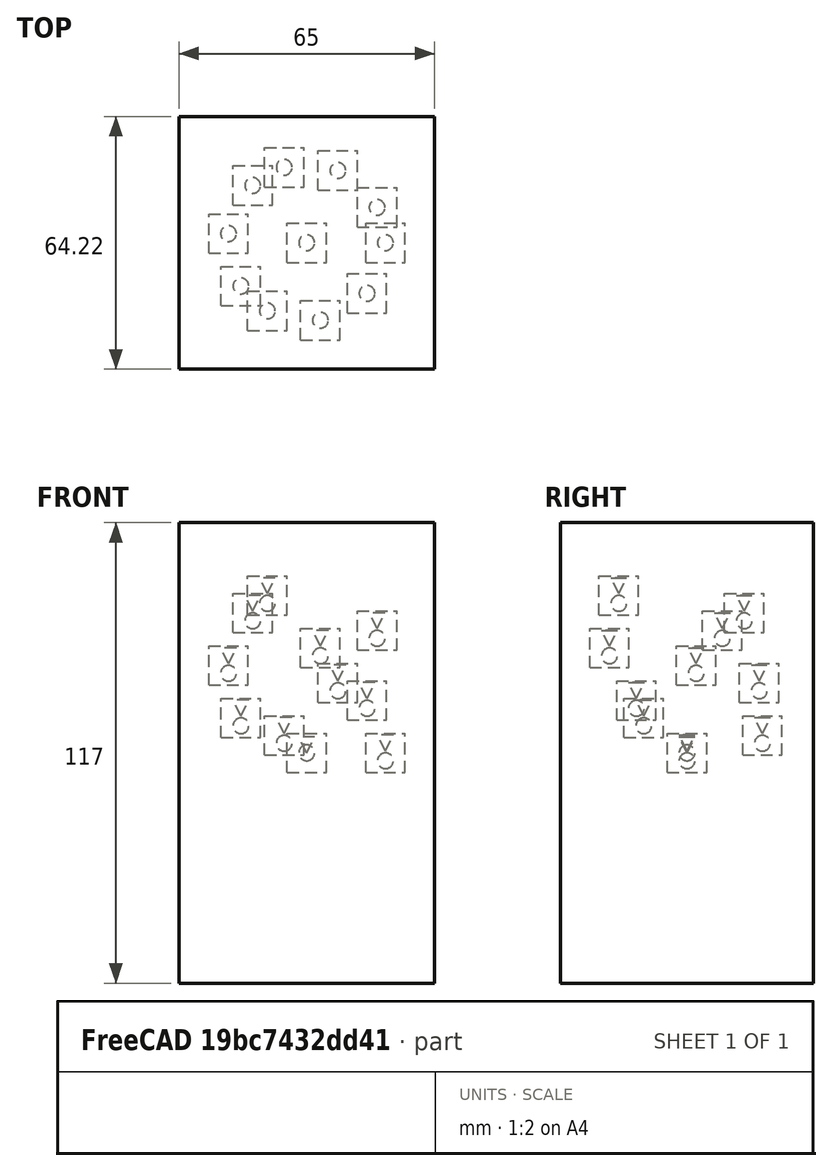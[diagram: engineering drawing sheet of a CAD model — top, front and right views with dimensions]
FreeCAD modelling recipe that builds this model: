
FCSTD DOCUMENT  (FreeCAD 0.21R33694 (Git))
Label: pathArray-of-part
License: All rights reserved
objects: App::DocumentObjectGroupPython×1251, App::Part×5, Part::FeaturePython×4, Part::Helix×1, Part::Cone×1
note: 6 computed .brp shape members not serialized (recipe doc carries the construction recipe); baked Part::Feature solids carry a one-line shape summary decoded from their .brp

FEATURE [App::DocumentObjectGroupPython] HALFPI  # scripted group (container) (typed FeaturePython)
  name = HALFPI
  value = pi/2.
FEATURE [App::DocumentObjectGroupPython] PI  # scripted group (container) (typed FeaturePython)
  name = PI
  value = 1.*pi
FEATURE [App::DocumentObjectGroupPython] TWOPI  # scripted group (container) (typed FeaturePython)
  name = TWOPI
  value = 2.*pi
FEATURE [App::DocumentObjectGroupPython] Constants  # scripted group (container) (typed FeaturePython)
  Group = -> [HALFPI,PI,TWOPI]
FEATURE [App::DocumentObjectGroupPython] Variables  # scripted group (container) (typed FeaturePython)
FEATURE [App::DocumentObjectGroupPython] Quantities  # scripted group (container) (typed FeaturePython)
FEATURE [App::DocumentObjectGroupPython] Isotopes  # scripted group (container) (typed FeaturePython)
FEATURE [App::DocumentObjectGroupPython] Elements  # scripted group (container) (typed FeaturePython)
FEATURE [App::DocumentObjectGroupPython] Matrix  # scripted group (container) (typed FeaturePython)
FEATURE [App::DocumentObjectGroupPython] Surfaces  # scripted group (container) (typed FeaturePython)
FEATURE [App::DocumentObjectGroupPython] Opticals  # scripted group (container) (typed FeaturePython)
  Group = -> [Matrix,Surfaces]
FEATURE [App::DocumentObjectGroupPython] G4Isotopes  # scripted group (container) (typed FeaturePython)
FEATURE [App::DocumentObjectGroupPython] H_element  # scripted group (container) (typed FeaturePython)
  Z = 1
  atom_value = 1.008
  formula = H
  name = H_element
FEATURE [App::DocumentObjectGroupPython] He_element  # scripted group (container) (typed FeaturePython)
  Z = 2
  atom_value = 4.0026
  formula = He
  name = He_element
FEATURE [App::DocumentObjectGroupPython] Li_element  # scripted group (container) (typed FeaturePython)
  Z = 3
  atom_value = 6.94
  formula = Li
  name = Li_element
FEATURE [App::DocumentObjectGroupPython] Be_element  # scripted group (container) (typed FeaturePython)
  Z = 4
  atom_value = 9.01218
  formula = Be
  name = Be_element
FEATURE [App::DocumentObjectGroupPython] B_element  # scripted group (container) (typed FeaturePython)
  Z = 5
  atom_value = 10.81
  formula = B
  name = B_element
FEATURE [App::DocumentObjectGroupPython] C_element  # scripted group (container) (typed FeaturePython)
  Z = 6
  atom_value = 12.011
  formula = C
  name = C_element
FEATURE [App::DocumentObjectGroupPython] N_element  # scripted group (container) (typed FeaturePython)
  Z = 7
  atom_value = 14.007
  formula = N
  name = N_element
FEATURE [App::DocumentObjectGroupPython] O_element  # scripted group (container) (typed FeaturePython)
  Z = 8
  atom_value = 15.999
  formula = O
  name = O_element
FEATURE [App::DocumentObjectGroupPython] F_element  # scripted group (container) (typed FeaturePython)
  Z = 9
  atom_value = 18.9984
  formula = F
  name = F_element
FEATURE [App::DocumentObjectGroupPython] Ne_element  # scripted group (container) (typed FeaturePython)
  Z = 10
  atom_value = 20.1797
  formula = Ne
  name = Ne_element
FEATURE [App::DocumentObjectGroupPython] Na_element  # scripted group (container) (typed FeaturePython)
  Z = 11
  atom_value = 22.9898
  formula = Na
  name = Na_element
FEATURE [App::DocumentObjectGroupPython] Mg_element  # scripted group (container) (typed FeaturePython)
  Z = 12
  atom_value = 24.305
  formula = Mg
  name = Mg_element
FEATURE [App::DocumentObjectGroupPython] Al_element  # scripted group (container) (typed FeaturePython)
  Z = 13
  atom_value = 26.9815
  formula = Al
  name = Al_element
FEATURE [App::DocumentObjectGroupPython] Si_element  # scripted group (container) (typed FeaturePython)
  Z = 14
  atom_value = 28.085
  formula = Si
  name = Si_element
FEATURE [App::DocumentObjectGroupPython] P_element  # scripted group (container) (typed FeaturePython)
  Z = 15
  atom_value = 30.9738
  formula = P
  name = P_element
FEATURE [App::DocumentObjectGroupPython] S_element  # scripted group (container) (typed FeaturePython)
  Z = 16
  atom_value = 32.06
  formula = S
  name = S_element
FEATURE [App::DocumentObjectGroupPython] Cl_element  # scripted group (container) (typed FeaturePython)
  Z = 17
  atom_value = 35.45
  formula = Cl
  name = Cl_element
FEATURE [App::DocumentObjectGroupPython] Ar_element  # scripted group (container) (typed FeaturePython)
  Z = 18
  atom_value = 39.95
  formula = Ar
  name = Ar_element
FEATURE [App::DocumentObjectGroupPython] K_element  # scripted group (container) (typed FeaturePython)
  Z = 19
  atom_value = 39.0983
  formula = K
  name = K_element
FEATURE [App::DocumentObjectGroupPython] Ca_element  # scripted group (container) (typed FeaturePython)
  Z = 20
  atom_value = 40.078
  formula = Ca
  name = Ca_element
FEATURE [App::DocumentObjectGroupPython] Sc_element  # scripted group (container) (typed FeaturePython)
  Z = 21
  atom_value = 44.9559
  formula = Sc
  name = Sc_element
FEATURE [App::DocumentObjectGroupPython] Ti_element  # scripted group (container) (typed FeaturePython)
  Z = 22
  atom_value = 47.867
  formula = Ti
  name = Ti_element
FEATURE [App::DocumentObjectGroupPython] V_element  # scripted group (container) (typed FeaturePython)
  Z = 23
  atom_value = 50.9415
  formula = V
  name = V_element
FEATURE [App::DocumentObjectGroupPython] Cr_element  # scripted group (container) (typed FeaturePython)
  Z = 24
  atom_value = 51.9961
  formula = Cr
  name = Cr_element
FEATURE [App::DocumentObjectGroupPython] Mn_element  # scripted group (container) (typed FeaturePython)
  Z = 25
  atom_value = 54.938
  formula = Mn
  name = Mn_element
FEATURE [App::DocumentObjectGroupPython] Fe_element  # scripted group (container) (typed FeaturePython)
  Z = 26
  atom_value = 55.845
  formula = Fe
  name = Fe_element
FEATURE [App::DocumentObjectGroupPython] Co_element  # scripted group (container) (typed FeaturePython)
  Z = 27
  atom_value = 58.9332
  formula = Co
  name = Co_element
FEATURE [App::DocumentObjectGroupPython] Ni_element  # scripted group (container) (typed FeaturePython)
  Z = 28
  atom_value = 58.6934
  formula = Ni
  name = Ni_element
FEATURE [App::DocumentObjectGroupPython] Cu_element  # scripted group (container) (typed FeaturePython)
  Z = 29
  atom_value = 63.546
  formula = Cu
  name = Cu_element
FEATURE [App::DocumentObjectGroupPython] Zn_element  # scripted group (container) (typed FeaturePython)
  Z = 30
  atom_value = 65.38
  formula = Zn
  name = Zn_element
FEATURE [App::DocumentObjectGroupPython] Ga_element  # scripted group (container) (typed FeaturePython)
  Z = 31
  atom_value = 69.723
  formula = Ga
  name = Ga_element
FEATURE [App::DocumentObjectGroupPython] Ge_element  # scripted group (container) (typed FeaturePython)
  Z = 32
  atom_value = 72.63
  formula = Ge
  name = Ge_element
FEATURE [App::DocumentObjectGroupPython] As_element  # scripted group (container) (typed FeaturePython)
  Z = 33
  atom_value = 74.9216
  formula = As
  name = As_element
FEATURE [App::DocumentObjectGroupPython] Se_element  # scripted group (container) (typed FeaturePython)
  Z = 34
  atom_value = 78.971
  formula = Se
  name = Se_element
FEATURE [App::DocumentObjectGroupPython] Br_element  # scripted group (container) (typed FeaturePython)
  Z = 35
  atom_value = 79.904
  formula = Br
  name = Br_element
FEATURE [App::DocumentObjectGroupPython] Kr_element  # scripted group (container) (typed FeaturePython)
  Z = 36
  atom_value = 83.798
  formula = Kr
  name = Kr_element
FEATURE [App::DocumentObjectGroupPython] Rb_element  # scripted group (container) (typed FeaturePython)
  Z = 37
  atom_value = 85.4678
  formula = Rb
  name = Rb_element
FEATURE [App::DocumentObjectGroupPython] Sr_element  # scripted group (container) (typed FeaturePython)
  Z = 38
  atom_value = 87.62
  formula = Sr
  name = Sr_element
FEATURE [App::DocumentObjectGroupPython] Y_element  # scripted group (container) (typed FeaturePython)
  Z = 39
  atom_value = 88.9058
  formula = Y
  name = Y_element
FEATURE [App::DocumentObjectGroupPython] Zr_element  # scripted group (container) (typed FeaturePython)
  Z = 40
  atom_value = 91.224
  formula = Zr
  name = Zr_element
FEATURE [App::DocumentObjectGroupPython] Nb_element  # scripted group (container) (typed FeaturePython)
  Z = 41
  atom_value = 92.9064
  formula = Nb
  name = Nb_element
FEATURE [App::DocumentObjectGroupPython] Mo_element  # scripted group (container) (typed FeaturePython)
  Z = 42
  atom_value = 95.95
  formula = Mo
  name = Mo_element
FEATURE [App::DocumentObjectGroupPython] Tc_element  # scripted group (container) (typed FeaturePython)
  Z = 43
  atom_value = 97
  formula = Tc
  name = Tc_element
FEATURE [App::DocumentObjectGroupPython] Ru_element  # scripted group (container) (typed FeaturePython)
  Z = 44
  atom_value = 101.07
  formula = Ru
  name = Ru_element
FEATURE [App::DocumentObjectGroupPython] Rh_element  # scripted group (container) (typed FeaturePython)
  Z = 45
  atom_value = 102.905
  formula = Rh
  name = Rh_element
FEATURE [App::DocumentObjectGroupPython] Pd_element  # scripted group (container) (typed FeaturePython)
  Z = 46
  atom_value = 106.42
  formula = Pd
  name = Pd_element
FEATURE [App::DocumentObjectGroupPython] Ag_element  # scripted group (container) (typed FeaturePython)
  Z = 47
  atom_value = 107.868
  formula = Ag
  name = Ag_element
FEATURE [App::DocumentObjectGroupPython] Cd_element  # scripted group (container) (typed FeaturePython)
  Z = 48
  atom_value = 112.414
  formula = Cd
  name = Cd_element
FEATURE [App::DocumentObjectGroupPython] In_element  # scripted group (container) (typed FeaturePython)
  Z = 49
  atom_value = 114.818
  formula = In
  name = In_element
FEATURE [App::DocumentObjectGroupPython] Sn_element  # scripted group (container) (typed FeaturePython)
  Z = 50
  atom_value = 118.71
  formula = Sn
  name = Sn_element
FEATURE [App::DocumentObjectGroupPython] Sb_element  # scripted group (container) (typed FeaturePython)
  Z = 51
  atom_value = 121.76
  formula = Sb
  name = Sb_element
FEATURE [App::DocumentObjectGroupPython] Te_element  # scripted group (container) (typed FeaturePython)
  Z = 52
  atom_value = 127.6
  formula = Te
  name = Te_element
FEATURE [App::DocumentObjectGroupPython] I_element  # scripted group (container) (typed FeaturePython)
  Z = 53
  atom_value = 126.904
  formula = I
  name = I_element
FEATURE [App::DocumentObjectGroupPython] Xe_element  # scripted group (container) (typed FeaturePython)
  Z = 54
  atom_value = 131.293
  formula = Xe
  name = Xe_element
FEATURE [App::DocumentObjectGroupPython] Cs_element  # scripted group (container) (typed FeaturePython)
  Z = 55
  atom_value = 132.905
  formula = Cs
  name = Cs_element
FEATURE [App::DocumentObjectGroupPython] Ba_element  # scripted group (container) (typed FeaturePython)
  Z = 56
  atom_value = 137.327
  formula = Ba
  name = Ba_element
FEATURE [App::DocumentObjectGroupPython] La_element  # scripted group (container) (typed FeaturePython)
  Z = 57
  atom_value = 138.905
  formula = La
  name = La_element
FEATURE [App::DocumentObjectGroupPython] Ce_element  # scripted group (container) (typed FeaturePython)
  Z = 58
  atom_value = 140.116
  formula = Ce
  name = Ce_element
FEATURE [App::DocumentObjectGroupPython] Pr_element  # scripted group (container) (typed FeaturePython)
  Z = 59
  atom_value = 140.908
  formula = Pr
  name = Pr_element
FEATURE [App::DocumentObjectGroupPython] Nd_element  # scripted group (container) (typed FeaturePython)
  Z = 60
  atom_value = 144.242
  formula = Nd
  name = Nd_element
FEATURE [App::DocumentObjectGroupPython] Pm_element  # scripted group (container) (typed FeaturePython)
  Z = 61
  atom_value = 145
  formula = Pm
  name = Pm_element
FEATURE [App::DocumentObjectGroupPython] Sm_element  # scripted group (container) (typed FeaturePython)
  Z = 62
  atom_value = 150.36
  formula = Sm
  name = Sm_element
FEATURE [App::DocumentObjectGroupPython] Eu_element  # scripted group (container) (typed FeaturePython)
  Z = 63
  atom_value = 151.964
  formula = Eu
  name = Eu_element
FEATURE [App::DocumentObjectGroupPython] Gd_element  # scripted group (container) (typed FeaturePython)
  Z = 64
  atom_value = 157.25
  formula = Gd
  name = Gd_element
FEATURE [App::DocumentObjectGroupPython] Tb_element  # scripted group (container) (typed FeaturePython)
  Z = 65
  atom_value = 158.925
  formula = Tb
  name = Tb_element
FEATURE [App::DocumentObjectGroupPython] Dy_element  # scripted group (container) (typed FeaturePython)
  Z = 66
  atom_value = 162.5
  formula = Dy
  name = Dy_element
FEATURE [App::DocumentObjectGroupPython] Ho_element  # scripted group (container) (typed FeaturePython)
  Z = 67
  atom_value = 164.93
  formula = Ho
  name = Ho_element
FEATURE [App::DocumentObjectGroupPython] Er_element  # scripted group (container) (typed FeaturePython)
  Z = 68
  atom_value = 167.259
  formula = Er
  name = Er_element
FEATURE [App::DocumentObjectGroupPython] Tm_element  # scripted group (container) (typed FeaturePython)
  Z = 69
  atom_value = 168.934
  formula = Tm
  name = Tm_element
FEATURE [App::DocumentObjectGroupPython] Yb_element  # scripted group (container) (typed FeaturePython)
  Z = 70
  atom_value = 173.045
  formula = Yb
  name = Yb_element
FEATURE [App::DocumentObjectGroupPython] Lu_element  # scripted group (container) (typed FeaturePython)
  Z = 71
  atom_value = 174.967
  formula = Lu
  name = Lu_element
FEATURE [App::DocumentObjectGroupPython] Hf_element  # scripted group (container) (typed FeaturePython)
  Z = 72
  atom_value = 178.49
  formula = Hf
  name = Hf_element
FEATURE [App::DocumentObjectGroupPython] Ta_element  # scripted group (container) (typed FeaturePython)
  Z = 73
  atom_value = 180.948
  formula = Ta
  name = Ta_element
FEATURE [App::DocumentObjectGroupPython] W_element  # scripted group (container) (typed FeaturePython)
  Z = 74
  atom_value = 183.84
  formula = W
  name = W_element
FEATURE [App::DocumentObjectGroupPython] Re_element  # scripted group (container) (typed FeaturePython)
  Z = 75
  atom_value = 186.207
  formula = Re
  name = Re_element
FEATURE [App::DocumentObjectGroupPython] Os_element  # scripted group (container) (typed FeaturePython)
  Z = 76
  atom_value = 190.23
  formula = Os
  name = Os_element
FEATURE [App::DocumentObjectGroupPython] Ir_element  # scripted group (container) (typed FeaturePython)
  Z = 77
  atom_value = 192.217
  formula = Ir
  name = Ir_element
FEATURE [App::DocumentObjectGroupPython] Pt_element  # scripted group (container) (typed FeaturePython)
  Z = 78
  atom_value = 195.084
  formula = Pt
  name = Pt_element
FEATURE [App::DocumentObjectGroupPython] Au_element  # scripted group (container) (typed FeaturePython)
  Z = 79
  atom_value = 196.967
  formula = Au
  name = Au_element
FEATURE [App::DocumentObjectGroupPython] Hg_element  # scripted group (container) (typed FeaturePython)
  Z = 80
  atom_value = 200.592
  formula = Hg
  name = Hg_element
FEATURE [App::DocumentObjectGroupPython] Tl_element  # scripted group (container) (typed FeaturePython)
  Z = 81
  atom_value = 204.38
  formula = Tl
  name = Tl_element
FEATURE [App::DocumentObjectGroupPython] Pb_element  # scripted group (container) (typed FeaturePython)
  Z = 82
  atom_value = 207.2
  formula = Pb
  name = Pb_element
FEATURE [App::DocumentObjectGroupPython] Bi_element  # scripted group (container) (typed FeaturePython)
  Z = 83
  atom_value = 208.98
  formula = Bi
  name = Bi_element
FEATURE [App::DocumentObjectGroupPython] Po_element  # scripted group (container) (typed FeaturePython)
  Z = 84
  atom_value = 209
  formula = Po
  name = Po_element
FEATURE [App::DocumentObjectGroupPython] At_element  # scripted group (container) (typed FeaturePython)
  Z = 85
  atom_value = 210
  formula = At
  name = At_element
FEATURE [App::DocumentObjectGroupPython] Rn_element  # scripted group (container) (typed FeaturePython)
  Z = 86
  atom_value = 222
  formula = Rn
  name = Rn_element
FEATURE [App::DocumentObjectGroupPython] Fr_element  # scripted group (container) (typed FeaturePython)
  Z = 87
  atom_value = 223
  formula = Fr
  name = Fr_element
FEATURE [App::DocumentObjectGroupPython] Ra_element  # scripted group (container) (typed FeaturePython)
  Z = 88
  atom_value = 226
  formula = Ra
  name = Ra_element
FEATURE [App::DocumentObjectGroupPython] Ac_element  # scripted group (container) (typed FeaturePython)
  Z = 89
  atom_value = 227
  formula = Ac
  name = Ac_element
FEATURE [App::DocumentObjectGroupPython] Th_element  # scripted group (container) (typed FeaturePython)
  Z = 90
  atom_value = 232.038
  formula = Th
  name = Th_element
FEATURE [App::DocumentObjectGroupPython] Pa_element  # scripted group (container) (typed FeaturePython)
  Z = 91
  atom_value = 231.036
  formula = Pa
  name = Pa_element
FEATURE [App::DocumentObjectGroupPython] U_element  # scripted group (container) (typed FeaturePython)
  Z = 92
  atom_value = 238.029
  formula = U
  name = U_element
FEATURE [App::DocumentObjectGroupPython] Np_element  # scripted group (container) (typed FeaturePython)
  Z = 93
  atom_value = 237
  formula = Np
  name = Np_element
FEATURE [App::DocumentObjectGroupPython] Pu_element  # scripted group (container) (typed FeaturePython)
  Z = 94
  atom_value = 244
  formula = Pu
  name = Pu_element
FEATURE [App::DocumentObjectGroupPython] Am_element  # scripted group (container) (typed FeaturePython)
  Z = 95
  atom_value = 243
  formula = Am
  name = Am_element
FEATURE [App::DocumentObjectGroupPython] Cm_element  # scripted group (container) (typed FeaturePython)
  Z = 96
  atom_value = 247
  formula = Cm
  name = Cm_element
FEATURE [App::DocumentObjectGroupPython] Bk_element  # scripted group (container) (typed FeaturePython)
  Z = 97
  atom_value = 247
  formula = Bk
  name = Bk_element
FEATURE [App::DocumentObjectGroupPython] Cf_element  # scripted group (container) (typed FeaturePython)
  Z = 98
  atom_value = 251
  formula = Cf
  name = Cf_element
FEATURE [App::DocumentObjectGroupPython] G4Elements  # scripted group (container) (typed FeaturePython)
  Group = -> [H_element,He_element,Li_element,Be_element,B_element,C_element,N_element,O_element,F_element,Ne_element,Na_element,Mg_element,Al_element,Si_element,P_element,S_element,Cl_element,Ar_element,K_element,Ca_element,Sc_element,Ti_element,V_element,Cr_element,Mn_element,Fe_element,Co_element,Ni_element,Cu_element,Zn_element,Ga_element,Ge_element,As_element,Se_element,Br_element,Kr_element,Rb_element,+61 more]
FEATURE [App::DocumentObjectGroupPython] H_element001  label="H_element : 0.101"  # scripted group (container) (typed FeaturePython)
  n = 0.101327
FEATURE [App::DocumentObjectGroupPython] C_element001  label="C_element : 0.775"  # scripted group (container) (typed FeaturePython)
  n = 0.7755
FEATURE [App::DocumentObjectGroupPython] N_element001  label="N_element : 0.035"  # scripted group (container) (typed FeaturePython)
  n = 0.035057
FEATURE [App::DocumentObjectGroupPython] O_element001  label="O_element : 0.052"  # scripted group (container) (typed FeaturePython)
  n = 0.0523159
FEATURE [App::DocumentObjectGroupPython] F_element001  label="F_element : 0.017"  # scripted group (container) (typed FeaturePython)
  n = 0.017422
FEATURE [App::DocumentObjectGroupPython] Ca_element001  label="Ca_element : 0.018"  # scripted group (container) (typed FeaturePython)
  n = 0.018378
FEATURE [App::DocumentObjectGroupPython] G4_A_150_TISSUE  label="G4_A-150_TISSUE"  # scripted group (container) (typed FeaturePython)
  Dunit = g/cm3
  Dvalue = 1.127
  Group = -> [H_element001,C_element001,N_element001,O_element001,F_element001,Ca_element001]
  conduct = 2
  density = 1
  expand = 3
  formula = G4_A-150_TISSUE
  name = G4_A-150_TISSUE
  specific = 4
FEATURE [App::DocumentObjectGroupPython] C_element002  label="C_element : 3"  # scripted group (container) (typed FeaturePython)
  n = 3
  ref = C_element
FEATURE [App::DocumentObjectGroupPython] H_element002  label="H_element : 6"  # scripted group (container) (typed FeaturePython)
  n = 6
  ref = H_element
FEATURE [App::DocumentObjectGroupPython] O_element002  label="O_element : 1"  # scripted group (container) (typed FeaturePython)
  n = 1
  ref = O_element
FEATURE [App::DocumentObjectGroupPython] G4_ACETONE  # scripted group (container) (typed FeaturePython)
  Dunit = g/cm3
  Dvalue = 0.7899
  Group = -> [C_element002,H_element002,O_element002]
  conduct = 2
  density = 1
  expand = 3
  formula = G4_ACETONE
  name = G4_ACETONE
  specific = 4
FEATURE [App::DocumentObjectGroupPython] C_element003  label="C_element : 2"  # scripted group (container) (typed FeaturePython)
  n = 2
  ref = C_element
FEATURE [App::DocumentObjectGroupPython] H_element003  label="H_element : 2"  # scripted group (container) (typed FeaturePython)
  n = 2
  ref = H_element
FEATURE [App::DocumentObjectGroupPython] G4_ACETYLENE  # scripted group (container) (typed FeaturePython)
  Dunit = g/cm3
  Dvalue = 0.0010967
  Group = -> [C_element003,H_element003]
  conduct = 2
  density = 1
  expand = 3
  formula = G4_ACETYLENE
  name = G4_ACETYLENE
  specific = 4
FEATURE [App::DocumentObjectGroupPython] C_element004  label="C_element : 5"  # scripted group (container) (typed FeaturePython)
  n = 5
  ref = C_element
FEATURE [App::DocumentObjectGroupPython] H_element004  label="H_element : 5"  # scripted group (container) (typed FeaturePython)
  n = 5
  ref = H_element
FEATURE [App::DocumentObjectGroupPython] N_element002  label="N_element : 5"  # scripted group (container) (typed FeaturePython)
  n = 5
  ref = N_element
FEATURE [App::DocumentObjectGroupPython] G4_ADENINE  # scripted group (container) (typed FeaturePython)
  Dunit = g/cm3
  Dvalue = 1.6
  Group = -> [C_element004,H_element004,N_element002]
  conduct = 2
  density = 1
  expand = 3
  formula = G4_ADENINE
  name = G4_ADENINE
  specific = 4
FEATURE [App::DocumentObjectGroupPython] H_element005  label="H_element : 0.114"  # scripted group (container) (typed FeaturePython)
  n = 0.114
FEATURE [App::DocumentObjectGroupPython] C_element005  label="C_element : 0.598"  # scripted group (container) (typed FeaturePython)
  n = 0.598
FEATURE [App::DocumentObjectGroupPython] N_element003  label="N_element : 0.007"  # scripted group (container) (typed FeaturePython)
  n = 0.007
FEATURE [App::DocumentObjectGroupPython] O_element003  label="O_element : 0.278"  # scripted group (container) (typed FeaturePython)
  n = 0.278
FEATURE [App::DocumentObjectGroupPython] Na_element001  label="Na_element : 0.001"  # scripted group (container) (typed FeaturePython)
  n = 0.001
FEATURE [App::DocumentObjectGroupPython] S_element001  label="S_element : 0.001"  # scripted group (container) (typed FeaturePython)
  n = 0.001
FEATURE [App::DocumentObjectGroupPython] Cl_element001  label="Cl_element : 0.001"  # scripted group (container) (typed FeaturePython)
  n = 0.001
FEATURE [App::DocumentObjectGroupPython] G4_ADIPOSE_TISSUE_ICRP  # scripted group (container) (typed FeaturePython)
  Dunit = g/cm3
  Dvalue = 0.95
  Group = -> [H_element005,C_element005,N_element003,O_element003,Na_element001,S_element001,Cl_element001]
  conduct = 2
  density = 1
  expand = 3
  formula = G4_ADIPOSE_TISSUE_ICRP
  name = G4_ADIPOSE_TISSUE_ICRP
  specific = 4
FEATURE [App::DocumentObjectGroupPython] C_element006  label="C_element : 0.000"  # scripted group (container) (typed FeaturePython)
  n = 0.000124
FEATURE [App::DocumentObjectGroupPython] N_element004  label="N_element : 0.755"  # scripted group (container) (typed FeaturePython)
  n = 0.755268
FEATURE [App::DocumentObjectGroupPython] O_element004  label="O_element : 0.232"  # scripted group (container) (typed FeaturePython)
  n = 0.231781
FEATURE [App::DocumentObjectGroupPython] Ar_element001  label="Ar_element : 0.013"  # scripted group (container) (typed FeaturePython)
  n = 0.012827
FEATURE [App::DocumentObjectGroupPython] G4_AIR  # scripted group (container) (typed FeaturePython)
  Dunit = g/cm3
  Dvalue = 0.00120479
  Group = -> [C_element006,N_element004,O_element004,Ar_element001]
  conduct = 2
  density = 1
  expand = 3
  formula = G4_AIR
  name = G4_AIR
  specific = 4
FEATURE [App::DocumentObjectGroupPython] C_element007  label="C_element : 006"  # scripted group (container) (typed FeaturePython)
  n = 3
  ref = C_element
FEATURE [App::DocumentObjectGroupPython] H_element006  label="H_element : 7"  # scripted group (container) (typed FeaturePython)
  n = 7
  ref = H_element
FEATURE [App::DocumentObjectGroupPython] N_element005  label="N_element : 1"  # scripted group (container) (typed FeaturePython)
  n = 1
  ref = N_element
FEATURE [App::DocumentObjectGroupPython] O_element005  label="O_element : 2"  # scripted group (container) (typed FeaturePython)
  n = 2
  ref = O_element
FEATURE [App::DocumentObjectGroupPython] G4_ALANINE  # scripted group (container) (typed FeaturePython)
  Dunit = g/cm3
  Dvalue = 1.42
  Group = -> [C_element007,H_element006,N_element005,O_element005]
  conduct = 2
  density = 1
  expand = 3
  formula = G4_ALANINE
  name = G4_ALANINE
  specific = 4
FEATURE [App::DocumentObjectGroupPython] Al_element001  label="Al_element : 2"  # scripted group (container) (typed FeaturePython)
  n = 2
  ref = Al_element
FEATURE [App::DocumentObjectGroupPython] O_element006  label="O_element : 3"  # scripted group (container) (typed FeaturePython)
  n = 3
  ref = O_element
FEATURE [App::DocumentObjectGroupPython] G4_ALUMINUM_OXIDE  # scripted group (container) (typed FeaturePython)
  Dunit = g/cm3
  Dvalue = 3.97
  Group = -> [Al_element001,O_element006]
  conduct = 2
  density = 1
  expand = 3
  formula = G4_ALUMINUM_OXIDE
  name = G4_ALUMINUM_OXIDE
  specific = 4
FEATURE [App::DocumentObjectGroupPython] H_element007  label="H_element : 0.106"  # scripted group (container) (typed FeaturePython)
  n = 0.10593
FEATURE [App::DocumentObjectGroupPython] C_element008  label="C_element : 0.789"  # scripted group (container) (typed FeaturePython)
  n = 0.788974
FEATURE [App::DocumentObjectGroupPython] O_element007  label="O_element : 0.105"  # scripted group (container) (typed FeaturePython)
  n = 0.105096
FEATURE [App::DocumentObjectGroupPython] G4_AMBER  # scripted group (container) (typed FeaturePython)
  Dunit = g/cm3
  Dvalue = 1.1
  Group = -> [H_element007,C_element008,O_element007]
  conduct = 2
  density = 1
  expand = 3
  formula = G4_AMBER
  name = G4_AMBER
  specific = 4
FEATURE [App::DocumentObjectGroupPython] N_element006  label="N_element : 006"  # scripted group (container) (typed FeaturePython)
  n = 1
  ref = N_element
FEATURE [App::DocumentObjectGroupPython] H_element008  label="H_element : 3"  # scripted group (container) (typed FeaturePython)
  n = 3
  ref = H_element
FEATURE [App::DocumentObjectGroupPython] G4_AMMONIA  # scripted group (container) (typed FeaturePython)
  Dunit = g/cm3
  Dvalue = 0.000826019
  Group = -> [N_element006,H_element008]
  conduct = 2
  density = 1
  expand = 3
  formula = G4_AMMONIA
  name = G4_AMMONIA
  specific = 4
FEATURE [App::DocumentObjectGroupPython] C_element009  label="C_element : 6"  # scripted group (container) (typed FeaturePython)
  n = 6
  ref = C_element
FEATURE [App::DocumentObjectGroupPython] H_element009  label="H_element : 008"  # scripted group (container) (typed FeaturePython)
  n = 7
  ref = H_element
FEATURE [App::DocumentObjectGroupPython] N_element007  label="N_element : 007"  # scripted group (container) (typed FeaturePython)
  n = 1
  ref = N_element
FEATURE [App::DocumentObjectGroupPython] G4_ANILINE  # scripted group (container) (typed FeaturePython)
  Dunit = g/cm3
  Dvalue = 1.0235
  Group = -> [C_element009,H_element009,N_element007]
  conduct = 2
  density = 1
  expand = 3
  formula = G4_ANILINE
  name = G4_ANILINE
  specific = 4
FEATURE [App::DocumentObjectGroupPython] C_element010  label="C_element : 14"  # scripted group (container) (typed FeaturePython)
  n = 14
  ref = C_element
FEATURE [App::DocumentObjectGroupPython] H_element010  label="H_element : 10"  # scripted group (container) (typed FeaturePython)
  n = 10
  ref = H_element
FEATURE [App::DocumentObjectGroupPython] G4_ANTHRACENE  # scripted group (container) (typed FeaturePython)
  Dunit = g/cm3
  Dvalue = 1.283
  Group = -> [C_element010,H_element010]
  conduct = 2
  density = 1
  expand = 3
  formula = G4_ANTHRACENE
  name = G4_ANTHRACENE
  specific = 4
FEATURE [App::DocumentObjectGroupPython] H_element011  label="H_element : 0.065"  # scripted group (container) (typed FeaturePython)
  n = 0.0654709
FEATURE [App::DocumentObjectGroupPython] C_element011  label="C_element : 0.537"  # scripted group (container) (typed FeaturePython)
  n = 0.536944
FEATURE [App::DocumentObjectGroupPython] N_element008  label="N_element : 0.021"  # scripted group (container) (typed FeaturePython)
  n = 0.0215
FEATURE [App::DocumentObjectGroupPython] O_element008  label="O_element : 0.032"  # scripted group (container) (typed FeaturePython)
  n = 0.032085
FEATURE [App::DocumentObjectGroupPython] F_element002  label="F_element : 0.167"  # scripted group (container) (typed FeaturePython)
  n = 0.167411
FEATURE [App::DocumentObjectGroupPython] Ca_element002  label="Ca_element : 0.177"  # scripted group (container) (typed FeaturePython)
  n = 0.176589
FEATURE [App::DocumentObjectGroupPython] G4_B_100_BONE  label="G4_B-100_BONE"  # scripted group (container) (typed FeaturePython)
  Dunit = g/cm3
  Dvalue = 1.45
  Group = -> [H_element011,C_element011,N_element008,O_element008,F_element002,Ca_element002]
  conduct = 2
  density = 1
  expand = 3
  formula = G4_B-100_BONE
  name = G4_B-100_BONE
  specific = 4
FEATURE [App::DocumentObjectGroupPython] H_element012  label="H_element : 0.057"  # scripted group (container) (typed FeaturePython)
  n = 0.057441
FEATURE [App::DocumentObjectGroupPython] C_element012  label="C_element : 0.790"  # scripted group (container) (typed FeaturePython)
  n = 0.774591
FEATURE [App::DocumentObjectGroupPython] O_element009  label="O_element : 0.168"  # scripted group (container) (typed FeaturePython)
  n = 0.167968
FEATURE [App::DocumentObjectGroupPython] G4_BAKELITE  # scripted group (container) (typed FeaturePython)
  Dunit = g/cm3
  Dvalue = 1.25
  Group = -> [H_element012,C_element012,O_element009]
  conduct = 2
  density = 1
  expand = 3
  formula = G4_BAKELITE
  name = G4_BAKELITE
  specific = 4
FEATURE [App::DocumentObjectGroupPython] Ba_element001  label="Ba_element : 1"  # scripted group (container) (typed FeaturePython)
  n = 1
  ref = Ba_element
FEATURE [App::DocumentObjectGroupPython] F_element003  label="F_element : 2"  # scripted group (container) (typed FeaturePython)
  n = 2
  ref = F_element
FEATURE [App::DocumentObjectGroupPython] G4_BARIUM_FLUORIDE  # scripted group (container) (typed FeaturePython)
  Dunit = g/cm3
  Dvalue = 4.89
  Group = -> [Ba_element001,F_element003]
  conduct = 2
  density = 1
  expand = 3
  formula = G4_BARIUM_FLUORIDE
  name = G4_BARIUM_FLUORIDE
  specific = 4
FEATURE [App::DocumentObjectGroupPython] Ba_element002  label="Ba_element : 002"  # scripted group (container) (typed FeaturePython)
  n = 1
  ref = Ba_element
FEATURE [App::DocumentObjectGroupPython] S_element002  label="S_element : 1"  # scripted group (container) (typed FeaturePython)
  n = 1
  ref = S_element
FEATURE [App::DocumentObjectGroupPython] O_element010  label="O_element : 4"  # scripted group (container) (typed FeaturePython)
  n = 4
  ref = O_element
FEATURE [App::DocumentObjectGroupPython] G4_BARIUM_SULFATE  # scripted group (container) (typed FeaturePython)
  Dunit = g/cm3
  Dvalue = 4.5
  Group = -> [Ba_element002,S_element002,O_element010]
  conduct = 2
  density = 1
  expand = 3
  formula = G4_BARIUM_SULFATE
  name = G4_BARIUM_SULFATE
  specific = 4
FEATURE [App::DocumentObjectGroupPython] C_element013  label="C_element : 007"  # scripted group (container) (typed FeaturePython)
  n = 6
  ref = C_element
FEATURE [App::DocumentObjectGroupPython] H_element013  label="H_element : 009"  # scripted group (container) (typed FeaturePython)
  n = 6
  ref = H_element
FEATURE [App::DocumentObjectGroupPython] G4_BENZENE  # scripted group (container) (typed FeaturePython)
  Dunit = g/cm3
  Dvalue = 0.87865
  Group = -> [C_element013,H_element013]
  conduct = 2
  density = 1
  expand = 3
  formula = G4_BENZENE
  name = G4_BENZENE
  specific = 4
FEATURE [App::DocumentObjectGroupPython] Be_element001  label="Be_element : 1"  # scripted group (container) (typed FeaturePython)
  n = 1
  ref = Be_element
FEATURE [App::DocumentObjectGroupPython] O_element011  label="O_element : 005"  # scripted group (container) (typed FeaturePython)
  n = 1
  ref = O_element
FEATURE [App::DocumentObjectGroupPython] G4_BERYLLIUM_OXIDE  # scripted group (container) (typed FeaturePython)
  Dunit = g/cm3
  Dvalue = 3.01
  Group = -> [Be_element001,O_element011]
  conduct = 2
  density = 1
  expand = 3
  formula = G4_BERYLLIUM_OXIDE
  name = G4_BERYLLIUM_OXIDE
  specific = 4
FEATURE [App::DocumentObjectGroupPython] Bi_element001  label="Bi_element : 4"  # scripted group (container) (typed FeaturePython)
  n = 4
  ref = Bi_element
FEATURE [App::DocumentObjectGroupPython] Ge_element001  label="Ge_element : 3"  # scripted group (container) (typed FeaturePython)
  n = 3
  ref = Ge_element
FEATURE [App::DocumentObjectGroupPython] O_element012  label="O_element : 12"  # scripted group (container) (typed FeaturePython)
  n = 12
  ref = O_element
FEATURE [App::DocumentObjectGroupPython] G4_BGO  # scripted group (container) (typed FeaturePython)
  Dunit = g/cm3
  Dvalue = 7.13
  Group = -> [Bi_element001,Ge_element001,O_element012]
  conduct = 2
  density = 1
  expand = 3
  formula = G4_BGO
  name = G4_BGO
  specific = 4
FEATURE [App::DocumentObjectGroupPython] H_element014  label="H_element : 0.102"  # scripted group (container) (typed FeaturePython)
  n = 0.102
FEATURE [App::DocumentObjectGroupPython] C_element014  label="C_element : 0.110"  # scripted group (container) (typed FeaturePython)
  n = 0.11
FEATURE [App::DocumentObjectGroupPython] N_element009  label="N_element : 0.033"  # scripted group (container) (typed FeaturePython)
  n = 0.033
FEATURE [App::DocumentObjectGroupPython] O_element013  label="O_element : 0.745"  # scripted group (container) (typed FeaturePython)
  n = 0.745
FEATURE [App::DocumentObjectGroupPython] Na_element002  label="Na_element : 0.002"  # scripted group (container) (typed FeaturePython)
  n = 0.001
FEATURE [App::DocumentObjectGroupPython] P_element001  label="P_element : 0.001"  # scripted group (container) (typed FeaturePython)
  n = 0.001
FEATURE [App::DocumentObjectGroupPython] S_element003  label="S_element : 0.002"  # scripted group (container) (typed FeaturePython)
  n = 0.002
FEATURE [App::DocumentObjectGroupPython] Cl_element002  label="Cl_element : 0.003"  # scripted group (container) (typed FeaturePython)
  n = 0.003
FEATURE [App::DocumentObjectGroupPython] K_element001  label="K_element : 0.002"  # scripted group (container) (typed FeaturePython)
  n = 0.002
FEATURE [App::DocumentObjectGroupPython] Fe_element001  label="Fe_element : 0.001"  # scripted group (container) (typed FeaturePython)
  n = 0.001
FEATURE [App::DocumentObjectGroupPython] G4_BLOOD_ICRP  # scripted group (container) (typed FeaturePython)
  Dunit = g/cm3
  Dvalue = 1.06
  Group = -> [H_element014,C_element014,N_element009,O_element013,Na_element002,P_element001,S_element003,Cl_element002,K_element001,Fe_element001]
  conduct = 2
  density = 1
  expand = 3
  formula = G4_BLOOD_ICRP
  name = G4_BLOOD_ICRP
  specific = 4
FEATURE [App::DocumentObjectGroupPython] H_element015  label="H_element : 0.064"  # scripted group (container) (typed FeaturePython)
  n = 0.064
FEATURE [App::DocumentObjectGroupPython] C_element015  label="C_element : 0.278"  # scripted group (container) (typed FeaturePython)
  n = 0.278
FEATURE [App::DocumentObjectGroupPython] N_element010  label="N_element : 0.027"  # scripted group (container) (typed FeaturePython)
  n = 0.027
FEATURE [App::DocumentObjectGroupPython] O_element014  label="O_element : 0.410"  # scripted group (container) (typed FeaturePython)
  n = 0.41
FEATURE [App::DocumentObjectGroupPython] Mg_element001  label="Mg_element : 0.002"  # scripted group (container) (typed FeaturePython)
  n = 0.002
FEATURE [App::DocumentObjectGroupPython] P_element002  label="P_element : 0.070"  # scripted group (container) (typed FeaturePython)
  n = 0.07
FEATURE [App::DocumentObjectGroupPython] S_element004  label="S_element : 0.003"  # scripted group (container) (typed FeaturePython)
  n = 0.002
FEATURE [App::DocumentObjectGroupPython] Ca_element003  label="Ca_element : 0.147"  # scripted group (container) (typed FeaturePython)
  n = 0.147
FEATURE [App::DocumentObjectGroupPython] G4_BONE_COMPACT_ICRU  # scripted group (container) (typed FeaturePython)
  Dunit = g/cm3
  Dvalue = 1.85
  Group = -> [H_element015,C_element015,N_element010,O_element014,Mg_element001,P_element002,S_element004,Ca_element003]
  conduct = 2
  density = 1
  expand = 3
  formula = G4_BONE_COMPACT_ICRU
  name = G4_BONE_COMPACT_ICRU
  specific = 4
FEATURE [App::DocumentObjectGroupPython] H_element016  label="H_element : 0.034"  # scripted group (container) (typed FeaturePython)
  n = 0.034
FEATURE [App::DocumentObjectGroupPython] C_element016  label="C_element : 0.155"  # scripted group (container) (typed FeaturePython)
  n = 0.155
FEATURE [App::DocumentObjectGroupPython] N_element011  label="N_element : 0.042"  # scripted group (container) (typed FeaturePython)
  n = 0.042
FEATURE [App::DocumentObjectGroupPython] O_element015  label="O_element : 0.435"  # scripted group (container) (typed FeaturePython)
  n = 0.435
FEATURE [App::DocumentObjectGroupPython] Na_element003  label="Na_element : 0.003"  # scripted group (container) (typed FeaturePython)
  n = 0.001
FEATURE [App::DocumentObjectGroupPython] Mg_element002  label="Mg_element : 0.003"  # scripted group (container) (typed FeaturePython)
  n = 0.002
FEATURE [App::DocumentObjectGroupPython] P_element003  label="P_element : 0.103"  # scripted group (container) (typed FeaturePython)
  n = 0.103
FEATURE [App::DocumentObjectGroupPython] S_element005  label="S_element : 0.004"  # scripted group (container) (typed FeaturePython)
  n = 0.003
FEATURE [App::DocumentObjectGroupPython] Ca_element004  label="Ca_element : 0.225"  # scripted group (container) (typed FeaturePython)
  n = 0.225
FEATURE [App::DocumentObjectGroupPython] G4_BONE_CORTICAL_ICRP  # scripted group (container) (typed FeaturePython)
  Dunit = g/cm3
  Dvalue = 1.92
  Group = -> [H_element016,C_element016,N_element011,O_element015,Na_element003,Mg_element002,P_element003,S_element005,Ca_element004]
  conduct = 2
  density = 1
  expand = 3
  formula = G4_BONE_CORTICAL_ICRP
  name = G4_BONE_CORTICAL_ICRP
  specific = 4
FEATURE [App::DocumentObjectGroupPython] B_element001  label="B_element : 4"  # scripted group (container) (typed FeaturePython)
  n = 4
  ref = B_element
FEATURE [App::DocumentObjectGroupPython] C_element017  label="C_element : 1"  # scripted group (container) (typed FeaturePython)
  n = 1
  ref = C_element
FEATURE [App::DocumentObjectGroupPython] G4_BORON_CARBIDE  # scripted group (container) (typed FeaturePython)
  Dunit = g/cm3
  Dvalue = 2.52
  Group = -> [B_element001,C_element017]
  conduct = 2
  density = 1
  expand = 3
  formula = G4_BORON_CARBIDE
  name = G4_BORON_CARBIDE
  specific = 4
FEATURE [App::DocumentObjectGroupPython] B_element002  label="B_element : 2"  # scripted group (container) (typed FeaturePython)
  n = 2
  ref = B_element
FEATURE [App::DocumentObjectGroupPython] O_element016  label="O_element : 006"  # scripted group (container) (typed FeaturePython)
  n = 3
  ref = O_element
FEATURE [App::DocumentObjectGroupPython] G4_BORON_OXIDE  # scripted group (container) (typed FeaturePython)
  Dunit = g/cm3
  Dvalue = 1.812
  Group = -> [B_element002,O_element016]
  conduct = 2
  density = 1
  expand = 3
  formula = G4_BORON_OXIDE
  name = G4_BORON_OXIDE
  specific = 4
FEATURE [App::DocumentObjectGroupPython] H_element017  label="H_element : 0.107"  # scripted group (container) (typed FeaturePython)
  n = 0.107
FEATURE [App::DocumentObjectGroupPython] C_element018  label="C_element : 0.145"  # scripted group (container) (typed FeaturePython)
  n = 0.145
FEATURE [App::DocumentObjectGroupPython] N_element012  label="N_element : 0.022"  # scripted group (container) (typed FeaturePython)
  n = 0.022
FEATURE [App::DocumentObjectGroupPython] O_element017  label="O_element : 0.712"  # scripted group (container) (typed FeaturePython)
  n = 0.712
FEATURE [App::DocumentObjectGroupPython] Na_element004  label="Na_element : 0.004"  # scripted group (container) (typed FeaturePython)
  n = 0.002
FEATURE [App::DocumentObjectGroupPython] P_element004  label="P_element : 0.004"  # scripted group (container) (typed FeaturePython)
  n = 0.004
FEATURE [App::DocumentObjectGroupPython] S_element006  label="S_element : 0.005"  # scripted group (container) (typed FeaturePython)
  n = 0.002
FEATURE [App::DocumentObjectGroupPython] Cl_element003  label="Cl_element : 0.004"  # scripted group (container) (typed FeaturePython)
  n = 0.003
FEATURE [App::DocumentObjectGroupPython] K_element002  label="K_element : 0.003"  # scripted group (container) (typed FeaturePython)
  n = 0.003
FEATURE [App::DocumentObjectGroupPython] G4_BRAIN_ICRP  # scripted group (container) (typed FeaturePython)
  Dunit = g/cm3
  Dvalue = 1.04
  Group = -> [H_element017,C_element018,N_element012,O_element017,Na_element004,P_element004,S_element006,Cl_element003,K_element002]
  conduct = 2
  density = 1
  expand = 3
  formula = G4_BRAIN_ICRP
  name = G4_BRAIN_ICRP
  specific = 4
FEATURE [App::DocumentObjectGroupPython] C_element019  label="C_element : 4"  # scripted group (container) (typed FeaturePython)
  n = 4
  ref = C_element
FEATURE [App::DocumentObjectGroupPython] H_element018  label="H_element : 010"  # scripted group (container) (typed FeaturePython)
  n = 10
  ref = H_element
FEATURE [App::DocumentObjectGroupPython] G4_BUTANE  # scripted group (container) (typed FeaturePython)
  Dunit = g/cm3
  Dvalue = 0.00249343
  Group = -> [C_element019,H_element018]
  conduct = 2
  density = 1
  expand = 3
  formula = G4_BUTANE
  name = G4_BUTANE
  specific = 4
FEATURE [App::DocumentObjectGroupPython] C_element020  label="C_element : 008"  # scripted group (container) (typed FeaturePython)
  n = 4
  ref = C_element
FEATURE [App::DocumentObjectGroupPython] H_element019  label="H_element : 011"  # scripted group (container) (typed FeaturePython)
  n = 10
  ref = H_element
FEATURE [App::DocumentObjectGroupPython] O_element018  label="O_element : 007"  # scripted group (container) (typed FeaturePython)
  n = 1
  ref = O_element
FEATURE [App::DocumentObjectGroupPython] G4_N_BUTYL_ALCOHOL  label="G4_N-BUTYL_ALCOHOL"  # scripted group (container) (typed FeaturePython)
  Dunit = g/cm3
  Dvalue = 0.8098
  Group = -> [C_element020,H_element019,O_element018]
  conduct = 2
  density = 1
  expand = 3
  formula = G4_N-BUTYL_ALCOHOL
  name = G4_N-BUTYL_ALCOHOL
  specific = 4
FEATURE [App::DocumentObjectGroupPython] H_element020  label="H_element : 0.025"  # scripted group (container) (typed FeaturePython)
  n = 0.02468
FEATURE [App::DocumentObjectGroupPython] C_element021  label="C_element : 0.502"  # scripted group (container) (typed FeaturePython)
  n = 0.501611
FEATURE [App::DocumentObjectGroupPython] O_element019  label="O_element : 0.005"  # scripted group (container) (typed FeaturePython)
  n = 0.004527
FEATURE [App::DocumentObjectGroupPython] F_element004  label="F_element : 0.465"  # scripted group (container) (typed FeaturePython)
  n = 0.465209
FEATURE [App::DocumentObjectGroupPython] Si_element001  label="Si_element : 0.004"  # scripted group (container) (typed FeaturePython)
  n = 0.003973
FEATURE [App::DocumentObjectGroupPython] G4_C_552  label="G4_C-552"  # scripted group (container) (typed FeaturePython)
  Dunit = g/cm3
  Dvalue = 1.76
  Group = -> [H_element020,C_element021,O_element019,F_element004,Si_element001]
  conduct = 2
  density = 1
  expand = 3
  formula = G4_C-552
  name = G4_C-552
  specific = 4
FEATURE [App::DocumentObjectGroupPython] Cd_element001  label="Cd_element : 1"  # scripted group (container) (typed FeaturePython)
  n = 1
  ref = Cd_element
FEATURE [App::DocumentObjectGroupPython] Te_element001  label="Te_element : 1"  # scripted group (container) (typed FeaturePython)
  n = 1
  ref = Te_element
FEATURE [App::DocumentObjectGroupPython] G4_CADMIUM_TELLURIDE  # scripted group (container) (typed FeaturePython)
  Dunit = g/cm3
  Dvalue = 6.2
  Group = -> [Cd_element001,Te_element001]
  conduct = 2
  density = 1
  expand = 3
  formula = G4_CADMIUM_TELLURIDE
  name = G4_CADMIUM_TELLURIDE
  specific = 4
FEATURE [App::DocumentObjectGroupPython] Cd_element002  label="Cd_element : 002"  # scripted group (container) (typed FeaturePython)
  n = 1
  ref = Cd_element
FEATURE [App::DocumentObjectGroupPython] W_element001  label="W_element : 1"  # scripted group (container) (typed FeaturePython)
  n = 1
  ref = W_element
FEATURE [App::DocumentObjectGroupPython] O_element020  label="O_element : 008"  # scripted group (container) (typed FeaturePython)
  n = 4
  ref = O_element
FEATURE [App::DocumentObjectGroupPython] G4_CADMIUM_TUNGSTATE  # scripted group (container) (typed FeaturePython)
  Dunit = g/cm3
  Dvalue = 7.9
  Group = -> [Cd_element002,W_element001,O_element020]
  conduct = 2
  density = 1
  expand = 3
  formula = G4_CADMIUM_TUNGSTATE
  name = G4_CADMIUM_TUNGSTATE
  specific = 4
FEATURE [App::DocumentObjectGroupPython] Ca_element005  label="Ca_element : 1"  # scripted group (container) (typed FeaturePython)
  n = 1
  ref = Ca_element
FEATURE [App::DocumentObjectGroupPython] C_element022  label="C_element : 009"  # scripted group (container) (typed FeaturePython)
  n = 1
  ref = C_element
FEATURE [App::DocumentObjectGroupPython] O_element021  label="O_element : 009"  # scripted group (container) (typed FeaturePython)
  n = 3
  ref = O_element
FEATURE [App::DocumentObjectGroupPython] G4_CALCIUM_CARBONATE  # scripted group (container) (typed FeaturePython)
  Dunit = g/cm3
  Dvalue = 2.8
  Group = -> [Ca_element005,C_element022,O_element021]
  conduct = 2
  density = 1
  expand = 3
  formula = G4_CALCIUM_CARBONATE
  name = G4_CALCIUM_CARBONATE
  specific = 4
FEATURE [App::DocumentObjectGroupPython] Ca_element006  label="Ca_element : 002"  # scripted group (container) (typed FeaturePython)
  n = 1
  ref = Ca_element
FEATURE [App::DocumentObjectGroupPython] F_element005  label="F_element : 003"  # scripted group (container) (typed FeaturePython)
  n = 2
  ref = F_element
FEATURE [App::DocumentObjectGroupPython] G4_CALCIUM_FLUORIDE  # scripted group (container) (typed FeaturePython)
  Dunit = g/cm3
  Dvalue = 3.18
  Group = -> [Ca_element006,F_element005]
  conduct = 2
  density = 1
  expand = 3
  formula = G4_CALCIUM_FLUORIDE
  name = G4_CALCIUM_FLUORIDE
  specific = 4
FEATURE [App::DocumentObjectGroupPython] Ca_element007  label="Ca_element : 003"  # scripted group (container) (typed FeaturePython)
  n = 1
  ref = Ca_element
FEATURE [App::DocumentObjectGroupPython] O_element022  label="O_element : 010"  # scripted group (container) (typed FeaturePython)
  n = 1
  ref = O_element
FEATURE [App::DocumentObjectGroupPython] G4_CALCIUM_OXIDE  # scripted group (container) (typed FeaturePython)
  Dunit = g/cm3
  Dvalue = 3.3
  Group = -> [Ca_element007,O_element022]
  conduct = 2
  density = 1
  expand = 3
  formula = G4_CALCIUM_OXIDE
  name = G4_CALCIUM_OXIDE
  specific = 4
FEATURE [App::DocumentObjectGroupPython] Ca_element008  label="Ca_element : 004"  # scripted group (container) (typed FeaturePython)
  n = 1
  ref = Ca_element
FEATURE [App::DocumentObjectGroupPython] S_element007  label="S_element : 002"  # scripted group (container) (typed FeaturePython)
  n = 1
  ref = S_element
FEATURE [App::DocumentObjectGroupPython] O_element023  label="O_element : 011"  # scripted group (container) (typed FeaturePython)
  n = 4
  ref = O_element
FEATURE [App::DocumentObjectGroupPython] G4_CALCIUM_SULFATE  # scripted group (container) (typed FeaturePython)
  Dunit = g/cm3
  Dvalue = 2.96
  Group = -> [Ca_element008,S_element007,O_element023]
  conduct = 2
  density = 1
  expand = 3
  formula = G4_CALCIUM_SULFATE
  name = G4_CALCIUM_SULFATE
  specific = 4
FEATURE [App::DocumentObjectGroupPython] Ca_element009  label="Ca_element : 005"  # scripted group (container) (typed FeaturePython)
  n = 1
  ref = Ca_element
FEATURE [App::DocumentObjectGroupPython] W_element002  label="W_element : 002"  # scripted group (container) (typed FeaturePython)
  n = 1
  ref = W_element
FEATURE [App::DocumentObjectGroupPython] O_element024  label="O_element : 012"  # scripted group (container) (typed FeaturePython)
  n = 4
  ref = O_element
FEATURE [App::DocumentObjectGroupPython] G4_CALCIUM_TUNGSTATE  # scripted group (container) (typed FeaturePython)
  Dunit = g/cm3
  Dvalue = 6.062
  Group = -> [Ca_element009,W_element002,O_element024]
  conduct = 2
  density = 1
  expand = 3
  formula = G4_CALCIUM_TUNGSTATE
  name = G4_CALCIUM_TUNGSTATE
  specific = 4
FEATURE [App::DocumentObjectGroupPython] C_element023  label="C_element : 010"  # scripted group (container) (typed FeaturePython)
  n = 1
  ref = C_element
FEATURE [App::DocumentObjectGroupPython] O_element025  label="O_element : 013"  # scripted group (container) (typed FeaturePython)
  n = 2
  ref = O_element
FEATURE [App::DocumentObjectGroupPython] G4_CARBON_DIOXIDE  # scripted group (container) (typed FeaturePython)
  Dunit = g/cm3
  Dvalue = 0.00184212
  Group = -> [C_element023,O_element025]
  conduct = 2
  density = 1
  expand = 3
  formula = G4_CARBON_DIOXIDE
  name = G4_CARBON_DIOXIDE
  specific = 4
FEATURE [App::DocumentObjectGroupPython] C_element024  label="C_element : 011"  # scripted group (container) (typed FeaturePython)
  n = 1
  ref = C_element
FEATURE [App::DocumentObjectGroupPython] Cl_element004  label="Cl_element : 4"  # scripted group (container) (typed FeaturePython)
  n = 4
  ref = Cl_element
FEATURE [App::DocumentObjectGroupPython] G4_CARBON_TETRACHLORIDE  # scripted group (container) (typed FeaturePython)
  Dunit = g/cm3
  Dvalue = 1.594
  Group = -> [C_element024,Cl_element004]
  conduct = 2
  density = 1
  expand = 3
  formula = G4_CARBON_TETRACHLORIDE
  name = G4_CARBON_TETRACHLORIDE
  specific = 4
FEATURE [App::DocumentObjectGroupPython] C_element025  label="C_element : 012"  # scripted group (container) (typed FeaturePython)
  n = 6
  ref = C_element
FEATURE [App::DocumentObjectGroupPython] H_element021  label="H_element : 012"  # scripted group (container) (typed FeaturePython)
  n = 10
  ref = H_element
FEATURE [App::DocumentObjectGroupPython] O_element026  label="O_element : 5"  # scripted group (container) (typed FeaturePython)
  n = 5
  ref = O_element
FEATURE [App::DocumentObjectGroupPython] G4_CELLULOSE_CELLOPHANE  # scripted group (container) (typed FeaturePython)
  Dunit = g/cm3
  Dvalue = 1.42
  Group = -> [C_element025,H_element021,O_element026]
  conduct = 2
  density = 1
  expand = 3
  formula = G4_CELLULOSE_CELLOPHANE
  name = G4_CELLULOSE_CELLOPHANE
  specific = 4
FEATURE [App::DocumentObjectGroupPython] H_element022  label="H_element : 0.067"  # scripted group (container) (typed FeaturePython)
  n = 0.067125
FEATURE [App::DocumentObjectGroupPython] C_element026  label="C_element : 0.545"  # scripted group (container) (typed FeaturePython)
  n = 0.545403
FEATURE [App::DocumentObjectGroupPython] O_element027  label="O_element : 0.387"  # scripted group (container) (typed FeaturePython)
  n = 0.387472
FEATURE [App::DocumentObjectGroupPython] G4_CELLULOSE_BUTYRATE  # scripted group (container) (typed FeaturePython)
  Dunit = g/cm3
  Dvalue = 1.2
  Group = -> [H_element022,C_element026,O_element027]
  conduct = 2
  density = 1
  expand = 3
  formula = G4_CELLULOSE_BUTYRATE
  name = G4_CELLULOSE_BUTYRATE
  specific = 4
FEATURE [App::DocumentObjectGroupPython] H_element023  label="H_element : 0.029"  # scripted group (container) (typed FeaturePython)
  n = 0.029216
FEATURE [App::DocumentObjectGroupPython] C_element027  label="C_element : 0.271"  # scripted group (container) (typed FeaturePython)
  n = 0.271296
FEATURE [App::DocumentObjectGroupPython] N_element013  label="N_element : 0.121"  # scripted group (container) (typed FeaturePython)
  n = 0.121276
FEATURE [App::DocumentObjectGroupPython] O_element028  label="O_element : 0.578"  # scripted group (container) (typed FeaturePython)
  n = 0.578212
FEATURE [App::DocumentObjectGroupPython] G4_CELLULOSE_NITRATE  # scripted group (container) (typed FeaturePython)
  Dunit = g/cm3
  Dvalue = 1.49
  Group = -> [H_element023,C_element027,N_element013,O_element028]
  conduct = 2
  density = 1
  expand = 3
  formula = G4_CELLULOSE_NITRATE
  name = G4_CELLULOSE_NITRATE
  specific = 4
FEATURE [App::DocumentObjectGroupPython] H_element024  label="H_element : 0.108"  # scripted group (container) (typed FeaturePython)
  n = 0.107596
FEATURE [App::DocumentObjectGroupPython] N_element014  label="N_element : 0.001"  # scripted group (container) (typed FeaturePython)
  n = 0.0008
FEATURE [App::DocumentObjectGroupPython] O_element029  label="O_element : 0.875"  # scripted group (container) (typed FeaturePython)
  n = 0.874976
FEATURE [App::DocumentObjectGroupPython] S_element008  label="S_element : 0.015"  # scripted group (container) (typed FeaturePython)
  n = 0.014627
FEATURE [App::DocumentObjectGroupPython] Ce_element001  label="Ce_element : 0.002"  # scripted group (container) (typed FeaturePython)
  n = 0.002001
FEATURE [App::DocumentObjectGroupPython] G4_CERIC_SULFATE  # scripted group (container) (typed FeaturePython)
  Dunit = g/cm3
  Dvalue = 1.03
  Group = -> [H_element024,N_element014,O_element029,S_element008,Ce_element001]
  conduct = 2
  density = 1
  expand = 3
  formula = G4_CERIC_SULFATE
  name = G4_CERIC_SULFATE
  specific = 4
FEATURE [App::DocumentObjectGroupPython] Cs_element001  label="Cs_element : 1"  # scripted group (container) (typed FeaturePython)
  n = 1
  ref = Cs_element
FEATURE [App::DocumentObjectGroupPython] F_element006  label="F_element : 1"  # scripted group (container) (typed FeaturePython)
  n = 1
  ref = F_element
FEATURE [App::DocumentObjectGroupPython] G4_CESIUM_FLUORIDE  # scripted group (container) (typed FeaturePython)
  Dunit = g/cm3
  Dvalue = 4.115
  Group = -> [Cs_element001,F_element006]
  conduct = 2
  density = 1
  expand = 3
  formula = G4_CESIUM_FLUORIDE
  name = G4_CESIUM_FLUORIDE
  specific = 4
FEATURE [App::DocumentObjectGroupPython] Cs_element002  label="Cs_element : 002"  # scripted group (container) (typed FeaturePython)
  n = 1
  ref = Cs_element
FEATURE [App::DocumentObjectGroupPython] I_element001  label="I_element : 1"  # scripted group (container) (typed FeaturePython)
  n = 1
  ref = I_element
FEATURE [App::DocumentObjectGroupPython] G4_CESIUM_IODIDE  # scripted group (container) (typed FeaturePython)
  Dunit = g/cm3
  Dvalue = 4.51
  Group = -> [Cs_element002,I_element001]
  conduct = 2
  density = 1
  expand = 3
  formula = G4_CESIUM_IODIDE
  name = G4_CESIUM_IODIDE
  specific = 4
FEATURE [App::DocumentObjectGroupPython] C_element028  label="C_element : 013"  # scripted group (container) (typed FeaturePython)
  n = 6
  ref = C_element
FEATURE [App::DocumentObjectGroupPython] H_element025  label="H_element : 013"  # scripted group (container) (typed FeaturePython)
  n = 5
  ref = H_element
FEATURE [App::DocumentObjectGroupPython] Cl_element005  label="Cl_element : 1"  # scripted group (container) (typed FeaturePython)
  n = 1
  ref = Cl_element
FEATURE [App::DocumentObjectGroupPython] G4_CHLOROBENZENE  # scripted group (container) (typed FeaturePython)
  Dunit = g/cm3
  Dvalue = 1.1058
  Group = -> [C_element028,H_element025,Cl_element005]
  conduct = 2
  density = 1
  expand = 3
  formula = G4_CHLOROBENZENE
  name = G4_CHLOROBENZENE
  specific = 4
FEATURE [App::DocumentObjectGroupPython] C_element029  label="C_element : 014"  # scripted group (container) (typed FeaturePython)
  n = 1
  ref = C_element
FEATURE [App::DocumentObjectGroupPython] H_element026  label="H_element : 1"  # scripted group (container) (typed FeaturePython)
  n = 1
  ref = H_element
FEATURE [App::DocumentObjectGroupPython] Cl_element006  label="Cl_element : 3"  # scripted group (container) (typed FeaturePython)
  n = 3
  ref = Cl_element
FEATURE [App::DocumentObjectGroupPython] G4_CHLOROFORM  # scripted group (container) (typed FeaturePython)
  Dunit = g/cm3
  Dvalue = 1.4832
  Group = -> [C_element029,H_element026,Cl_element006]
  conduct = 2
  density = 1
  expand = 3
  formula = G4_CHLOROFORM
  name = G4_CHLOROFORM
  specific = 4
FEATURE [App::DocumentObjectGroupPython] H_element027  label="H_element : 0.010"  # scripted group (container) (typed FeaturePython)
  n = 0.01
FEATURE [App::DocumentObjectGroupPython] C_element030  label="C_element : 0.001"  # scripted group (container) (typed FeaturePython)
  n = 0.001
FEATURE [App::DocumentObjectGroupPython] O_element030  label="O_element : 0.529"  # scripted group (container) (typed FeaturePython)
  n = 0.529107
FEATURE [App::DocumentObjectGroupPython] Na_element005  label="Na_element : 0.016"  # scripted group (container) (typed FeaturePython)
  n = 0.016
FEATURE [App::DocumentObjectGroupPython] Mg_element003  label="Mg_element : 0.004"  # scripted group (container) (typed FeaturePython)
  n = 0.002
FEATURE [App::DocumentObjectGroupPython] Al_element002  label="Al_element : 0.034"  # scripted group (container) (typed FeaturePython)
  n = 0.033872
FEATURE [App::DocumentObjectGroupPython] Si_element002  label="Si_element : 0.337"  # scripted group (container) (typed FeaturePython)
  n = 0.337021
FEATURE [App::DocumentObjectGroupPython] K_element003  label="K_element : 0.013"  # scripted group (container) (typed FeaturePython)
  n = 0.013
FEATURE [App::DocumentObjectGroupPython] Ca_element010  label="Ca_element : 0.044"  # scripted group (container) (typed FeaturePython)
  n = 0.044
FEATURE [App::DocumentObjectGroupPython] Fe_element002  label="Fe_element : 0.014"  # scripted group (container) (typed FeaturePython)
  n = 0.014
FEATURE [App::DocumentObjectGroupPython] G4_CONCRETE  # scripted group (container) (typed FeaturePython)
  Dunit = g/cm3
  Dvalue = 2.3
  Group = -> [H_element027,C_element030,O_element030,Na_element005,Mg_element003,Al_element002,Si_element002,K_element003,Ca_element010,Fe_element002]
  conduct = 2
  density = 1
  expand = 3
  formula = G4_CONCRETE
  name = G4_CONCRETE
  specific = 4
FEATURE [App::DocumentObjectGroupPython] C_element031  label="C_element : 015"  # scripted group (container) (typed FeaturePython)
  n = 6
  ref = C_element
FEATURE [App::DocumentObjectGroupPython] H_element028  label="H_element : 12"  # scripted group (container) (typed FeaturePython)
  n = 12
  ref = H_element
FEATURE [App::DocumentObjectGroupPython] G4_CYCLOHEXANE  # scripted group (container) (typed FeaturePython)
  Dunit = g/cm3
  Dvalue = 0.779
  Group = -> [C_element031,H_element028]
  conduct = 2
  density = 1
  expand = 3
  formula = G4_CYCLOHEXANE
  name = G4_CYCLOHEXANE
  specific = 4
FEATURE [App::DocumentObjectGroupPython] C_element032  label="C_element : 016"  # scripted group (container) (typed FeaturePython)
  n = 6
  ref = C_element
FEATURE [App::DocumentObjectGroupPython] H_element029  label="H_element : 4"  # scripted group (container) (typed FeaturePython)
  n = 4
  ref = H_element
FEATURE [App::DocumentObjectGroupPython] Cl_element007  label="Cl_element : 2"  # scripted group (container) (typed FeaturePython)
  n = 2
  ref = Cl_element
FEATURE [App::DocumentObjectGroupPython] G4_1_2_DICHLOROBENZENE  label="G4_1.2-DICHLOROBENZENE"  # scripted group (container) (typed FeaturePython)
  Dunit = g/cm3
  Dvalue = 1.3048
  Group = -> [C_element032,H_element029,Cl_element007]
  conduct = 2
  density = 1
  expand = 3
  formula = G4_1.2-DICHLOROBENZENE
  name = G4_1.2-DICHLOROBENZENE
  specific = 4
FEATURE [App::DocumentObjectGroupPython] C_element033  label="C_element : 017"  # scripted group (container) (typed FeaturePython)
  n = 4
  ref = C_element
FEATURE [App::DocumentObjectGroupPython] H_element030  label="H_element : 8"  # scripted group (container) (typed FeaturePython)
  n = 8
  ref = H_element
FEATURE [App::DocumentObjectGroupPython] O_element031  label="O_element : 014"  # scripted group (container) (typed FeaturePython)
  n = 1
  ref = O_element
FEATURE [App::DocumentObjectGroupPython] Cl_element008  label="Cl_element : 005"  # scripted group (container) (typed FeaturePython)
  n = 2
  ref = Cl_element
FEATURE [App::DocumentObjectGroupPython] G4_DICHLORODIETHYL_ETHER  # scripted group (container) (typed FeaturePython)
  Dunit = g/cm3
  Dvalue = 1.2199
  Group = -> [C_element033,H_element030,O_element031,Cl_element008]
  conduct = 2
  density = 1
  expand = 3
  formula = G4_DICHLORODIETHYL_ETHER
  name = G4_DICHLORODIETHYL_ETHER
  specific = 4
FEATURE [App::DocumentObjectGroupPython] C_element034  label="C_element : 018"  # scripted group (container) (typed FeaturePython)
  n = 2
  ref = C_element
FEATURE [App::DocumentObjectGroupPython] H_element031  label="H_element : 014"  # scripted group (container) (typed FeaturePython)
  n = 4
  ref = H_element
FEATURE [App::DocumentObjectGroupPython] Cl_element009  label="Cl_element : 006"  # scripted group (container) (typed FeaturePython)
  n = 2
  ref = Cl_element
FEATURE [App::DocumentObjectGroupPython] G4_1_2_DICHLOROETHANE  label="G4_1.2-DICHLOROETHANE"  # scripted group (container) (typed FeaturePython)
  Dunit = g/cm3
  Dvalue = 1.2351
  Group = -> [C_element034,H_element031,Cl_element009]
  conduct = 2
  density = 1
  expand = 3
  formula = G4_1.2-DICHLOROETHANE
  name = G4_1.2-DICHLOROETHANE
  specific = 4
FEATURE [App::DocumentObjectGroupPython] C_element035  label="C_element : 019"  # scripted group (container) (typed FeaturePython)
  n = 4
  ref = C_element
FEATURE [App::DocumentObjectGroupPython] H_element032  label="H_element : 015"  # scripted group (container) (typed FeaturePython)
  n = 10
  ref = H_element
FEATURE [App::DocumentObjectGroupPython] O_element032  label="O_element : 015"  # scripted group (container) (typed FeaturePython)
  n = 1
  ref = O_element
FEATURE [App::DocumentObjectGroupPython] G4_DIETHYL_ETHER  # scripted group (container) (typed FeaturePython)
  Dunit = g/cm3
  Dvalue = 0.71378
  Group = -> [C_element035,H_element032,O_element032]
  conduct = 2
  density = 1
  expand = 3
  formula = G4_DIETHYL_ETHER
  name = G4_DIETHYL_ETHER
  specific = 4
FEATURE [App::DocumentObjectGroupPython] C_element036  label="C_element : 020"  # scripted group (container) (typed FeaturePython)
  n = 3
  ref = C_element
FEATURE [App::DocumentObjectGroupPython] H_element033  label="H_element : 016"  # scripted group (container) (typed FeaturePython)
  n = 7
  ref = H_element
FEATURE [App::DocumentObjectGroupPython] N_element015  label="N_element : 008"  # scripted group (container) (typed FeaturePython)
  n = 1
  ref = N_element
FEATURE [App::DocumentObjectGroupPython] O_element033  label="O_element : 016"  # scripted group (container) (typed FeaturePython)
  n = 1
  ref = O_element
FEATURE [App::DocumentObjectGroupPython] G4_N_N_DIMETHYL_FORMAMIDE  label="G4_N.N-DIMETHYL_FORMAMIDE"  # scripted group (container) (typed FeaturePython)
  Dunit = g/cm3
  Dvalue = 0.9487
  Group = -> [C_element036,H_element033,N_element015,O_element033]
  conduct = 2
  density = 1
  expand = 3
  formula = G4_N.N-DIMETHYL_FORMAMIDE
  name = G4_N.N-DIMETHYL_FORMAMIDE
  specific = 4
FEATURE [App::DocumentObjectGroupPython] C_element037  label="C_element : 021"  # scripted group (container) (typed FeaturePython)
  n = 2
  ref = C_element
FEATURE [App::DocumentObjectGroupPython] H_element034  label="H_element : 017"  # scripted group (container) (typed FeaturePython)
  n = 6
  ref = H_element
FEATURE [App::DocumentObjectGroupPython] O_element034  label="O_element : 017"  # scripted group (container) (typed FeaturePython)
  n = 1
  ref = O_element
FEATURE [App::DocumentObjectGroupPython] S_element009  label="S_element : 003"  # scripted group (container) (typed FeaturePython)
  n = 1
  ref = S_element
FEATURE [App::DocumentObjectGroupPython] G4_DIMETHYL_SULFOXIDE  # scripted group (container) (typed FeaturePython)
  Dunit = g/cm3
  Dvalue = 1.1014
  Group = -> [C_element037,H_element034,O_element034,S_element009]
  conduct = 2
  density = 1
  expand = 3
  formula = G4_DIMETHYL_SULFOXIDE
  name = G4_DIMETHYL_SULFOXIDE
  specific = 4
FEATURE [App::DocumentObjectGroupPython] C_element038  label="C_element : 022"  # scripted group (container) (typed FeaturePython)
  n = 2
  ref = C_element
FEATURE [App::DocumentObjectGroupPython] H_element035  label="H_element : 018"  # scripted group (container) (typed FeaturePython)
  n = 6
  ref = H_element
FEATURE [App::DocumentObjectGroupPython] G4_ETHANE  # scripted group (container) (typed FeaturePython)
  Dunit = g/cm3
  Dvalue = 0.00125324
  Group = -> [C_element038,H_element035]
  conduct = 2
  density = 1
  expand = 3
  formula = G4_ETHANE
  name = G4_ETHANE
  specific = 4
FEATURE [App::DocumentObjectGroupPython] C_element039  label="C_element : 023"  # scripted group (container) (typed FeaturePython)
  n = 2
  ref = C_element
FEATURE [App::DocumentObjectGroupPython] H_element036  label="H_element : 019"  # scripted group (container) (typed FeaturePython)
  n = 6
  ref = H_element
FEATURE [App::DocumentObjectGroupPython] O_element035  label="O_element : 018"  # scripted group (container) (typed FeaturePython)
  n = 1
  ref = O_element
FEATURE [App::DocumentObjectGroupPython] G4_ETHYL_ALCOHOL  # scripted group (container) (typed FeaturePython)
  Dunit = g/cm3
  Dvalue = 0.7893
  Group = -> [C_element039,H_element036,O_element035]
  conduct = 2
  density = 1
  expand = 3
  formula = G4_ETHYL_ALCOHOL
  name = G4_ETHYL_ALCOHOL
  specific = 4
FEATURE [App::DocumentObjectGroupPython] H_element037  label="H_element : 0.090"  # scripted group (container) (typed FeaturePython)
  n = 0.090027
FEATURE [App::DocumentObjectGroupPython] C_element040  label="C_element : 0.585"  # scripted group (container) (typed FeaturePython)
  n = 0.585182
FEATURE [App::DocumentObjectGroupPython] O_element036  label="O_element : 0.325"  # scripted group (container) (typed FeaturePython)
  n = 0.324791
FEATURE [App::DocumentObjectGroupPython] G4_ETHYL_CELLULOSE  # scripted group (container) (typed FeaturePython)
  Dunit = g/cm3
  Dvalue = 1.13
  Group = -> [H_element037,C_element040,O_element036]
  conduct = 2
  density = 1
  expand = 3
  formula = G4_ETHYL_CELLULOSE
  name = G4_ETHYL_CELLULOSE
  specific = 4
FEATURE [App::DocumentObjectGroupPython] C_element041  label="C_element : 024"  # scripted group (container) (typed FeaturePython)
  n = 2
  ref = C_element
FEATURE [App::DocumentObjectGroupPython] H_element038  label="H_element : 020"  # scripted group (container) (typed FeaturePython)
  n = 4
  ref = H_element
FEATURE [App::DocumentObjectGroupPython] G4_ETHYLENE  # scripted group (container) (typed FeaturePython)
  Dunit = g/cm3
  Dvalue = 0.00117497
  Group = -> [C_element041,H_element038]
  conduct = 2
  density = 1
  expand = 3
  formula = G4_ETHYLENE
  name = G4_ETHYLENE
  specific = 4
FEATURE [App::DocumentObjectGroupPython] H_element039  label="H_element : 0.096"  # scripted group (container) (typed FeaturePython)
  n = 0.096
FEATURE [App::DocumentObjectGroupPython] C_element042  label="C_element : 0.195"  # scripted group (container) (typed FeaturePython)
  n = 0.195
FEATURE [App::DocumentObjectGroupPython] N_element016  label="N_element : 0.057"  # scripted group (container) (typed FeaturePython)
  n = 0.057
FEATURE [App::DocumentObjectGroupPython] O_element037  label="O_element : 0.646"  # scripted group (container) (typed FeaturePython)
  n = 0.646
FEATURE [App::DocumentObjectGroupPython] Na_element006  label="Na_element : 0.017"  # scripted group (container) (typed FeaturePython)
  n = 0.001
FEATURE [App::DocumentObjectGroupPython] P_element005  label="P_element : 0.104"  # scripted group (container) (typed FeaturePython)
  n = 0.001
FEATURE [App::DocumentObjectGroupPython] S_element010  label="S_element : 0.016"  # scripted group (container) (typed FeaturePython)
  n = 0.003
FEATURE [App::DocumentObjectGroupPython] Cl_element010  label="Cl_element : 0.005"  # scripted group (container) (typed FeaturePython)
  n = 0.001
FEATURE [App::DocumentObjectGroupPython] G4_EYE_LENS_ICRP  # scripted group (container) (typed FeaturePython)
  Dunit = g/cm3
  Dvalue = 1.07
  Group = -> [H_element039,C_element042,N_element016,O_element037,Na_element006,P_element005,S_element010,Cl_element010]
  conduct = 2
  density = 1
  expand = 3
  formula = G4_EYE_LENS_ICRP
  name = G4_EYE_LENS_ICRP
  specific = 4
FEATURE [App::DocumentObjectGroupPython] Fe_element003  label="Fe_element : 2"  # scripted group (container) (typed FeaturePython)
  n = 2
  ref = Fe_element
FEATURE [App::DocumentObjectGroupPython] O_element038  label="O_element : 019"  # scripted group (container) (typed FeaturePython)
  n = 3
  ref = O_element
FEATURE [App::DocumentObjectGroupPython] G4_FERRIC_OXIDE  # scripted group (container) (typed FeaturePython)
  Dunit = g/cm3
  Dvalue = 5.2
  Group = -> [Fe_element003,O_element038]
  conduct = 2
  density = 1
  expand = 3
  formula = G4_FERRIC_OXIDE
  name = G4_FERRIC_OXIDE
  specific = 4
FEATURE [App::DocumentObjectGroupPython] Fe_element004  label="Fe_element : 1"  # scripted group (container) (typed FeaturePython)
  n = 1
  ref = Fe_element
FEATURE [App::DocumentObjectGroupPython] B_element003  label="B_element : 1"  # scripted group (container) (typed FeaturePython)
  n = 1
  ref = B_element
FEATURE [App::DocumentObjectGroupPython] G4_FERROBORIDE  # scripted group (container) (typed FeaturePython)
  Dunit = g/cm3
  Dvalue = 7.15
  Group = -> [Fe_element004,B_element003]
  conduct = 2
  density = 1
  expand = 3
  formula = G4_FERROBORIDE
  name = G4_FERROBORIDE
  specific = 4
FEATURE [App::DocumentObjectGroupPython] Fe_element005  label="Fe_element : 003"  # scripted group (container) (typed FeaturePython)
  n = 1
  ref = Fe_element
FEATURE [App::DocumentObjectGroupPython] O_element039  label="O_element : 020"  # scripted group (container) (typed FeaturePython)
  n = 1
  ref = O_element
FEATURE [App::DocumentObjectGroupPython] G4_FERROUS_OXIDE  # scripted group (container) (typed FeaturePython)
  Dunit = g/cm3
  Dvalue = 5.7
  Group = -> [Fe_element005,O_element039]
  conduct = 2
  density = 1
  expand = 3
  formula = G4_FERROUS_OXIDE
  name = G4_FERROUS_OXIDE
  specific = 4
FEATURE [App::DocumentObjectGroupPython] H_element040  label="H_element : 0.115"  # scripted group (container) (typed FeaturePython)
  n = 0.108259
FEATURE [App::DocumentObjectGroupPython] N_element017  label="N_element : 0.000"  # scripted group (container) (typed FeaturePython)
  n = 2.7e-05
FEATURE [App::DocumentObjectGroupPython] O_element040  label="O_element : 0.879"  # scripted group (container) (typed FeaturePython)
  n = 0.878636
FEATURE [App::DocumentObjectGroupPython] Na_element007  label="Na_element : 0.000"  # scripted group (container) (typed FeaturePython)
  n = 2.2e-05
FEATURE [App::DocumentObjectGroupPython] S_element011  label="S_element : 0.013"  # scripted group (container) (typed FeaturePython)
  n = 0.012968
FEATURE [App::DocumentObjectGroupPython] Cl_element011  label="Cl_element : 0.000"  # scripted group (container) (typed FeaturePython)
  n = 3.4e-05
FEATURE [App::DocumentObjectGroupPython] Fe_element006  label="Fe_element : 0.000"  # scripted group (container) (typed FeaturePython)
  n = 5.4e-05
FEATURE [App::DocumentObjectGroupPython] G4_FERROUS_SULFATE  # scripted group (container) (typed FeaturePython)
  Dunit = g/cm3
  Dvalue = 1.024
  Group = -> [H_element040,N_element017,O_element040,Na_element007,S_element011,Cl_element011,Fe_element006]
  conduct = 2
  density = 1
  expand = 3
  formula = G4_FERROUS_SULFATE
  name = G4_FERROUS_SULFATE
  specific = 4
FEATURE [App::DocumentObjectGroupPython] C_element043  label="C_element : 0.099"  # scripted group (container) (typed FeaturePython)
  n = 0.099335
FEATURE [App::DocumentObjectGroupPython] F_element007  label="F_element : 0.314"  # scripted group (container) (typed FeaturePython)
  n = 0.314247
FEATURE [App::DocumentObjectGroupPython] Cl_element012  label="Cl_element : 0.586"  # scripted group (container) (typed FeaturePython)
  n = 0.586418
FEATURE [App::DocumentObjectGroupPython] G4_FREON_12  label="G4_FREON-12"  # scripted group (container) (typed FeaturePython)
  Dunit = g/cm3
  Dvalue = 1.12
  Group = -> [C_element043,F_element007,Cl_element012]
  conduct = 2
  density = 1
  expand = 3
  formula = G4_FREON-12
  name = G4_FREON-12
  specific = 4
FEATURE [App::DocumentObjectGroupPython] C_element044  label="C_element : 0.057"  # scripted group (container) (typed FeaturePython)
  n = 0.057245
FEATURE [App::DocumentObjectGroupPython] F_element008  label="F_element : 0.181"  # scripted group (container) (typed FeaturePython)
  n = 0.181096
FEATURE [App::DocumentObjectGroupPython] Br_element001  label="Br_element : 0.762"  # scripted group (container) (typed FeaturePython)
  n = 0.761659
FEATURE [App::DocumentObjectGroupPython] G4_FREON_12B2  label="G4_FREON-12B2"  # scripted group (container) (typed FeaturePython)
  Dunit = g/cm3
  Dvalue = 1.8
  Group = -> [C_element044,F_element008,Br_element001]
  conduct = 2
  density = 1
  expand = 3
  formula = G4_FREON-12B2
  name = G4_FREON-12B2
  specific = 4
FEATURE [App::DocumentObjectGroupPython] C_element045  label="C_element : 0.115"  # scripted group (container) (typed FeaturePython)
  n = 0.114983
FEATURE [App::DocumentObjectGroupPython] F_element009  label="F_element : 0.546"  # scripted group (container) (typed FeaturePython)
  n = 0.545621
FEATURE [App::DocumentObjectGroupPython] Cl_element013  label="Cl_element : 0.339"  # scripted group (container) (typed FeaturePython)
  n = 0.339396
FEATURE [App::DocumentObjectGroupPython] G4_FREON_13  label="G4_FREON-13"  # scripted group (container) (typed FeaturePython)
  Dunit = g/cm3
  Dvalue = 0.95
  Group = -> [C_element045,F_element009,Cl_element013]
  conduct = 2
  density = 1
  expand = 3
  formula = G4_FREON-13
  name = G4_FREON-13
  specific = 4
FEATURE [App::DocumentObjectGroupPython] C_element046  label="C_element : 025"  # scripted group (container) (typed FeaturePython)
  n = 1
  ref = C_element
FEATURE [App::DocumentObjectGroupPython] F_element010  label="F_element : 3"  # scripted group (container) (typed FeaturePython)
  n = 3
  ref = F_element
FEATURE [App::DocumentObjectGroupPython] Br_element002  label="Br_element : 1"  # scripted group (container) (typed FeaturePython)
  n = 1
  ref = Br_element
FEATURE [App::DocumentObjectGroupPython] G4_FREON_13B1  label="G4_FREON-13B1"  # scripted group (container) (typed FeaturePython)
  Dunit = g/cm3
  Dvalue = 1.5
  Group = -> [C_element046,F_element010,Br_element002]
  conduct = 2
  density = 1
  expand = 3
  formula = G4_FREON-13B1
  name = G4_FREON-13B1
  specific = 4
FEATURE [App::DocumentObjectGroupPython] C_element047  label="C_element : 0.061"  # scripted group (container) (typed FeaturePython)
  n = 0.061309
FEATURE [App::DocumentObjectGroupPython] F_element011  label="F_element : 0.291"  # scripted group (container) (typed FeaturePython)
  n = 0.290924
FEATURE [App::DocumentObjectGroupPython] I_element002  label="I_element : 0.648"  # scripted group (container) (typed FeaturePython)
  n = 0.647767
FEATURE [App::DocumentObjectGroupPython] G4_FREON_13I1  label="G4_FREON-13I1"  # scripted group (container) (typed FeaturePython)
  Dunit = g/cm3
  Dvalue = 1.8
  Group = -> [C_element047,F_element011,I_element002]
  conduct = 2
  density = 1
  expand = 3
  formula = G4_FREON-13I1
  name = G4_FREON-13I1
  specific = 4
FEATURE [App::DocumentObjectGroupPython] Gd_element001  label="Gd_element : 2"  # scripted group (container) (typed FeaturePython)
  n = 2
  ref = Gd_element
FEATURE [App::DocumentObjectGroupPython] O_element041  label="O_element : 021"  # scripted group (container) (typed FeaturePython)
  n = 2
  ref = O_element
FEATURE [App::DocumentObjectGroupPython] S_element012  label="S_element : 004"  # scripted group (container) (typed FeaturePython)
  n = 1
  ref = S_element
FEATURE [App::DocumentObjectGroupPython] G4_GADOLINIUM_OXYSULFIDE  # scripted group (container) (typed FeaturePython)
  Dunit = g/cm3
  Dvalue = 7.44
  Group = -> [Gd_element001,O_element041,S_element012]
  conduct = 2
  density = 1
  expand = 3
  formula = G4_GADOLINIUM_OXYSULFIDE
  name = G4_GADOLINIUM_OXYSULFIDE
  specific = 4
FEATURE [App::DocumentObjectGroupPython] Ga_element001  label="Ga_element : 1"  # scripted group (container) (typed FeaturePython)
  n = 1
  ref = Ga_element
FEATURE [App::DocumentObjectGroupPython] As_element001  label="As_element : 1"  # scripted group (container) (typed FeaturePython)
  n = 1
  ref = As_element
FEATURE [App::DocumentObjectGroupPython] G4_GALLIUM_ARSENIDE  # scripted group (container) (typed FeaturePython)
  Dunit = g/cm3
  Dvalue = 5.31
  Group = -> [Ga_element001,As_element001]
  conduct = 2
  density = 1
  expand = 3
  formula = G4_GALLIUM_ARSENIDE
  name = G4_GALLIUM_ARSENIDE
  specific = 4
FEATURE [App::DocumentObjectGroupPython] H_element041  label="H_element : 0.081"  # scripted group (container) (typed FeaturePython)
  n = 0.08118
FEATURE [App::DocumentObjectGroupPython] C_element048  label="C_element : 0.416"  # scripted group (container) (typed FeaturePython)
  n = 0.41606
FEATURE [App::DocumentObjectGroupPython] N_element018  label="N_element : 0.111"  # scripted group (container) (typed FeaturePython)
  n = 0.11124
FEATURE [App::DocumentObjectGroupPython] O_element042  label="O_element : 0.381"  # scripted group (container) (typed FeaturePython)
  n = 0.38064
FEATURE [App::DocumentObjectGroupPython] S_element013  label="S_element : 0.011"  # scripted group (container) (typed FeaturePython)
  n = 0.01088
FEATURE [App::DocumentObjectGroupPython] G4_GEL_PHOTO_EMULSION  # scripted group (container) (typed FeaturePython)
  Dunit = g/cm3
  Dvalue = 1.2914
  Group = -> [H_element041,C_element048,N_element018,O_element042,S_element013]
  conduct = 2
  density = 1
  expand = 3
  formula = G4_GEL_PHOTO_EMULSION
  name = G4_GEL_PHOTO_EMULSION
  specific = 4
FEATURE [App::DocumentObjectGroupPython] B_element004  label="B_element : 0.040"  # scripted group (container) (typed FeaturePython)
  n = 0.0400639
FEATURE [App::DocumentObjectGroupPython] O_element043  label="O_element : 0.540"  # scripted group (container) (typed FeaturePython)
  n = 0.539561
FEATURE [App::DocumentObjectGroupPython] Na_element008  label="Na_element : 0.028"  # scripted group (container) (typed FeaturePython)
  n = 0.0281909
FEATURE [App::DocumentObjectGroupPython] Al_element003  label="Al_element : 0.012"  # scripted group (container) (typed FeaturePython)
  n = 0.011644
FEATURE [App::DocumentObjectGroupPython] Si_element003  label="Si_element : 0.377"  # scripted group (container) (typed FeaturePython)
  n = 0.377219
FEATURE [App::DocumentObjectGroupPython] K_element004  label="K_element : 0.014"  # scripted group (container) (typed FeaturePython)
  n = 0.00332099
FEATURE [App::DocumentObjectGroupPython] G4_Pyrex_Glass  # scripted group (container) (typed FeaturePython)
  Dunit = g/cm3
  Dvalue = 2.23
  Group = -> [B_element004,O_element043,Na_element008,Al_element003,Si_element003,K_element004]
  conduct = 2
  density = 1
  expand = 3
  formula = G4_Pyrex_Glass
  name = G4_Pyrex_Glass
  specific = 4
FEATURE [App::DocumentObjectGroupPython] O_element044  label="O_element : 0.156"  # scripted group (container) (typed FeaturePython)
  n = 0.156453
FEATURE [App::DocumentObjectGroupPython] Si_element004  label="Si_element : 0.081"  # scripted group (container) (typed FeaturePython)
  n = 0.080866
FEATURE [App::DocumentObjectGroupPython] Ti_element001  label="Ti_element : 0.008"  # scripted group (container) (typed FeaturePython)
  n = 0.008092
FEATURE [App::DocumentObjectGroupPython] As_element002  label="As_element : 0.003"  # scripted group (container) (typed FeaturePython)
  n = 0.002651
FEATURE [App::DocumentObjectGroupPython] Pb_element001  label="Pb_element : 0.752"  # scripted group (container) (typed FeaturePython)
  n = 0.751938
FEATURE [App::DocumentObjectGroupPython] G4_GLASS_LEAD  # scripted group (container) (typed FeaturePython)
  Dunit = g/cm3
  Dvalue = 6.22
  Group = -> [O_element044,Si_element004,Ti_element001,As_element002,Pb_element001]
  conduct = 2
  density = 1
  expand = 3
  formula = G4_GLASS_LEAD
  name = G4_GLASS_LEAD
  specific = 4
FEATURE [App::DocumentObjectGroupPython] O_element045  label="O_element : 0.460"  # scripted group (container) (typed FeaturePython)
  n = 0.4598
FEATURE [App::DocumentObjectGroupPython] Na_element009  label="Na_element : 0.096"  # scripted group (container) (typed FeaturePython)
  n = 0.0964411
FEATURE [App::DocumentObjectGroupPython] Si_element005  label="Si_element : 0.378"  # scripted group (container) (typed FeaturePython)
  n = 0.336553
FEATURE [App::DocumentObjectGroupPython] Ca_element011  label="Ca_element : 0.107"  # scripted group (container) (typed FeaturePython)
  n = 0.107205
FEATURE [App::DocumentObjectGroupPython] G4_GLASS_PLATE  # scripted group (container) (typed FeaturePython)
  Dunit = g/cm3
  Dvalue = 2.4
  Group = -> [O_element045,Na_element009,Si_element005,Ca_element011]
  conduct = 2
  density = 1
  expand = 3
  formula = G4_GLASS_PLATE
  name = G4_GLASS_PLATE
  specific = 4
FEATURE [App::DocumentObjectGroupPython] C_element049  label="C_element : 026"  # scripted group (container) (typed FeaturePython)
  n = 5
  ref = C_element
FEATURE [App::DocumentObjectGroupPython] H_element042  label="H_element : 021"  # scripted group (container) (typed FeaturePython)
  n = 10
  ref = H_element
FEATURE [App::DocumentObjectGroupPython] N_element019  label="N_element : 2"  # scripted group (container) (typed FeaturePython)
  n = 2
  ref = N_element
FEATURE [App::DocumentObjectGroupPython] O_element046  label="O_element : 022"  # scripted group (container) (typed FeaturePython)
  n = 3
  ref = O_element
FEATURE [App::DocumentObjectGroupPython] G4_GLUTAMINE  # scripted group (container) (typed FeaturePython)
  Dunit = g/cm3
  Dvalue = 1.46
  Group = -> [C_element049,H_element042,N_element019,O_element046]
  conduct = 2
  density = 1
  expand = 3
  formula = G4_GLUTAMINE
  name = G4_GLUTAMINE
  specific = 4
FEATURE [App::DocumentObjectGroupPython] C_element050  label="C_element : 027"  # scripted group (container) (typed FeaturePython)
  n = 3
  ref = C_element
FEATURE [App::DocumentObjectGroupPython] H_element043  label="H_element : 022"  # scripted group (container) (typed FeaturePython)
  n = 8
  ref = H_element
FEATURE [App::DocumentObjectGroupPython] O_element047  label="O_element : 023"  # scripted group (container) (typed FeaturePython)
  n = 3
  ref = O_element
FEATURE [App::DocumentObjectGroupPython] G4_GLYCEROL  # scripted group (container) (typed FeaturePython)
  Dunit = g/cm3
  Dvalue = 1.2613
  Group = -> [C_element050,H_element043,O_element047]
  conduct = 2
  density = 1
  expand = 3
  formula = G4_GLYCEROL
  name = G4_GLYCEROL
  specific = 4
FEATURE [App::DocumentObjectGroupPython] C_element051  label="C_element : 028"  # scripted group (container) (typed FeaturePython)
  n = 5
  ref = C_element
FEATURE [App::DocumentObjectGroupPython] H_element044  label="H_element : 023"  # scripted group (container) (typed FeaturePython)
  n = 5
  ref = H_element
FEATURE [App::DocumentObjectGroupPython] N_element020  label="N_element : 009"  # scripted group (container) (typed FeaturePython)
  n = 5
  ref = N_element
FEATURE [App::DocumentObjectGroupPython] O_element048  label="O_element : 024"  # scripted group (container) (typed FeaturePython)
  n = 1
  ref = O_element
FEATURE [App::DocumentObjectGroupPython] G4_GUANINE  # scripted group (container) (typed FeaturePython)
  Dunit = g/cm3
  Dvalue = 2.2
  Group = -> [C_element051,H_element044,N_element020,O_element048]
  conduct = 2
  density = 1
  expand = 3
  formula = G4_GUANINE
  name = G4_GUANINE
  specific = 4
FEATURE [App::DocumentObjectGroupPython] Ca_element012  label="Ca_element : 006"  # scripted group (container) (typed FeaturePython)
  n = 1
  ref = Ca_element
FEATURE [App::DocumentObjectGroupPython] S_element014  label="S_element : 005"  # scripted group (container) (typed FeaturePython)
  n = 1
  ref = S_element
FEATURE [App::DocumentObjectGroupPython] O_element049  label="O_element : 6"  # scripted group (container) (typed FeaturePython)
  n = 6
  ref = O_element
FEATURE [App::DocumentObjectGroupPython] H_element045  label="H_element : 024"  # scripted group (container) (typed FeaturePython)
  n = 4
  ref = H_element
FEATURE [App::DocumentObjectGroupPython] G4_GYPSUM  # scripted group (container) (typed FeaturePython)
  Dunit = g/cm3
  Dvalue = 2.32
  Group = -> [Ca_element012,S_element014,O_element049,H_element045]
  conduct = 2
  density = 1
  expand = 3
  formula = G4_GYPSUM
  name = G4_GYPSUM
  specific = 4
FEATURE [App::DocumentObjectGroupPython] C_element052  label="C_element : 7"  # scripted group (container) (typed FeaturePython)
  n = 7
  ref = C_element
FEATURE [App::DocumentObjectGroupPython] H_element046  label="H_element : 16"  # scripted group (container) (typed FeaturePython)
  n = 16
  ref = H_element
FEATURE [App::DocumentObjectGroupPython] G4_N_HEPTANE  label="G4_N-HEPTANE"  # scripted group (container) (typed FeaturePython)
  Dunit = g/cm3
  Dvalue = 0.68376
  Group = -> [C_element052,H_element046]
  conduct = 2
  density = 1
  expand = 3
  formula = G4_N-HEPTANE
  name = G4_N-HEPTANE
  specific = 4
FEATURE [App::DocumentObjectGroupPython] C_element053  label="C_element : 029"  # scripted group (container) (typed FeaturePython)
  n = 6
  ref = C_element
FEATURE [App::DocumentObjectGroupPython] H_element047  label="H_element : 14"  # scripted group (container) (typed FeaturePython)
  n = 14
  ref = H_element
FEATURE [App::DocumentObjectGroupPython] G4_N_HEXANE  label="G4_N-HEXANE"  # scripted group (container) (typed FeaturePython)
  Dunit = g/cm3
  Dvalue = 0.6603
  Group = -> [C_element053,H_element047]
  conduct = 2
  density = 1
  expand = 3
  formula = G4_N-HEXANE
  name = G4_N-HEXANE
  specific = 4
FEATURE [App::DocumentObjectGroupPython] C_element054  label="C_element : 22"  # scripted group (container) (typed FeaturePython)
  n = 22
  ref = C_element
FEATURE [App::DocumentObjectGroupPython] H_element048  label="H_element : 025"  # scripted group (container) (typed FeaturePython)
  n = 10
  ref = H_element
FEATURE [App::DocumentObjectGroupPython] N_element021  label="N_element : 010"  # scripted group (container) (typed FeaturePython)
  n = 2
  ref = N_element
FEATURE [App::DocumentObjectGroupPython] O_element050  label="O_element : 025"  # scripted group (container) (typed FeaturePython)
  n = 5
  ref = O_element
FEATURE [App::DocumentObjectGroupPython] G4_KAPTON  # scripted group (container) (typed FeaturePython)
  Dunit = g/cm3
  Dvalue = 1.42
  Group = -> [C_element054,H_element048,N_element021,O_element050]
  conduct = 2
  density = 1
  expand = 3
  formula = G4_KAPTON
  name = G4_KAPTON
  specific = 4
FEATURE [App::DocumentObjectGroupPython] La_element001  label="La_element : 1"  # scripted group (container) (typed FeaturePython)
  n = 1
  ref = La_element
FEATURE [App::DocumentObjectGroupPython] Br_element003  label="Br_element : 002"  # scripted group (container) (typed FeaturePython)
  n = 1
  ref = Br_element
FEATURE [App::DocumentObjectGroupPython] O_element051  label="O_element : 026"  # scripted group (container) (typed FeaturePython)
  n = 1
  ref = O_element
FEATURE [App::DocumentObjectGroupPython] G4_LANTHANUM_OXYBROMIDE  # scripted group (container) (typed FeaturePython)
  Dunit = g/cm3
  Dvalue = 6.28
  Group = -> [La_element001,Br_element003,O_element051]
  conduct = 2
  density = 1
  expand = 3
  formula = G4_LANTHANUM_OXYBROMIDE
  name = G4_LANTHANUM_OXYBROMIDE
  specific = 4
FEATURE [App::DocumentObjectGroupPython] La_element002  label="La_element : 2"  # scripted group (container) (typed FeaturePython)
  n = 2
  ref = La_element
FEATURE [App::DocumentObjectGroupPython] O_element052  label="O_element : 027"  # scripted group (container) (typed FeaturePython)
  n = 2
  ref = O_element
FEATURE [App::DocumentObjectGroupPython] S_element015  label="S_element : 006"  # scripted group (container) (typed FeaturePython)
  n = 1
  ref = S_element
FEATURE [App::DocumentObjectGroupPython] G4_LANTHANUM_OXYSULFIDE  # scripted group (container) (typed FeaturePython)
  Dunit = g/cm3
  Dvalue = 5.86
  Group = -> [La_element002,O_element052,S_element015]
  conduct = 2
  density = 1
  expand = 3
  formula = G4_LANTHANUM_OXYSULFIDE
  name = G4_LANTHANUM_OXYSULFIDE
  specific = 4
FEATURE [App::DocumentObjectGroupPython] O_element053  label="O_element : 0.072"  # scripted group (container) (typed FeaturePython)
  n = 0.071682
FEATURE [App::DocumentObjectGroupPython] Pb_element002  label="Pb_element : 0.928"  # scripted group (container) (typed FeaturePython)
  n = 0.928318
FEATURE [App::DocumentObjectGroupPython] G4_LEAD_OXIDE  # scripted group (container) (typed FeaturePython)
  Dunit = g/cm3
  Dvalue = 9.53
  Group = -> [O_element053,Pb_element002]
  conduct = 2
  density = 1
  expand = 3
  formula = G4_LEAD_OXIDE
  name = G4_LEAD_OXIDE
  specific = 4
FEATURE [App::DocumentObjectGroupPython] Li_element001  label="Li_element : 1"  # scripted group (container) (typed FeaturePython)
  n = 1
  ref = Li_element
FEATURE [App::DocumentObjectGroupPython] N_element022  label="N_element : 011"  # scripted group (container) (typed FeaturePython)
  n = 1
  ref = N_element
FEATURE [App::DocumentObjectGroupPython] H_element049  label="H_element : 026"  # scripted group (container) (typed FeaturePython)
  n = 2
  ref = H_element
FEATURE [App::DocumentObjectGroupPython] G4_LITHIUM_AMIDE  # scripted group (container) (typed FeaturePython)
  Dunit = g/cm3
  Dvalue = 1.178
  Group = -> [Li_element001,N_element022,H_element049]
  conduct = 2
  density = 1
  expand = 3
  formula = G4_LITHIUM_AMIDE
  name = G4_LITHIUM_AMIDE
  specific = 4
FEATURE [App::DocumentObjectGroupPython] Li_element002  label="Li_element : 2"  # scripted group (container) (typed FeaturePython)
  n = 2
  ref = Li_element
FEATURE [App::DocumentObjectGroupPython] C_element055  label="C_element : 030"  # scripted group (container) (typed FeaturePython)
  n = 1
  ref = C_element
FEATURE [App::DocumentObjectGroupPython] O_element054  label="O_element : 028"  # scripted group (container) (typed FeaturePython)
  n = 3
  ref = O_element
FEATURE [App::DocumentObjectGroupPython] G4_LITHIUM_CARBONATE  # scripted group (container) (typed FeaturePython)
  Dunit = g/cm3
  Dvalue = 2.11
  Group = -> [Li_element002,C_element055,O_element054]
  conduct = 2
  density = 1
  expand = 3
  formula = G4_LITHIUM_CARBONATE
  name = G4_LITHIUM_CARBONATE
  specific = 4
FEATURE [App::DocumentObjectGroupPython] Li_element003  label="Li_element : 003"  # scripted group (container) (typed FeaturePython)
  n = 1
  ref = Li_element
FEATURE [App::DocumentObjectGroupPython] F_element012  label="F_element : 004"  # scripted group (container) (typed FeaturePython)
  n = 1
  ref = F_element
FEATURE [App::DocumentObjectGroupPython] G4_LITHIUM_FLUORIDE  # scripted group (container) (typed FeaturePython)
  Dunit = g/cm3
  Dvalue = 2.635
  Group = -> [Li_element003,F_element012]
  conduct = 2
  density = 1
  expand = 3
  formula = G4_LITHIUM_FLUORIDE
  name = G4_LITHIUM_FLUORIDE
  specific = 4
FEATURE [App::DocumentObjectGroupPython] Li_element004  label="Li_element : 004"  # scripted group (container) (typed FeaturePython)
  n = 1
  ref = Li_element
FEATURE [App::DocumentObjectGroupPython] H_element050  label="H_element : 027"  # scripted group (container) (typed FeaturePython)
  n = 1
  ref = H_element
FEATURE [App::DocumentObjectGroupPython] G4_LITHIUM_HYDRIDE  # scripted group (container) (typed FeaturePython)
  Dunit = g/cm3
  Dvalue = 0.82
  Group = -> [Li_element004,H_element050]
  conduct = 2
  density = 1
  expand = 3
  formula = G4_LITHIUM_HYDRIDE
  name = G4_LITHIUM_HYDRIDE
  specific = 4
FEATURE [App::DocumentObjectGroupPython] Li_element005  label="Li_element : 005"  # scripted group (container) (typed FeaturePython)
  n = 1
  ref = Li_element
FEATURE [App::DocumentObjectGroupPython] I_element003  label="I_element : 002"  # scripted group (container) (typed FeaturePython)
  n = 1
  ref = I_element
FEATURE [App::DocumentObjectGroupPython] G4_LITHIUM_IODIDE  # scripted group (container) (typed FeaturePython)
  Dunit = g/cm3
  Dvalue = 3.494
  Group = -> [Li_element005,I_element003]
  conduct = 2
  density = 1
  expand = 3
  formula = G4_LITHIUM_IODIDE
  name = G4_LITHIUM_IODIDE
  specific = 4
FEATURE [App::DocumentObjectGroupPython] Li_element006  label="Li_element : 006"  # scripted group (container) (typed FeaturePython)
  n = 2
  ref = Li_element
FEATURE [App::DocumentObjectGroupPython] O_element055  label="O_element : 029"  # scripted group (container) (typed FeaturePython)
  n = 1
  ref = O_element
FEATURE [App::DocumentObjectGroupPython] G4_LITHIUM_OXIDE  # scripted group (container) (typed FeaturePython)
  Dunit = g/cm3
  Dvalue = 2.013
  Group = -> [Li_element006,O_element055]
  conduct = 2
  density = 1
  expand = 3
  formula = G4_LITHIUM_OXIDE
  name = G4_LITHIUM_OXIDE
  specific = 4
FEATURE [App::DocumentObjectGroupPython] Li_element007  label="Li_element : 007"  # scripted group (container) (typed FeaturePython)
  n = 2
  ref = Li_element
FEATURE [App::DocumentObjectGroupPython] B_element005  label="B_element : 005"  # scripted group (container) (typed FeaturePython)
  n = 4
  ref = B_element
FEATURE [App::DocumentObjectGroupPython] O_element056  label="O_element : 7"  # scripted group (container) (typed FeaturePython)
  n = 7
  ref = O_element
FEATURE [App::DocumentObjectGroupPython] G4_LITHIUM_TETRABORATE  # scripted group (container) (typed FeaturePython)
  Dunit = g/cm3
  Dvalue = 2.44
  Group = -> [Li_element007,B_element005,O_element056]
  conduct = 2
  density = 1
  expand = 3
  formula = G4_LITHIUM_TETRABORATE
  name = G4_LITHIUM_TETRABORATE
  specific = 4
FEATURE [App::DocumentObjectGroupPython] H_element051  label="H_element : 0.105"  # scripted group (container) (typed FeaturePython)
  n = 0.105
FEATURE [App::DocumentObjectGroupPython] C_element056  label="C_element : 0.083"  # scripted group (container) (typed FeaturePython)
  n = 0.083
FEATURE [App::DocumentObjectGroupPython] N_element023  label="N_element : 0.023"  # scripted group (container) (typed FeaturePython)
  n = 0.023
FEATURE [App::DocumentObjectGroupPython] O_element057  label="O_element : 0.779"  # scripted group (container) (typed FeaturePython)
  n = 0.779
FEATURE [App::DocumentObjectGroupPython] Na_element010  label="Na_element : 0.097"  # scripted group (container) (typed FeaturePython)
  n = 0.002
FEATURE [App::DocumentObjectGroupPython] P_element006  label="P_element : 0.105"  # scripted group (container) (typed FeaturePython)
  n = 0.001
FEATURE [App::DocumentObjectGroupPython] S_element016  label="S_element : 0.017"  # scripted group (container) (typed FeaturePython)
  n = 0.002
FEATURE [App::DocumentObjectGroupPython] Cl_element014  label="Cl_element : 0.587"  # scripted group (container) (typed FeaturePython)
  n = 0.003
FEATURE [App::DocumentObjectGroupPython] K_element005  label="K_element : 0.015"  # scripted group (container) (typed FeaturePython)
  n = 0.002
FEATURE [App::DocumentObjectGroupPython] G4_LUNG_ICRP  # scripted group (container) (typed FeaturePython)
  Dunit = g/cm3
  Dvalue = 1.04
  Group = -> [H_element051,C_element056,N_element023,O_element057,Na_element010,P_element006,S_element016,Cl_element014,K_element005]
  conduct = 2
  density = 1
  expand = 3
  formula = G4_LUNG_ICRP
  name = G4_LUNG_ICRP
  specific = 4
FEATURE [App::DocumentObjectGroupPython] H_element052  label="H_element : 0.116"  # scripted group (container) (typed FeaturePython)
  n = 0.114318
FEATURE [App::DocumentObjectGroupPython] C_element057  label="C_element : 0.656"  # scripted group (container) (typed FeaturePython)
  n = 0.655824
FEATURE [App::DocumentObjectGroupPython] O_element058  label="O_element : 0.092"  # scripted group (container) (typed FeaturePython)
  n = 0.0921831
FEATURE [App::DocumentObjectGroupPython] Mg_element004  label="Mg_element : 0.135"  # scripted group (container) (typed FeaturePython)
  n = 0.134792
FEATURE [App::DocumentObjectGroupPython] Ca_element013  label="Ca_element : 0.003"  # scripted group (container) (typed FeaturePython)
  n = 0.002883
FEATURE [App::DocumentObjectGroupPython] G4_M3_WAX  # scripted group (container) (typed FeaturePython)
  Dunit = g/cm3
  Dvalue = 1.05
  Group = -> [H_element052,C_element057,O_element058,Mg_element004,Ca_element013]
  conduct = 2
  density = 1
  expand = 3
  formula = G4_M3_WAX
  name = G4_M3_WAX
  specific = 4
FEATURE [App::DocumentObjectGroupPython] Mg_element005  label="Mg_element : 1"  # scripted group (container) (typed FeaturePython)
  n = 1
  ref = Mg_element
FEATURE [App::DocumentObjectGroupPython] C_element058  label="C_element : 031"  # scripted group (container) (typed FeaturePython)
  n = 1
  ref = C_element
FEATURE [App::DocumentObjectGroupPython] O_element059  label="O_element : 030"  # scripted group (container) (typed FeaturePython)
  n = 3
  ref = O_element
FEATURE [App::DocumentObjectGroupPython] G4_MAGNESIUM_CARBONATE  # scripted group (container) (typed FeaturePython)
  Dunit = g/cm3
  Dvalue = 2.958
  Group = -> [Mg_element005,C_element058,O_element059]
  conduct = 2
  density = 1
  expand = 3
  formula = G4_MAGNESIUM_CARBONATE
  name = G4_MAGNESIUM_CARBONATE
  specific = 4
FEATURE [App::DocumentObjectGroupPython] Mg_element006  label="Mg_element : 002"  # scripted group (container) (typed FeaturePython)
  n = 1
  ref = Mg_element
FEATURE [App::DocumentObjectGroupPython] F_element013  label="F_element : 005"  # scripted group (container) (typed FeaturePython)
  n = 2
  ref = F_element
FEATURE [App::DocumentObjectGroupPython] G4_MAGNESIUM_FLUORIDE  # scripted group (container) (typed FeaturePython)
  Dunit = g/cm3
  Dvalue = 3
  Group = -> [Mg_element006,F_element013]
  conduct = 2
  density = 1
  expand = 3
  formula = G4_MAGNESIUM_FLUORIDE
  name = G4_MAGNESIUM_FLUORIDE
  specific = 4
FEATURE [App::DocumentObjectGroupPython] Mg_element007  label="Mg_element : 003"  # scripted group (container) (typed FeaturePython)
  n = 1
  ref = Mg_element
FEATURE [App::DocumentObjectGroupPython] O_element060  label="O_element : 031"  # scripted group (container) (typed FeaturePython)
  n = 1
  ref = O_element
FEATURE [App::DocumentObjectGroupPython] G4_MAGNESIUM_OXIDE  # scripted group (container) (typed FeaturePython)
  Dunit = g/cm3
  Dvalue = 3.58
  Group = -> [Mg_element007,O_element060]
  conduct = 2
  density = 1
  expand = 3
  formula = G4_MAGNESIUM_OXIDE
  name = G4_MAGNESIUM_OXIDE
  specific = 4
FEATURE [App::DocumentObjectGroupPython] Mg_element008  label="Mg_element : 004"  # scripted group (container) (typed FeaturePython)
  n = 1
  ref = Mg_element
FEATURE [App::DocumentObjectGroupPython] B_element006  label="B_element : 006"  # scripted group (container) (typed FeaturePython)
  n = 4
  ref = B_element
FEATURE [App::DocumentObjectGroupPython] O_element061  label="O_element : 032"  # scripted group (container) (typed FeaturePython)
  n = 7
  ref = O_element
FEATURE [App::DocumentObjectGroupPython] G4_MAGNESIUM_TETRABORATE  # scripted group (container) (typed FeaturePython)
  Dunit = g/cm3
  Dvalue = 2.53
  Group = -> [Mg_element008,B_element006,O_element061]
  conduct = 2
  density = 1
  expand = 3
  formula = G4_MAGNESIUM_TETRABORATE
  name = G4_MAGNESIUM_TETRABORATE
  specific = 4
FEATURE [App::DocumentObjectGroupPython] Hg_element001  label="Hg_element : 1"  # scripted group (container) (typed FeaturePython)
  n = 1
  ref = Hg_element
FEATURE [App::DocumentObjectGroupPython] I_element004  label="I_element : 2"  # scripted group (container) (typed FeaturePython)
  n = 2
  ref = I_element
FEATURE [App::DocumentObjectGroupPython] G4_MERCURIC_IODIDE  # scripted group (container) (typed FeaturePython)
  Dunit = g/cm3
  Dvalue = 6.36
  Group = -> [Hg_element001,I_element004]
  conduct = 2
  density = 1
  expand = 3
  formula = G4_MERCURIC_IODIDE
  name = G4_MERCURIC_IODIDE
  specific = 4
FEATURE [App::DocumentObjectGroupPython] C_element059  label="C_element : 032"  # scripted group (container) (typed FeaturePython)
  n = 1
  ref = C_element
FEATURE [App::DocumentObjectGroupPython] H_element053  label="H_element : 028"  # scripted group (container) (typed FeaturePython)
  n = 4
  ref = H_element
FEATURE [App::DocumentObjectGroupPython] G4_METHANE  # scripted group (container) (typed FeaturePython)
  Dunit = g/cm3
  Dvalue = 0.000667151
  Group = -> [C_element059,H_element053]
  conduct = 2
  density = 1
  expand = 3
  formula = G4_METHANE
  name = G4_METHANE
  specific = 4
FEATURE [App::DocumentObjectGroupPython] C_element060  label="C_element : 033"  # scripted group (container) (typed FeaturePython)
  n = 1
  ref = C_element
FEATURE [App::DocumentObjectGroupPython] H_element054  label="H_element : 029"  # scripted group (container) (typed FeaturePython)
  n = 4
  ref = H_element
FEATURE [App::DocumentObjectGroupPython] O_element062  label="O_element : 033"  # scripted group (container) (typed FeaturePython)
  n = 1
  ref = O_element
FEATURE [App::DocumentObjectGroupPython] G4_METHANOL  # scripted group (container) (typed FeaturePython)
  Dunit = g/cm3
  Dvalue = 0.7914
  Group = -> [C_element060,H_element054,O_element062]
  conduct = 2
  density = 1
  expand = 3
  formula = G4_METHANOL
  name = G4_METHANOL
  specific = 4
FEATURE [App::DocumentObjectGroupPython] H_element055  label="H_element : 0.134"  # scripted group (container) (typed FeaturePython)
  n = 0.13404
FEATURE [App::DocumentObjectGroupPython] C_element061  label="C_element : 0.778"  # scripted group (container) (typed FeaturePython)
  n = 0.77796
FEATURE [App::DocumentObjectGroupPython] O_element063  label="O_element : 0.035"  # scripted group (container) (typed FeaturePython)
  n = 0.03502
FEATURE [App::DocumentObjectGroupPython] Mg_element009  label="Mg_element : 0.039"  # scripted group (container) (typed FeaturePython)
  n = 0.038594
FEATURE [App::DocumentObjectGroupPython] Ti_element002  label="Ti_element : 0.014"  # scripted group (container) (typed FeaturePython)
  n = 0.014386
FEATURE [App::DocumentObjectGroupPython] G4_MIX_D_WAX  # scripted group (container) (typed FeaturePython)
  Dunit = g/cm3
  Dvalue = 0.99
  Group = -> [H_element055,C_element061,O_element063,Mg_element009,Ti_element002]
  conduct = 2
  density = 1
  expand = 3
  formula = G4_MIX_D_WAX
  name = G4_MIX_D_WAX
  specific = 4
FEATURE [App::DocumentObjectGroupPython] H_element056  label="H_element : 0.135"  # scripted group (container) (typed FeaturePython)
  n = 0.081192
FEATURE [App::DocumentObjectGroupPython] C_element062  label="C_element : 0.583"  # scripted group (container) (typed FeaturePython)
  n = 0.583442
FEATURE [App::DocumentObjectGroupPython] N_element024  label="N_element : 0.018"  # scripted group (container) (typed FeaturePython)
  n = 0.017798
FEATURE [App::DocumentObjectGroupPython] O_element064  label="O_element : 0.186"  # scripted group (container) (typed FeaturePython)
  n = 0.186381
FEATURE [App::DocumentObjectGroupPython] Mg_element010  label="Mg_element : 0.130"  # scripted group (container) (typed FeaturePython)
  n = 0.130287
FEATURE [App::DocumentObjectGroupPython] Cl_element015  label="Cl_element : 0.588"  # scripted group (container) (typed FeaturePython)
  n = 0.0009
FEATURE [App::DocumentObjectGroupPython] G4_MS20_TISSUE  # scripted group (container) (typed FeaturePython)
  Dunit = g/cm3
  Dvalue = 1
  Group = -> [H_element056,C_element062,N_element024,O_element064,Mg_element010,Cl_element015]
  conduct = 2
  density = 1
  expand = 3
  formula = G4_MS20_TISSUE
  name = G4_MS20_TISSUE
  specific = 4
FEATURE [App::DocumentObjectGroupPython] H_element057  label="H_element : 0.136"  # scripted group (container) (typed FeaturePython)
  n = 0.102
FEATURE [App::DocumentObjectGroupPython] C_element063  label="C_element : 0.143"  # scripted group (container) (typed FeaturePython)
  n = 0.143
FEATURE [App::DocumentObjectGroupPython] N_element025  label="N_element : 0.034"  # scripted group (container) (typed FeaturePython)
  n = 0.034
FEATURE [App::DocumentObjectGroupPython] O_element065  label="O_element : 0.710"  # scripted group (container) (typed FeaturePython)
  n = 0.71
FEATURE [App::DocumentObjectGroupPython] Na_element011  label="Na_element : 0.098"  # scripted group (container) (typed FeaturePython)
  n = 0.001
FEATURE [App::DocumentObjectGroupPython] P_element007  label="P_element : 0.002"  # scripted group (container) (typed FeaturePython)
  n = 0.002
FEATURE [App::DocumentObjectGroupPython] S_element017  label="S_element : 0.018"  # scripted group (container) (typed FeaturePython)
  n = 0.003
FEATURE [App::DocumentObjectGroupPython] Cl_element016  label="Cl_element : 0.589"  # scripted group (container) (typed FeaturePython)
  n = 0.001
FEATURE [App::DocumentObjectGroupPython] K_element006  label="K_element : 0.004"  # scripted group (container) (typed FeaturePython)
  n = 0.004
FEATURE [App::DocumentObjectGroupPython] G4_MUSCLE_SKELETAL_ICRP  # scripted group (container) (typed FeaturePython)
  Dunit = g/cm3
  Dvalue = 1.05
  Group = -> [H_element057,C_element063,N_element025,O_element065,Na_element011,P_element007,S_element017,Cl_element016,K_element006]
  conduct = 2
  density = 1
  expand = 3
  formula = G4_MUSCLE_SKELETAL_ICRP
  name = G4_MUSCLE_SKELETAL_ICRP
  specific = 4
FEATURE [App::DocumentObjectGroupPython] H_element058  label="H_element : 0.137"  # scripted group (container) (typed FeaturePython)
  n = 0.102102
FEATURE [App::DocumentObjectGroupPython] C_element064  label="C_element : 0.123"  # scripted group (container) (typed FeaturePython)
  n = 0.123123
FEATURE [App::DocumentObjectGroupPython] N_element026  label="N_element : 0.756"  # scripted group (container) (typed FeaturePython)
  n = 0.035035
FEATURE [App::DocumentObjectGroupPython] O_element066  label="O_element : 0.730"  # scripted group (container) (typed FeaturePython)
  n = 0.72973
FEATURE [App::DocumentObjectGroupPython] Na_element012  label="Na_element : 0.099"  # scripted group (container) (typed FeaturePython)
  n = 0.001001
FEATURE [App::DocumentObjectGroupPython] P_element008  label="P_element : 0.106"  # scripted group (container) (typed FeaturePython)
  n = 0.002002
FEATURE [App::DocumentObjectGroupPython] S_element018  label="S_element : 0.019"  # scripted group (container) (typed FeaturePython)
  n = 0.004004
FEATURE [App::DocumentObjectGroupPython] K_element007  label="K_element : 0.016"  # scripted group (container) (typed FeaturePython)
  n = 0.003003
FEATURE [App::DocumentObjectGroupPython] G4_MUSCLE_STRIATED_ICRU  # scripted group (container) (typed FeaturePython)
  Dunit = g/cm3
  Dvalue = 1.04
  Group = -> [H_element058,C_element064,N_element026,O_element066,Na_element012,P_element008,S_element018,K_element007]
  conduct = 2
  density = 1
  expand = 3
  formula = G4_MUSCLE_STRIATED_ICRU
  name = G4_MUSCLE_STRIATED_ICRU
  specific = 4
FEATURE [App::DocumentObjectGroupPython] H_element059  label="H_element : 0.098"  # scripted group (container) (typed FeaturePython)
  n = 0.0982341
FEATURE [App::DocumentObjectGroupPython] C_element065  label="C_element : 0.156"  # scripted group (container) (typed FeaturePython)
  n = 0.156214
FEATURE [App::DocumentObjectGroupPython] N_element027  label="N_element : 0.757"  # scripted group (container) (typed FeaturePython)
  n = 0.035451
FEATURE [App::DocumentObjectGroupPython] O_element067  label="O_element : 0.880"  # scripted group (container) (typed FeaturePython)
  n = 0.710101
FEATURE [App::DocumentObjectGroupPython] G4_MUSCLE_WITH_SUCROSE  # scripted group (container) (typed FeaturePython)
  Dunit = g/cm3
  Dvalue = 1.11
  Group = -> [H_element059,C_element065,N_element027,O_element067]
  conduct = 2
  density = 1
  expand = 3
  formula = G4_MUSCLE_WITH_SUCROSE
  name = G4_MUSCLE_WITH_SUCROSE
  specific = 4
FEATURE [App::DocumentObjectGroupPython] H_element060  label="H_element : 0.138"  # scripted group (container) (typed FeaturePython)
  n = 0.101969
FEATURE [App::DocumentObjectGroupPython] C_element066  label="C_element : 0.120"  # scripted group (container) (typed FeaturePython)
  n = 0.120058
FEATURE [App::DocumentObjectGroupPython] N_element028  label="N_element : 0.758"  # scripted group (container) (typed FeaturePython)
  n = 0.035451
FEATURE [App::DocumentObjectGroupPython] O_element068  label="O_element : 0.743"  # scripted group (container) (typed FeaturePython)
  n = 0.742522
FEATURE [App::DocumentObjectGroupPython] G4_MUSCLE_WITHOUT_SUCROSE  # scripted group (container) (typed FeaturePython)
  Dunit = g/cm3
  Dvalue = 1.07
  Group = -> [H_element060,C_element066,N_element028,O_element068]
  conduct = 2
  density = 1
  expand = 3
  formula = G4_MUSCLE_WITHOUT_SUCROSE
  name = G4_MUSCLE_WITHOUT_SUCROSE
  specific = 4
FEATURE [App::DocumentObjectGroupPython] C_element067  label="C_element : 10"  # scripted group (container) (typed FeaturePython)
  n = 10
  ref = C_element
FEATURE [App::DocumentObjectGroupPython] H_element061  label="H_element : 030"  # scripted group (container) (typed FeaturePython)
  n = 8
  ref = H_element
FEATURE [App::DocumentObjectGroupPython] G4_NAPHTHALENE  # scripted group (container) (typed FeaturePython)
  Dunit = g/cm3
  Dvalue = 1.145
  Group = -> [C_element067,H_element061]
  conduct = 2
  density = 1
  expand = 3
  formula = G4_NAPHTHALENE
  name = G4_NAPHTHALENE
  specific = 4
FEATURE [App::DocumentObjectGroupPython] C_element068  label="C_element : 034"  # scripted group (container) (typed FeaturePython)
  n = 6
  ref = C_element
FEATURE [App::DocumentObjectGroupPython] H_element062  label="H_element : 031"  # scripted group (container) (typed FeaturePython)
  n = 5
  ref = H_element
FEATURE [App::DocumentObjectGroupPython] N_element029  label="N_element : 012"  # scripted group (container) (typed FeaturePython)
  n = 1
  ref = N_element
FEATURE [App::DocumentObjectGroupPython] O_element069  label="O_element : 034"  # scripted group (container) (typed FeaturePython)
  n = 2
  ref = O_element
FEATURE [App::DocumentObjectGroupPython] G4_NITROBENZENE  # scripted group (container) (typed FeaturePython)
  Dunit = g/cm3
  Dvalue = 1.19867
  Group = -> [C_element068,H_element062,N_element029,O_element069]
  conduct = 2
  density = 1
  expand = 3
  formula = G4_NITROBENZENE
  name = G4_NITROBENZENE
  specific = 4
FEATURE [App::DocumentObjectGroupPython] N_element030  label="N_element : 013"  # scripted group (container) (typed FeaturePython)
  n = 2
  ref = N_element
FEATURE [App::DocumentObjectGroupPython] O_element070  label="O_element : 035"  # scripted group (container) (typed FeaturePython)
  n = 1
  ref = O_element
FEATURE [App::DocumentObjectGroupPython] G4_NITROUS_OXIDE  # scripted group (container) (typed FeaturePython)
  Dunit = g/cm3
  Dvalue = 0.00183094
  Group = -> [N_element030,O_element070]
  conduct = 2
  density = 1
  expand = 3
  formula = G4_NITROUS_OXIDE
  name = G4_NITROUS_OXIDE
  specific = 4
FEATURE [App::DocumentObjectGroupPython] H_element063  label="H_element : 0.104"  # scripted group (container) (typed FeaturePython)
  n = 0.103509
FEATURE [App::DocumentObjectGroupPython] C_element069  label="C_element : 0.648"  # scripted group (container) (typed FeaturePython)
  n = 0.648416
FEATURE [App::DocumentObjectGroupPython] N_element031  label="N_element : 0.100"  # scripted group (container) (typed FeaturePython)
  n = 0.0995361
FEATURE [App::DocumentObjectGroupPython] O_element071  label="O_element : 0.149"  # scripted group (container) (typed FeaturePython)
  n = 0.148539
FEATURE [App::DocumentObjectGroupPython] G4_NYLON_8062  label="G4_NYLON-8062"  # scripted group (container) (typed FeaturePython)
  Dunit = g/cm3
  Dvalue = 1.08
  Group = -> [H_element063,C_element069,N_element031,O_element071]
  conduct = 2
  density = 1
  expand = 3
  formula = G4_NYLON-8062
  name = G4_NYLON-8062
  specific = 4
FEATURE [App::DocumentObjectGroupPython] C_element070  label="C_element : 035"  # scripted group (container) (typed FeaturePython)
  n = 6
  ref = C_element
FEATURE [App::DocumentObjectGroupPython] H_element064  label="H_element : 11"  # scripted group (container) (typed FeaturePython)
  n = 11
  ref = H_element
FEATURE [App::DocumentObjectGroupPython] N_element032  label="N_element : 014"  # scripted group (container) (typed FeaturePython)
  n = 1
  ref = N_element
FEATURE [App::DocumentObjectGroupPython] O_element072  label="O_element : 036"  # scripted group (container) (typed FeaturePython)
  n = 1
  ref = O_element
FEATURE [App::DocumentObjectGroupPython] G4_NYLON_6_6  label="G4_NYLON-6-6"  # scripted group (container) (typed FeaturePython)
  Dunit = g/cm3
  Dvalue = 1.14
  Group = -> [C_element070,H_element064,N_element032,O_element072]
  conduct = 2
  density = 1
  expand = 3
  formula = G4_NYLON-6-6
  name = G4_NYLON-6-6
  specific = 4
FEATURE [App::DocumentObjectGroupPython] H_element065  label="H_element : 0.139"  # scripted group (container) (typed FeaturePython)
  n = 0.107062
FEATURE [App::DocumentObjectGroupPython] C_element071  label="C_element : 0.680"  # scripted group (container) (typed FeaturePython)
  n = 0.680449
FEATURE [App::DocumentObjectGroupPython] N_element033  label="N_element : 0.099"  # scripted group (container) (typed FeaturePython)
  n = 0.099189
FEATURE [App::DocumentObjectGroupPython] O_element073  label="O_element : 0.113"  # scripted group (container) (typed FeaturePython)
  n = 0.1133
FEATURE [App::DocumentObjectGroupPython] G4_NYLON_6_10  label="G4_NYLON-6-10"  # scripted group (container) (typed FeaturePython)
  Dunit = g/cm3
  Dvalue = 1.14
  Group = -> [H_element065,C_element071,N_element033,O_element073]
  conduct = 2
  density = 1
  expand = 3
  formula = G4_NYLON-6-10
  name = G4_NYLON-6-10
  specific = 4
FEATURE [App::DocumentObjectGroupPython] H_element066  label="H_element : 0.140"  # scripted group (container) (typed FeaturePython)
  n = 0.115476
FEATURE [App::DocumentObjectGroupPython] C_element072  label="C_element : 0.721"  # scripted group (container) (typed FeaturePython)
  n = 0.720818
FEATURE [App::DocumentObjectGroupPython] N_element034  label="N_element : 0.076"  # scripted group (container) (typed FeaturePython)
  n = 0.0764169
FEATURE [App::DocumentObjectGroupPython] O_element074  label="O_element : 0.087"  # scripted group (container) (typed FeaturePython)
  n = 0.0872889
FEATURE [App::DocumentObjectGroupPython] G4_NYLON_11_RILSAN  label="G4_NYLON-11_RILSAN"  # scripted group (container) (typed FeaturePython)
  Dunit = g/cm3
  Dvalue = 1.425
  Group = -> [H_element066,C_element072,N_element034,O_element074]
  conduct = 2
  density = 1
  expand = 3
  formula = G4_NYLON-11_RILSAN
  name = G4_NYLON-11_RILSAN
  specific = 4
FEATURE [App::DocumentObjectGroupPython] C_element073  label="C_element : 8"  # scripted group (container) (typed FeaturePython)
  n = 8
  ref = C_element
FEATURE [App::DocumentObjectGroupPython] H_element067  label="H_element : 18"  # scripted group (container) (typed FeaturePython)
  n = 18
  ref = H_element
FEATURE [App::DocumentObjectGroupPython] G4_OCTANE  # scripted group (container) (typed FeaturePython)
  Dunit = g/cm3
  Dvalue = 0.7026
  Group = -> [C_element073,H_element067]
  conduct = 2
  density = 1
  expand = 3
  formula = G4_OCTANE
  name = G4_OCTANE
  specific = 4
FEATURE [App::DocumentObjectGroupPython] C_element074  label="C_element : 25"  # scripted group (container) (typed FeaturePython)
  n = 25
  ref = C_element
FEATURE [App::DocumentObjectGroupPython] H_element068  label="H_element : 52"  # scripted group (container) (typed FeaturePython)
  n = 52
  ref = H_element
FEATURE [App::DocumentObjectGroupPython] G4_PARAFFIN  # scripted group (container) (typed FeaturePython)
  Dunit = g/cm3
  Dvalue = 0.93
  Group = -> [C_element074,H_element068]
  conduct = 2
  density = 1
  expand = 3
  formula = G4_PARAFFIN
  name = G4_PARAFFIN
  specific = 4
FEATURE [App::DocumentObjectGroupPython] C_element075  label="C_element : 036"  # scripted group (container) (typed FeaturePython)
  n = 5
  ref = C_element
FEATURE [App::DocumentObjectGroupPython] H_element069  label="H_element : 032"  # scripted group (container) (typed FeaturePython)
  n = 12
  ref = H_element
FEATURE [App::DocumentObjectGroupPython] G4_N_PENTANE  label="G4_N-PENTANE"  # scripted group (container) (typed FeaturePython)
  Dunit = g/cm3
  Dvalue = 0.6262
  Group = -> [C_element075,H_element069]
  conduct = 2
  density = 1
  expand = 3
  formula = G4_N-PENTANE
  name = G4_N-PENTANE
  specific = 4
FEATURE [App::DocumentObjectGroupPython] H_element070  label="H_element : 0.014"  # scripted group (container) (typed FeaturePython)
  n = 0.0141
FEATURE [App::DocumentObjectGroupPython] C_element076  label="C_element : 0.072"  # scripted group (container) (typed FeaturePython)
  n = 0.072261
FEATURE [App::DocumentObjectGroupPython] N_element035  label="N_element : 0.019"  # scripted group (container) (typed FeaturePython)
  n = 0.01932
FEATURE [App::DocumentObjectGroupPython] O_element075  label="O_element : 0.066"  # scripted group (container) (typed FeaturePython)
  n = 0.066101
FEATURE [App::DocumentObjectGroupPython] S_element019  label="S_element : 0.020"  # scripted group (container) (typed FeaturePython)
  n = 0.00189
FEATURE [App::DocumentObjectGroupPython] Br_element004  label="Br_element : 0.349"  # scripted group (container) (typed FeaturePython)
  n = 0.349103
FEATURE [App::DocumentObjectGroupPython] Ag_element001  label="Ag_element : 0.474"  # scripted group (container) (typed FeaturePython)
  n = 0.474105
FEATURE [App::DocumentObjectGroupPython] I_element005  label="I_element : 0.003"  # scripted group (container) (typed FeaturePython)
  n = 0.00312
FEATURE [App::DocumentObjectGroupPython] G4_PHOTO_EMULSION  # scripted group (container) (typed FeaturePython)
  Dunit = g/cm3
  Dvalue = 3.815
  Group = -> [H_element070,C_element076,N_element035,O_element075,S_element019,Br_element004,Ag_element001,I_element005]
  conduct = 2
  density = 1
  expand = 3
  formula = G4_PHOTO_EMULSION
  name = G4_PHOTO_EMULSION
  specific = 4
FEATURE [App::DocumentObjectGroupPython] C_element077  label="C_element : 9"  # scripted group (container) (typed FeaturePython)
  n = 9
  ref = C_element
FEATURE [App::DocumentObjectGroupPython] H_element071  label="H_element : 033"  # scripted group (container) (typed FeaturePython)
  n = 10
  ref = H_element
FEATURE [App::DocumentObjectGroupPython] G4_PLASTIC_SC_VINYLTOLUENE  # scripted group (container) (typed FeaturePython)
  Dunit = g/cm3
  Dvalue = 1.032
  Group = -> [C_element077,H_element071]
  conduct = 2
  density = 1
  expand = 3
  formula = G4_PLASTIC_SC_VINYLTOLUENE
  name = G4_PLASTIC_SC_VINYLTOLUENE
  specific = 4
FEATURE [App::DocumentObjectGroupPython] Pu_element001  label="Pu_element : 1"  # scripted group (container) (typed FeaturePython)
  n = 1
  ref = Pu_element
FEATURE [App::DocumentObjectGroupPython] O_element076  label="O_element : 037"  # scripted group (container) (typed FeaturePython)
  n = 2
  ref = O_element
FEATURE [App::DocumentObjectGroupPython] G4_PLUTONIUM_DIOXIDE  # scripted group (container) (typed FeaturePython)
  Dunit = g/cm3
  Dvalue = 11.46
  Group = -> [Pu_element001,O_element076]
  conduct = 2
  density = 1
  expand = 3
  formula = G4_PLUTONIUM_DIOXIDE
  name = G4_PLUTONIUM_DIOXIDE
  specific = 4
FEATURE [App::DocumentObjectGroupPython] C_element078  label="C_element : 037"  # scripted group (container) (typed FeaturePython)
  n = 3
  ref = C_element
FEATURE [App::DocumentObjectGroupPython] H_element072  label="H_element : 034"  # scripted group (container) (typed FeaturePython)
  n = 3
  ref = H_element
FEATURE [App::DocumentObjectGroupPython] N_element036  label="N_element : 015"  # scripted group (container) (typed FeaturePython)
  n = 1
  ref = N_element
FEATURE [App::DocumentObjectGroupPython] G4_POLYACRYLONITRILE  # scripted group (container) (typed FeaturePython)
  Dunit = g/cm3
  Dvalue = 1.17
  Group = -> [C_element078,H_element072,N_element036]
  conduct = 2
  density = 1
  expand = 3
  formula = G4_POLYACRYLONITRILE
  name = G4_POLYACRYLONITRILE
  specific = 4
FEATURE [App::DocumentObjectGroupPython] C_element079  label="C_element : 16"  # scripted group (container) (typed FeaturePython)
  n = 16
  ref = C_element
FEATURE [App::DocumentObjectGroupPython] H_element073  label="H_element : 035"  # scripted group (container) (typed FeaturePython)
  n = 14
  ref = H_element
FEATURE [App::DocumentObjectGroupPython] O_element077  label="O_element : 038"  # scripted group (container) (typed FeaturePython)
  n = 3
  ref = O_element
FEATURE [App::DocumentObjectGroupPython] G4_POLYCARBONATE  # scripted group (container) (typed FeaturePython)
  Dunit = g/cm3
  Dvalue = 1.2
  Group = -> [C_element079,H_element073,O_element077]
  conduct = 2
  density = 1
  expand = 3
  formula = G4_POLYCARBONATE
  name = G4_POLYCARBONATE
  specific = 4
FEATURE [App::DocumentObjectGroupPython] C_element080  label="C_element : 038"  # scripted group (container) (typed FeaturePython)
  n = 8
  ref = C_element
FEATURE [App::DocumentObjectGroupPython] H_element074  label="H_element : 036"  # scripted group (container) (typed FeaturePython)
  n = 7
  ref = H_element
FEATURE [App::DocumentObjectGroupPython] Cl_element017  label="Cl_element : 007"  # scripted group (container) (typed FeaturePython)
  n = 1
  ref = Cl_element
FEATURE [App::DocumentObjectGroupPython] G4_POLYCHLOROSTYRENE  # scripted group (container) (typed FeaturePython)
  Dunit = g/cm3
  Dvalue = 1.3
  Group = -> [C_element080,H_element074,Cl_element017]
  conduct = 2
  density = 1
  expand = 3
  formula = G4_POLYCHLOROSTYRENE
  name = G4_POLYCHLOROSTYRENE
  specific = 4
FEATURE [App::DocumentObjectGroupPython] C_element081  label="C_element : 039"  # scripted group (container) (typed FeaturePython)
  n = 1
  ref = C_element
FEATURE [App::DocumentObjectGroupPython] H_element075  label="H_element : 037"  # scripted group (container) (typed FeaturePython)
  n = 2
  ref = H_element
FEATURE [App::DocumentObjectGroupPython] G4_POLYETHYLENE  # scripted group (container) (typed FeaturePython)
  Dunit = g/cm3
  Dvalue = 0.94
  Group = -> [C_element081,H_element075]
  conduct = 2
  density = 1
  expand = 3
  formula = G4_POLYETHYLENE
  name = G4_POLYETHYLENE
  specific = 4
FEATURE [App::DocumentObjectGroupPython] C_element082  label="C_element : 040"  # scripted group (container) (typed FeaturePython)
  n = 10
  ref = C_element
FEATURE [App::DocumentObjectGroupPython] H_element076  label="H_element : 038"  # scripted group (container) (typed FeaturePython)
  n = 8
  ref = H_element
FEATURE [App::DocumentObjectGroupPython] O_element078  label="O_element : 039"  # scripted group (container) (typed FeaturePython)
  n = 4
  ref = O_element
FEATURE [App::DocumentObjectGroupPython] G4_MYLAR  # scripted group (container) (typed FeaturePython)
  Dunit = g/cm3
  Dvalue = 1.4
  Group = -> [C_element082,H_element076,O_element078]
  conduct = 2
  density = 1
  expand = 3
  formula = G4_MYLAR
  name = G4_MYLAR
  specific = 4
FEATURE [App::DocumentObjectGroupPython] C_element083  label="C_element : 041"  # scripted group (container) (typed FeaturePython)
  n = 5
  ref = C_element
FEATURE [App::DocumentObjectGroupPython] H_element077  label="H_element : 039"  # scripted group (container) (typed FeaturePython)
  n = 8
  ref = H_element
FEATURE [App::DocumentObjectGroupPython] O_element079  label="O_element : 040"  # scripted group (container) (typed FeaturePython)
  n = 2
  ref = O_element
FEATURE [App::DocumentObjectGroupPython] G4_PLEXIGLASS  # scripted group (container) (typed FeaturePython)
  Dunit = g/cm3
  Dvalue = 1.19
  Group = -> [C_element083,H_element077,O_element079]
  conduct = 2
  density = 1
  expand = 3
  formula = G4_PLEXIGLASS
  name = G4_PLEXIGLASS
  specific = 4
FEATURE [App::DocumentObjectGroupPython] C_element084  label="C_element : 042"  # scripted group (container) (typed FeaturePython)
  n = 1
  ref = C_element
FEATURE [App::DocumentObjectGroupPython] H_element078  label="H_element : 040"  # scripted group (container) (typed FeaturePython)
  n = 2
  ref = H_element
FEATURE [App::DocumentObjectGroupPython] O_element080  label="O_element : 041"  # scripted group (container) (typed FeaturePython)
  n = 1
  ref = O_element
FEATURE [App::DocumentObjectGroupPython] G4_POLYOXYMETHYLENE  # scripted group (container) (typed FeaturePython)
  Dunit = g/cm3
  Dvalue = 1.425
  Group = -> [C_element084,H_element078,O_element080]
  conduct = 2
  density = 1
  expand = 3
  formula = G4_POLYOXYMETHYLENE
  name = G4_POLYOXYMETHYLENE
  specific = 4
FEATURE [App::DocumentObjectGroupPython] C_element085  label="C_element : 043"  # scripted group (container) (typed FeaturePython)
  n = 2
  ref = C_element
FEATURE [App::DocumentObjectGroupPython] H_element079  label="H_element : 041"  # scripted group (container) (typed FeaturePython)
  n = 4
  ref = H_element
FEATURE [App::DocumentObjectGroupPython] G4_POLYPROPYLENE  # scripted group (container) (typed FeaturePython)
  Dunit = g/cm3
  Dvalue = 0.9
  Group = -> [C_element085,H_element079]
  conduct = 2
  density = 1
  expand = 3
  formula = G4_POLYPROPYLENE
  name = G4_POLYPROPYLENE
  specific = 4
FEATURE [App::DocumentObjectGroupPython] C_element086  label="C_element : 044"  # scripted group (container) (typed FeaturePython)
  n = 8
  ref = C_element
FEATURE [App::DocumentObjectGroupPython] H_element080  label="H_element : 042"  # scripted group (container) (typed FeaturePython)
  n = 8
  ref = H_element
FEATURE [App::DocumentObjectGroupPython] G4_POLYSTYRENE  # scripted group (container) (typed FeaturePython)
  Dunit = g/cm3
  Dvalue = 1.06
  Group = -> [C_element086,H_element080]
  conduct = 2
  density = 1
  expand = 3
  formula = G4_POLYSTYRENE
  name = G4_POLYSTYRENE
  specific = 4
FEATURE [App::DocumentObjectGroupPython] C_element087  label="C_element : 045"  # scripted group (container) (typed FeaturePython)
  n = 2
  ref = C_element
FEATURE [App::DocumentObjectGroupPython] F_element014  label="F_element : 4"  # scripted group (container) (typed FeaturePython)
  n = 4
  ref = F_element
FEATURE [App::DocumentObjectGroupPython] G4_TEFLON  # scripted group (container) (typed FeaturePython)
  Dunit = g/cm3
  Dvalue = 2.2
  Group = -> [C_element087,F_element014]
  conduct = 2
  density = 1
  expand = 3
  formula = G4_TEFLON
  name = G4_TEFLON
  specific = 4
FEATURE [App::DocumentObjectGroupPython] C_element088  label="C_element : 046"  # scripted group (container) (typed FeaturePython)
  n = 2
  ref = C_element
FEATURE [App::DocumentObjectGroupPython] F_element015  label="F_element : 006"  # scripted group (container) (typed FeaturePython)
  n = 3
  ref = F_element
FEATURE [App::DocumentObjectGroupPython] Cl_element018  label="Cl_element : 008"  # scripted group (container) (typed FeaturePython)
  n = 1
  ref = Cl_element
FEATURE [App::DocumentObjectGroupPython] G4_POLYTRIFLUOROCHLOROETHYLENE  # scripted group (container) (typed FeaturePython)
  Dunit = g/cm3
  Dvalue = 2.1
  Group = -> [C_element088,F_element015,Cl_element018]
  conduct = 2
  density = 1
  expand = 3
  formula = G4_POLYTRIFLUOROCHLOROETHYLENE
  name = G4_POLYTRIFLUOROCHLOROETHYLENE
  specific = 4
FEATURE [App::DocumentObjectGroupPython] C_element089  label="C_element : 047"  # scripted group (container) (typed FeaturePython)
  n = 4
  ref = C_element
FEATURE [App::DocumentObjectGroupPython] H_element081  label="H_element : 043"  # scripted group (container) (typed FeaturePython)
  n = 6
  ref = H_element
FEATURE [App::DocumentObjectGroupPython] O_element081  label="O_element : 042"  # scripted group (container) (typed FeaturePython)
  n = 2
  ref = O_element
FEATURE [App::DocumentObjectGroupPython] G4_POLYVINYL_ACETATE  # scripted group (container) (typed FeaturePython)
  Dunit = g/cm3
  Dvalue = 1.19
  Group = -> [C_element089,H_element081,O_element081]
  conduct = 2
  density = 1
  expand = 3
  formula = G4_POLYVINYL_ACETATE
  name = G4_POLYVINYL_ACETATE
  specific = 4
FEATURE [App::DocumentObjectGroupPython] C_element090  label="C_element : 048"  # scripted group (container) (typed FeaturePython)
  n = 2
  ref = C_element
FEATURE [App::DocumentObjectGroupPython] H_element082  label="H_element : 044"  # scripted group (container) (typed FeaturePython)
  n = 4
  ref = H_element
FEATURE [App::DocumentObjectGroupPython] O_element082  label="O_element : 043"  # scripted group (container) (typed FeaturePython)
  n = 1
  ref = O_element
FEATURE [App::DocumentObjectGroupPython] G4_POLYVINYL_ALCOHOL  # scripted group (container) (typed FeaturePython)
  Dunit = g/cm3
  Dvalue = 1.3
  Group = -> [C_element090,H_element082,O_element082]
  conduct = 2
  density = 1
  expand = 3
  formula = G4_POLYVINYL_ALCOHOL
  name = G4_POLYVINYL_ALCOHOL
  specific = 4
FEATURE [App::DocumentObjectGroupPython] C_element091  label="C_element : 049"  # scripted group (container) (typed FeaturePython)
  n = 8
  ref = C_element
FEATURE [App::DocumentObjectGroupPython] H_element083  label="H_element : 045"  # scripted group (container) (typed FeaturePython)
  n = 14
  ref = H_element
FEATURE [App::DocumentObjectGroupPython] O_element083  label="O_element : 044"  # scripted group (container) (typed FeaturePython)
  n = 2
  ref = O_element
FEATURE [App::DocumentObjectGroupPython] G4_POLYVINYL_BUTYRAL  # scripted group (container) (typed FeaturePython)
  Dunit = g/cm3
  Dvalue = 1.12
  Group = -> [C_element091,H_element083,O_element083]
  conduct = 2
  density = 1
  expand = 3
  formula = G4_POLYVINYL_BUTYRAL
  name = G4_POLYVINYL_BUTYRAL
  specific = 4
FEATURE [App::DocumentObjectGroupPython] C_element092  label="C_element : 050"  # scripted group (container) (typed FeaturePython)
  n = 2
  ref = C_element
FEATURE [App::DocumentObjectGroupPython] H_element084  label="H_element : 046"  # scripted group (container) (typed FeaturePython)
  n = 3
  ref = H_element
FEATURE [App::DocumentObjectGroupPython] Cl_element019  label="Cl_element : 009"  # scripted group (container) (typed FeaturePython)
  n = 1
  ref = Cl_element
FEATURE [App::DocumentObjectGroupPython] G4_POLYVINYL_CHLORIDE  # scripted group (container) (typed FeaturePython)
  Dunit = g/cm3
  Dvalue = 1.3
  Group = -> [C_element092,H_element084,Cl_element019]
  conduct = 2
  density = 1
  expand = 3
  formula = G4_POLYVINYL_CHLORIDE
  name = G4_POLYVINYL_CHLORIDE
  specific = 4
FEATURE [App::DocumentObjectGroupPython] C_element093  label="C_element : 051"  # scripted group (container) (typed FeaturePython)
  n = 2
  ref = C_element
FEATURE [App::DocumentObjectGroupPython] H_element085  label="H_element : 047"  # scripted group (container) (typed FeaturePython)
  n = 2
  ref = H_element
FEATURE [App::DocumentObjectGroupPython] Cl_element020  label="Cl_element : 010"  # scripted group (container) (typed FeaturePython)
  n = 2
  ref = Cl_element
FEATURE [App::DocumentObjectGroupPython] G4_POLYVINYLIDENE_CHLORIDE  # scripted group (container) (typed FeaturePython)
  Dunit = g/cm3
  Dvalue = 1.7
  Group = -> [C_element093,H_element085,Cl_element020]
  conduct = 2
  density = 1
  expand = 3
  formula = G4_POLYVINYLIDENE_CHLORIDE
  name = G4_POLYVINYLIDENE_CHLORIDE
  specific = 4
FEATURE [App::DocumentObjectGroupPython] C_element094  label="C_element : 052"  # scripted group (container) (typed FeaturePython)
  n = 2
  ref = C_element
FEATURE [App::DocumentObjectGroupPython] H_element086  label="H_element : 048"  # scripted group (container) (typed FeaturePython)
  n = 2
  ref = H_element
FEATURE [App::DocumentObjectGroupPython] F_element016  label="F_element : 007"  # scripted group (container) (typed FeaturePython)
  n = 2
  ref = F_element
FEATURE [App::DocumentObjectGroupPython] G4_POLYVINYLIDENE_FLUORIDE  # scripted group (container) (typed FeaturePython)
  Dunit = g/cm3
  Dvalue = 1.76
  Group = -> [C_element094,H_element086,F_element016]
  conduct = 2
  density = 1
  expand = 3
  formula = G4_POLYVINYLIDENE_FLUORIDE
  name = G4_POLYVINYLIDENE_FLUORIDE
  specific = 4
FEATURE [App::DocumentObjectGroupPython] C_element095  label="C_element : 053"  # scripted group (container) (typed FeaturePython)
  n = 6
  ref = C_element
FEATURE [App::DocumentObjectGroupPython] H_element087  label="H_element : 9"  # scripted group (container) (typed FeaturePython)
  n = 9
  ref = H_element
FEATURE [App::DocumentObjectGroupPython] N_element037  label="N_element : 016"  # scripted group (container) (typed FeaturePython)
  n = 1
  ref = N_element
FEATURE [App::DocumentObjectGroupPython] O_element084  label="O_element : 045"  # scripted group (container) (typed FeaturePython)
  n = 1
  ref = O_element
FEATURE [App::DocumentObjectGroupPython] G4_POLYVINYL_PYRROLIDONE  # scripted group (container) (typed FeaturePython)
  Dunit = g/cm3
  Dvalue = 1.25
  Group = -> [C_element095,H_element087,N_element037,O_element084]
  conduct = 2
  density = 1
  expand = 3
  formula = G4_POLYVINYL_PYRROLIDONE
  name = G4_POLYVINYL_PYRROLIDONE
  specific = 4
FEATURE [App::DocumentObjectGroupPython] K_element008  label="K_element : 1"  # scripted group (container) (typed FeaturePython)
  n = 1
  ref = K_element
FEATURE [App::DocumentObjectGroupPython] I_element006  label="I_element : 003"  # scripted group (container) (typed FeaturePython)
  n = 1
  ref = I_element
FEATURE [App::DocumentObjectGroupPython] G4_POTASSIUM_IODIDE  # scripted group (container) (typed FeaturePython)
  Dunit = g/cm3
  Dvalue = 3.13
  Group = -> [K_element008,I_element006]
  conduct = 2
  density = 1
  expand = 3
  formula = G4_POTASSIUM_IODIDE
  name = G4_POTASSIUM_IODIDE
  specific = 4
FEATURE [App::DocumentObjectGroupPython] K_element009  label="K_element : 2"  # scripted group (container) (typed FeaturePython)
  n = 2
  ref = K_element
FEATURE [App::DocumentObjectGroupPython] O_element085  label="O_element : 046"  # scripted group (container) (typed FeaturePython)
  n = 1
  ref = O_element
FEATURE [App::DocumentObjectGroupPython] G4_POTASSIUM_OXIDE  # scripted group (container) (typed FeaturePython)
  Dunit = g/cm3
  Dvalue = 2.32
  Group = -> [K_element009,O_element085]
  conduct = 2
  density = 1
  expand = 3
  formula = G4_POTASSIUM_OXIDE
  name = G4_POTASSIUM_OXIDE
  specific = 4
FEATURE [App::DocumentObjectGroupPython] C_element096  label="C_element : 054"  # scripted group (container) (typed FeaturePython)
  n = 3
  ref = C_element
FEATURE [App::DocumentObjectGroupPython] H_element088  label="H_element : 049"  # scripted group (container) (typed FeaturePython)
  n = 8
  ref = H_element
FEATURE [App::DocumentObjectGroupPython] G4_PROPANE  # scripted group (container) (typed FeaturePython)
  Dunit = g/cm3
  Dvalue = 0.00187939
  Group = -> [C_element096,H_element088]
  conduct = 2
  density = 1
  expand = 3
  formula = G4_PROPANE
  name = G4_PROPANE
  specific = 4
FEATURE [App::DocumentObjectGroupPython] C_element097  label="C_element : 055"  # scripted group (container) (typed FeaturePython)
  n = 3
  ref = C_element
FEATURE [App::DocumentObjectGroupPython] H_element089  label="H_element : 050"  # scripted group (container) (typed FeaturePython)
  n = 8
  ref = H_element
FEATURE [App::DocumentObjectGroupPython] G4_lPROPANE  # scripted group (container) (typed FeaturePython)
  Dunit = g/cm3
  Dvalue = 0.43
  Group = -> [C_element097,H_element089]
  conduct = 2
  density = 1
  expand = 3
  formula = G4_lPROPANE
  name = G4_lPROPANE
  specific = 4
FEATURE [App::DocumentObjectGroupPython] C_element098  label="C_element : 056"  # scripted group (container) (typed FeaturePython)
  n = 3
  ref = C_element
FEATURE [App::DocumentObjectGroupPython] H_element090  label="H_element : 051"  # scripted group (container) (typed FeaturePython)
  n = 8
  ref = H_element
FEATURE [App::DocumentObjectGroupPython] O_element086  label="O_element : 047"  # scripted group (container) (typed FeaturePython)
  n = 1
  ref = O_element
FEATURE [App::DocumentObjectGroupPython] G4_N_PROPYL_ALCOHOL  label="G4_N-PROPYL_ALCOHOL"  # scripted group (container) (typed FeaturePython)
  Dunit = g/cm3
  Dvalue = 0.8035
  Group = -> [C_element098,H_element090,O_element086]
  conduct = 2
  density = 1
  expand = 3
  formula = G4_N-PROPYL_ALCOHOL
  name = G4_N-PROPYL_ALCOHOL
  specific = 4
FEATURE [App::DocumentObjectGroupPython] C_element099  label="C_element : 057"  # scripted group (container) (typed FeaturePython)
  n = 5
  ref = C_element
FEATURE [App::DocumentObjectGroupPython] H_element091  label="H_element : 052"  # scripted group (container) (typed FeaturePython)
  n = 5
  ref = H_element
FEATURE [App::DocumentObjectGroupPython] N_element038  label="N_element : 017"  # scripted group (container) (typed FeaturePython)
  n = 1
  ref = N_element
FEATURE [App::DocumentObjectGroupPython] G4_PYRIDINE  # scripted group (container) (typed FeaturePython)
  Dunit = g/cm3
  Dvalue = 0.9819
  Group = -> [C_element099,H_element091,N_element038]
  conduct = 2
  density = 1
  expand = 3
  formula = G4_PYRIDINE
  name = G4_PYRIDINE
  specific = 4
FEATURE [App::DocumentObjectGroupPython] H_element092  label="H_element : 0.144"  # scripted group (container) (typed FeaturePython)
  n = 0.143711
FEATURE [App::DocumentObjectGroupPython] C_element100  label="C_element : 0.856"  # scripted group (container) (typed FeaturePython)
  n = 0.856289
FEATURE [App::DocumentObjectGroupPython] G4_RUBBER_BUTYL  # scripted group (container) (typed FeaturePython)
  Dunit = g/cm3
  Dvalue = 0.92
  Group = -> [H_element092,C_element100]
  conduct = 2
  density = 1
  expand = 3
  formula = G4_RUBBER_BUTYL
  name = G4_RUBBER_BUTYL
  specific = 4
FEATURE [App::DocumentObjectGroupPython] H_element093  label="H_element : 0.118"  # scripted group (container) (typed FeaturePython)
  n = 0.118371
FEATURE [App::DocumentObjectGroupPython] C_element101  label="C_element : 0.882"  # scripted group (container) (typed FeaturePython)
  n = 0.881629
FEATURE [App::DocumentObjectGroupPython] G4_RUBBER_NATURAL  # scripted group (container) (typed FeaturePython)
  Dunit = g/cm3
  Dvalue = 0.92
  Group = -> [H_element093,C_element101]
  conduct = 2
  density = 1
  expand = 3
  formula = G4_RUBBER_NATURAL
  name = G4_RUBBER_NATURAL
  specific = 4
FEATURE [App::DocumentObjectGroupPython] H_element094  label="H_element : 0.145"  # scripted group (container) (typed FeaturePython)
  n = 0.05692
FEATURE [App::DocumentObjectGroupPython] C_element102  label="C_element : 0.543"  # scripted group (container) (typed FeaturePython)
  n = 0.542646
FEATURE [App::DocumentObjectGroupPython] Cl_element021  label="Cl_element : 0.400"  # scripted group (container) (typed FeaturePython)
  n = 0.400434
FEATURE [App::DocumentObjectGroupPython] G4_RUBBER_NEOPRENE  # scripted group (container) (typed FeaturePython)
  Dunit = g/cm3
  Dvalue = 1.23
  Group = -> [H_element094,C_element102,Cl_element021]
  conduct = 2
  density = 1
  expand = 3
  formula = G4_RUBBER_NEOPRENE
  name = G4_RUBBER_NEOPRENE
  specific = 4
FEATURE [App::DocumentObjectGroupPython] Si_element006  label="Si_element : 1"  # scripted group (container) (typed FeaturePython)
  n = 1
  ref = Si_element
FEATURE [App::DocumentObjectGroupPython] O_element087  label="O_element : 048"  # scripted group (container) (typed FeaturePython)
  n = 2
  ref = O_element
FEATURE [App::DocumentObjectGroupPython] G4_SILICON_DIOXIDE  # scripted group (container) (typed FeaturePython)
  Dunit = g/cm3
  Dvalue = 2.32
  Group = -> [Si_element006,O_element087]
  conduct = 2
  density = 1
  expand = 3
  formula = G4_SILICON_DIOXIDE
  name = G4_SILICON_DIOXIDE
  specific = 4
FEATURE [App::DocumentObjectGroupPython] Ag_element002  label="Ag_element : 1"  # scripted group (container) (typed FeaturePython)
  n = 1
  ref = Ag_element
FEATURE [App::DocumentObjectGroupPython] Br_element005  label="Br_element : 003"  # scripted group (container) (typed FeaturePython)
  n = 1
  ref = Br_element
FEATURE [App::DocumentObjectGroupPython] G4_SILVER_BROMIDE  # scripted group (container) (typed FeaturePython)
  Dunit = g/cm3
  Dvalue = 6.473
  Group = -> [Ag_element002,Br_element005]
  conduct = 2
  density = 1
  expand = 3
  formula = G4_SILVER_BROMIDE
  name = G4_SILVER_BROMIDE
  specific = 4
FEATURE [App::DocumentObjectGroupPython] Ag_element003  label="Ag_element : 002"  # scripted group (container) (typed FeaturePython)
  n = 1
  ref = Ag_element
FEATURE [App::DocumentObjectGroupPython] Cl_element022  label="Cl_element : 011"  # scripted group (container) (typed FeaturePython)
  n = 1
  ref = Cl_element
FEATURE [App::DocumentObjectGroupPython] G4_SILVER_CHLORIDE  # scripted group (container) (typed FeaturePython)
  Dunit = g/cm3
  Dvalue = 5.56
  Group = -> [Ag_element003,Cl_element022]
  conduct = 2
  density = 1
  expand = 3
  formula = G4_SILVER_CHLORIDE
  name = G4_SILVER_CHLORIDE
  specific = 4
FEATURE [App::DocumentObjectGroupPython] Br_element006  label="Br_element : 0.423"  # scripted group (container) (typed FeaturePython)
  n = 0.422895
FEATURE [App::DocumentObjectGroupPython] Ag_element004  label="Ag_element : 0.574"  # scripted group (container) (typed FeaturePython)
  n = 0.573748
FEATURE [App::DocumentObjectGroupPython] I_element007  label="I_element : 0.649"  # scripted group (container) (typed FeaturePython)
  n = 0.003357
FEATURE [App::DocumentObjectGroupPython] G4_SILVER_HALIDES  # scripted group (container) (typed FeaturePython)
  Dunit = g/cm3
  Dvalue = 6.47
  Group = -> [Br_element006,Ag_element004,I_element007]
  conduct = 2
  density = 1
  expand = 3
  formula = G4_SILVER_HALIDES
  name = G4_SILVER_HALIDES
  specific = 4
FEATURE [App::DocumentObjectGroupPython] Ag_element005  label="Ag_element : 003"  # scripted group (container) (typed FeaturePython)
  n = 1
  ref = Ag_element
FEATURE [App::DocumentObjectGroupPython] I_element008  label="I_element : 004"  # scripted group (container) (typed FeaturePython)
  n = 1
  ref = I_element
FEATURE [App::DocumentObjectGroupPython] G4_SILVER_IODIDE  # scripted group (container) (typed FeaturePython)
  Dunit = g/cm3
  Dvalue = 6.01
  Group = -> [Ag_element005,I_element008]
  conduct = 2
  density = 1
  expand = 3
  formula = G4_SILVER_IODIDE
  name = G4_SILVER_IODIDE
  specific = 4
FEATURE [App::DocumentObjectGroupPython] H_element095  label="H_element : 0.100"  # scripted group (container) (typed FeaturePython)
  n = 0.1
FEATURE [App::DocumentObjectGroupPython] C_element103  label="C_element : 0.204"  # scripted group (container) (typed FeaturePython)
  n = 0.204
FEATURE [App::DocumentObjectGroupPython] N_element039  label="N_element : 0.759"  # scripted group (container) (typed FeaturePython)
  n = 0.042
FEATURE [App::DocumentObjectGroupPython] O_element088  label="O_element : 0.645"  # scripted group (container) (typed FeaturePython)
  n = 0.645
FEATURE [App::DocumentObjectGroupPython] Na_element013  label="Na_element : 0.100"  # scripted group (container) (typed FeaturePython)
  n = 0.002
FEATURE [App::DocumentObjectGroupPython] P_element009  label="P_element : 0.107"  # scripted group (container) (typed FeaturePython)
  n = 0.001
FEATURE [App::DocumentObjectGroupPython] S_element020  label="S_element : 0.021"  # scripted group (container) (typed FeaturePython)
  n = 0.002
FEATURE [App::DocumentObjectGroupPython] Cl_element023  label="Cl_element : 0.590"  # scripted group (container) (typed FeaturePython)
  n = 0.003
FEATURE [App::DocumentObjectGroupPython] K_element010  label="K_element : 0.001"  # scripted group (container) (typed FeaturePython)
  n = 0.001
FEATURE [App::DocumentObjectGroupPython] G4_SKIN_ICRP  # scripted group (container) (typed FeaturePython)
  Dunit = g/cm3
  Dvalue = 1.09
  Group = -> [H_element095,C_element103,N_element039,O_element088,Na_element013,P_element009,S_element020,Cl_element023,K_element010]
  conduct = 2
  density = 1
  expand = 3
  formula = G4_SKIN_ICRP
  name = G4_SKIN_ICRP
  specific = 4
FEATURE [App::DocumentObjectGroupPython] Na_element014  label="Na_element : 2"  # scripted group (container) (typed FeaturePython)
  n = 2
  ref = Na_element
FEATURE [App::DocumentObjectGroupPython] C_element104  label="C_element : 058"  # scripted group (container) (typed FeaturePython)
  n = 1
  ref = C_element
FEATURE [App::DocumentObjectGroupPython] O_element089  label="O_element : 049"  # scripted group (container) (typed FeaturePython)
  n = 3
  ref = O_element
FEATURE [App::DocumentObjectGroupPython] G4_SODIUM_CARBONATE  # scripted group (container) (typed FeaturePython)
  Dunit = g/cm3
  Dvalue = 2.532
  Group = -> [Na_element014,C_element104,O_element089]
  conduct = 2
  density = 1
  expand = 3
  formula = G4_SODIUM_CARBONATE
  name = G4_SODIUM_CARBONATE
  specific = 4
FEATURE [App::DocumentObjectGroupPython] Na_element015  label="Na_element : 1"  # scripted group (container) (typed FeaturePython)
  n = 1
  ref = Na_element
FEATURE [App::DocumentObjectGroupPython] I_element009  label="I_element : 005"  # scripted group (container) (typed FeaturePython)
  n = 1
  ref = I_element
FEATURE [App::DocumentObjectGroupPython] G4_SODIUM_IODIDE  # scripted group (container) (typed FeaturePython)
  Dunit = g/cm3
  Dvalue = 3.667
  Group = -> [Na_element015,I_element009]
  conduct = 2
  density = 1
  expand = 3
  formula = G4_SODIUM_IODIDE
  name = G4_SODIUM_IODIDE
  specific = 4
FEATURE [App::DocumentObjectGroupPython] Na_element016  label="Na_element : 003"  # scripted group (container) (typed FeaturePython)
  n = 2
  ref = Na_element
FEATURE [App::DocumentObjectGroupPython] O_element090  label="O_element : 050"  # scripted group (container) (typed FeaturePython)
  n = 1
  ref = O_element
FEATURE [App::DocumentObjectGroupPython] G4_SODIUM_MONOXIDE  # scripted group (container) (typed FeaturePython)
  Dunit = g/cm3
  Dvalue = 2.27
  Group = -> [Na_element016,O_element090]
  conduct = 2
  density = 1
  expand = 3
  formula = G4_SODIUM_MONOXIDE
  name = G4_SODIUM_MONOXIDE
  specific = 4
FEATURE [App::DocumentObjectGroupPython] Na_element017  label="Na_element : 004"  # scripted group (container) (typed FeaturePython)
  n = 1
  ref = Na_element
FEATURE [App::DocumentObjectGroupPython] N_element040  label="N_element : 018"  # scripted group (container) (typed FeaturePython)
  n = 1
  ref = N_element
FEATURE [App::DocumentObjectGroupPython] O_element091  label="O_element : 051"  # scripted group (container) (typed FeaturePython)
  n = 3
  ref = O_element
FEATURE [App::DocumentObjectGroupPython] G4_SODIUM_NITRATE  # scripted group (container) (typed FeaturePython)
  Dunit = g/cm3
  Dvalue = 2.261
  Group = -> [Na_element017,N_element040,O_element091]
  conduct = 2
  density = 1
  expand = 3
  formula = G4_SODIUM_NITRATE
  name = G4_SODIUM_NITRATE
  specific = 4
FEATURE [App::DocumentObjectGroupPython] C_element105  label="C_element : 059"  # scripted group (container) (typed FeaturePython)
  n = 14
  ref = C_element
FEATURE [App::DocumentObjectGroupPython] H_element096  label="H_element : 053"  # scripted group (container) (typed FeaturePython)
  n = 12
  ref = H_element
FEATURE [App::DocumentObjectGroupPython] G4_STILBENE  # scripted group (container) (typed FeaturePython)
  Dunit = g/cm3
  Dvalue = 0.9707
  Group = -> [C_element105,H_element096]
  conduct = 2
  density = 1
  expand = 3
  formula = G4_STILBENE
  name = G4_STILBENE
  specific = 4
FEATURE [App::DocumentObjectGroupPython] C_element106  label="C_element : 12"  # scripted group (container) (typed FeaturePython)
  n = 12
  ref = C_element
FEATURE [App::DocumentObjectGroupPython] H_element097  label="H_element : 22"  # scripted group (container) (typed FeaturePython)
  n = 22
  ref = H_element
FEATURE [App::DocumentObjectGroupPython] O_element092  label="O_element : 11"  # scripted group (container) (typed FeaturePython)
  n = 11
  ref = O_element
FEATURE [App::DocumentObjectGroupPython] G4_SUCROSE  # scripted group (container) (typed FeaturePython)
  Dunit = g/cm3
  Dvalue = 1.5805
  Group = -> [C_element106,H_element097,O_element092]
  conduct = 2
  density = 1
  expand = 3
  formula = G4_SUCROSE
  name = G4_SUCROSE
  specific = 4
FEATURE [App::DocumentObjectGroupPython] C_element107  label="C_element : 18"  # scripted group (container) (typed FeaturePython)
  n = 18
  ref = C_element
FEATURE [App::DocumentObjectGroupPython] H_element098  label="H_element : 054"  # scripted group (container) (typed FeaturePython)
  n = 14
  ref = H_element
FEATURE [App::DocumentObjectGroupPython] G4_TERPHENYL  # scripted group (container) (typed FeaturePython)
  Dunit = g/cm3
  Dvalue = 1.24
  Group = -> [C_element107,H_element098]
  conduct = 2
  density = 1
  expand = 3
  formula = G4_TERPHENYL
  name = G4_TERPHENYL
  specific = 4
FEATURE [App::DocumentObjectGroupPython] H_element099  label="H_element : 0.146"  # scripted group (container) (typed FeaturePython)
  n = 0.106
FEATURE [App::DocumentObjectGroupPython] C_element108  label="C_element : 0.883"  # scripted group (container) (typed FeaturePython)
  n = 0.099
FEATURE [App::DocumentObjectGroupPython] N_element041  label="N_element : 0.020"  # scripted group (container) (typed FeaturePython)
  n = 0.02
FEATURE [App::DocumentObjectGroupPython] O_element093  label="O_element : 0.766"  # scripted group (container) (typed FeaturePython)
  n = 0.766
FEATURE [App::DocumentObjectGroupPython] Na_element018  label="Na_element : 0.101"  # scripted group (container) (typed FeaturePython)
  n = 0.002
FEATURE [App::DocumentObjectGroupPython] P_element010  label="P_element : 0.108"  # scripted group (container) (typed FeaturePython)
  n = 0.001
FEATURE [App::DocumentObjectGroupPython] S_element021  label="S_element : 0.022"  # scripted group (container) (typed FeaturePython)
  n = 0.002
FEATURE [App::DocumentObjectGroupPython] Cl_element024  label="Cl_element : 0.002"  # scripted group (container) (typed FeaturePython)
  n = 0.002
FEATURE [App::DocumentObjectGroupPython] K_element011  label="K_element : 0.017"  # scripted group (container) (typed FeaturePython)
  n = 0.002
FEATURE [App::DocumentObjectGroupPython] G4_TESTIS_ICRP  # scripted group (container) (typed FeaturePython)
  Dunit = g/cm3
  Dvalue = 1.04
  Group = -> [H_element099,C_element108,N_element041,O_element093,Na_element018,P_element010,S_element021,Cl_element024,K_element011]
  conduct = 2
  density = 1
  expand = 3
  formula = G4_TESTIS_ICRP
  name = G4_TESTIS_ICRP
  specific = 4
FEATURE [App::DocumentObjectGroupPython] C_element109  label="C_element : 060"  # scripted group (container) (typed FeaturePython)
  n = 2
  ref = C_element
FEATURE [App::DocumentObjectGroupPython] Cl_element025  label="Cl_element : 012"  # scripted group (container) (typed FeaturePython)
  n = 4
  ref = Cl_element
FEATURE [App::DocumentObjectGroupPython] G4_TETRACHLOROETHYLENE  # scripted group (container) (typed FeaturePython)
  Dunit = g/cm3
  Dvalue = 1.625
  Group = -> [C_element109,Cl_element025]
  conduct = 2
  density = 1
  expand = 3
  formula = G4_TETRACHLOROETHYLENE
  name = G4_TETRACHLOROETHYLENE
  specific = 4
FEATURE [App::DocumentObjectGroupPython] Tl_element001  label="Tl_element : 1"  # scripted group (container) (typed FeaturePython)
  n = 1
  ref = Tl_element
FEATURE [App::DocumentObjectGroupPython] Cl_element026  label="Cl_element : 013"  # scripted group (container) (typed FeaturePython)
  n = 1
  ref = Cl_element
FEATURE [App::DocumentObjectGroupPython] G4_THALLIUM_CHLORIDE  # scripted group (container) (typed FeaturePython)
  Dunit = g/cm3
  Dvalue = 7.004
  Group = -> [Tl_element001,Cl_element026]
  conduct = 2
  density = 1
  expand = 3
  formula = G4_THALLIUM_CHLORIDE
  name = G4_THALLIUM_CHLORIDE
  specific = 4
FEATURE [App::DocumentObjectGroupPython] H_element100  label="H_element : 0.147"  # scripted group (container) (typed FeaturePython)
  n = 0.105
FEATURE [App::DocumentObjectGroupPython] C_element110  label="C_element : 0.256"  # scripted group (container) (typed FeaturePython)
  n = 0.256
FEATURE [App::DocumentObjectGroupPython] N_element042  label="N_element : 0.760"  # scripted group (container) (typed FeaturePython)
  n = 0.027
FEATURE [App::DocumentObjectGroupPython] O_element094  label="O_element : 0.602"  # scripted group (container) (typed FeaturePython)
  n = 0.602
FEATURE [App::DocumentObjectGroupPython] Na_element019  label="Na_element : 0.102"  # scripted group (container) (typed FeaturePython)
  n = 0.001
FEATURE [App::DocumentObjectGroupPython] P_element011  label="P_element : 0.109"  # scripted group (container) (typed FeaturePython)
  n = 0.002
FEATURE [App::DocumentObjectGroupPython] S_element022  label="S_element : 0.023"  # scripted group (container) (typed FeaturePython)
  n = 0.003
FEATURE [App::DocumentObjectGroupPython] Cl_element027  label="Cl_element : 0.591"  # scripted group (container) (typed FeaturePython)
  n = 0.002
FEATURE [App::DocumentObjectGroupPython] K_element012  label="K_element : 0.018"  # scripted group (container) (typed FeaturePython)
  n = 0.002
FEATURE [App::DocumentObjectGroupPython] G4_TISSUE_SOFT_ICRP  # scripted group (container) (typed FeaturePython)
  Dunit = g/cm3
  Dvalue = 1.03
  Group = -> [H_element100,C_element110,N_element042,O_element094,Na_element019,P_element011,S_element022,Cl_element027,K_element012]
  conduct = 2
  density = 1
  expand = 3
  formula = G4_TISSUE_SOFT_ICRP
  name = G4_TISSUE_SOFT_ICRP
  specific = 4
FEATURE [App::DocumentObjectGroupPython] H_element101  label="H_element : 0.148"  # scripted group (container) (typed FeaturePython)
  n = 0.101
FEATURE [App::DocumentObjectGroupPython] C_element111  label="C_element : 0.111"  # scripted group (container) (typed FeaturePython)
  n = 0.111
FEATURE [App::DocumentObjectGroupPython] N_element043  label="N_element : 0.026"  # scripted group (container) (typed FeaturePython)
  n = 0.026
FEATURE [App::DocumentObjectGroupPython] O_element095  label="O_element : 0.762"  # scripted group (container) (typed FeaturePython)
  n = 0.762
FEATURE [App::DocumentObjectGroupPython] G4_TISSUE_SOFT_ICRU_4  label="G4_TISSUE_SOFT_ICRU-4"  # scripted group (container) (typed FeaturePython)
  Dunit = g/cm3
  Dvalue = 1
  Group = -> [H_element101,C_element111,N_element043,O_element095]
  conduct = 2
  density = 1
  expand = 3
  formula = G4_TISSUE_SOFT_ICRU-4
  name = G4_TISSUE_SOFT_ICRU-4
  specific = 4
FEATURE [App::DocumentObjectGroupPython] H_element102  label="H_element : 0.149"  # scripted group (container) (typed FeaturePython)
  n = 0.101869
FEATURE [App::DocumentObjectGroupPython] C_element112  label="C_element : 0.456"  # scripted group (container) (typed FeaturePython)
  n = 0.456179
FEATURE [App::DocumentObjectGroupPython] N_element044  label="N_element : 0.761"  # scripted group (container) (typed FeaturePython)
  n = 0.035172
FEATURE [App::DocumentObjectGroupPython] O_element096  label="O_element : 0.407"  # scripted group (container) (typed FeaturePython)
  n = 0.40678
FEATURE [App::DocumentObjectGroupPython] G4_TISSUE_METHANE  label="G4_TISSUE-METHANE"  # scripted group (container) (typed FeaturePython)
  Dunit = g/cm3
  Dvalue = 0.00106409
  Group = -> [H_element102,C_element112,N_element044,O_element096]
  conduct = 2
  density = 1
  expand = 3
  formula = G4_TISSUE-METHANE
  name = G4_TISSUE-METHANE
  specific = 4
FEATURE [App::DocumentObjectGroupPython] H_element103  label="H_element : 0.103"  # scripted group (container) (typed FeaturePython)
  n = 0.102672
FEATURE [App::DocumentObjectGroupPython] C_element113  label="C_element : 0.569"  # scripted group (container) (typed FeaturePython)
  n = 0.56894
FEATURE [App::DocumentObjectGroupPython] N_element045  label="N_element : 0.762"  # scripted group (container) (typed FeaturePython)
  n = 0.035022
FEATURE [App::DocumentObjectGroupPython] O_element097  label="O_element : 0.293"  # scripted group (container) (typed FeaturePython)
  n = 0.293366
FEATURE [App::DocumentObjectGroupPython] G4_TISSUE_PROPANE  label="G4_TISSUE-PROPANE"  # scripted group (container) (typed FeaturePython)
  Dunit = g/cm3
  Dvalue = 0.00182628
  Group = -> [H_element103,C_element113,N_element045,O_element097]
  conduct = 2
  density = 1
  expand = 3
  formula = G4_TISSUE-PROPANE
  name = G4_TISSUE-PROPANE
  specific = 4
FEATURE [App::DocumentObjectGroupPython] Ti_element003  label="Ti_element : 1"  # scripted group (container) (typed FeaturePython)
  n = 1
  ref = Ti_element
FEATURE [App::DocumentObjectGroupPython] O_element098  label="O_element : 052"  # scripted group (container) (typed FeaturePython)
  n = 2
  ref = O_element
FEATURE [App::DocumentObjectGroupPython] G4_TITANIUM_DIOXIDE  # scripted group (container) (typed FeaturePython)
  Dunit = g/cm3
  Dvalue = 4.26
  Group = -> [Ti_element003,O_element098]
  conduct = 2
  density = 1
  expand = 3
  formula = G4_TITANIUM_DIOXIDE
  name = G4_TITANIUM_DIOXIDE
  specific = 4
FEATURE [App::DocumentObjectGroupPython] C_element114  label="C_element : 061"  # scripted group (container) (typed FeaturePython)
  n = 7
  ref = C_element
FEATURE [App::DocumentObjectGroupPython] H_element104  label="H_element : 055"  # scripted group (container) (typed FeaturePython)
  n = 8
  ref = H_element
FEATURE [App::DocumentObjectGroupPython] G4_TOLUENE  # scripted group (container) (typed FeaturePython)
  Dunit = g/cm3
  Dvalue = 0.8669
  Group = -> [C_element114,H_element104]
  conduct = 2
  density = 1
  expand = 3
  formula = G4_TOLUENE
  name = G4_TOLUENE
  specific = 4
FEATURE [App::DocumentObjectGroupPython] C_element115  label="C_element : 062"  # scripted group (container) (typed FeaturePython)
  n = 2
  ref = C_element
FEATURE [App::DocumentObjectGroupPython] H_element105  label="H_element : 056"  # scripted group (container) (typed FeaturePython)
  n = 1
  ref = H_element
FEATURE [App::DocumentObjectGroupPython] Cl_element028  label="Cl_element : 014"  # scripted group (container) (typed FeaturePython)
  n = 3
  ref = Cl_element
FEATURE [App::DocumentObjectGroupPython] G4_TRICHLOROETHYLENE  # scripted group (container) (typed FeaturePython)
  Dunit = g/cm3
  Dvalue = 1.46
  Group = -> [C_element115,H_element105,Cl_element028]
  conduct = 2
  density = 1
  expand = 3
  formula = G4_TRICHLOROETHYLENE
  name = G4_TRICHLOROETHYLENE
  specific = 4
FEATURE [App::DocumentObjectGroupPython] C_element116  label="C_element : 063"  # scripted group (container) (typed FeaturePython)
  n = 6
  ref = C_element
FEATURE [App::DocumentObjectGroupPython] H_element106  label="H_element : 15"  # scripted group (container) (typed FeaturePython)
  n = 15
  ref = H_element
FEATURE [App::DocumentObjectGroupPython] O_element099  label="O_element : 053"  # scripted group (container) (typed FeaturePython)
  n = 4
  ref = O_element
FEATURE [App::DocumentObjectGroupPython] P_element012  label="P_element : 1"  # scripted group (container) (typed FeaturePython)
  n = 1
  ref = P_element
FEATURE [App::DocumentObjectGroupPython] G4_TRIETHYL_PHOSPHATE  # scripted group (container) (typed FeaturePython)
  Dunit = g/cm3
  Dvalue = 1.07
  Group = -> [C_element116,H_element106,O_element099,P_element012]
  conduct = 2
  density = 1
  expand = 3
  formula = G4_TRIETHYL_PHOSPHATE
  name = G4_TRIETHYL_PHOSPHATE
  specific = 4
FEATURE [App::DocumentObjectGroupPython] W_element003  label="W_element : 003"  # scripted group (container) (typed FeaturePython)
  n = 1
  ref = W_element
FEATURE [App::DocumentObjectGroupPython] F_element017  label="F_element : 6"  # scripted group (container) (typed FeaturePython)
  n = 6
  ref = F_element
FEATURE [App::DocumentObjectGroupPython] G4_TUNGSTEN_HEXAFLUORIDE  # scripted group (container) (typed FeaturePython)
  Dunit = g/cm3
  Dvalue = 2.4
  Group = -> [W_element003,F_element017]
  conduct = 2
  density = 1
  expand = 3
  formula = G4_TUNGSTEN_HEXAFLUORIDE
  name = G4_TUNGSTEN_HEXAFLUORIDE
  specific = 4
FEATURE [App::DocumentObjectGroupPython] U_element001  label="U_element : 1"  # scripted group (container) (typed FeaturePython)
  n = 1
  ref = U_element
FEATURE [App::DocumentObjectGroupPython] C_element117  label="C_element : 064"  # scripted group (container) (typed FeaturePython)
  n = 2
  ref = C_element
FEATURE [App::DocumentObjectGroupPython] G4_URANIUM_DICARBIDE  # scripted group (container) (typed FeaturePython)
  Dunit = g/cm3
  Dvalue = 11.28
  Group = -> [U_element001,C_element117]
  conduct = 2
  density = 1
  expand = 3
  formula = G4_URANIUM_DICARBIDE
  name = G4_URANIUM_DICARBIDE
  specific = 4
FEATURE [App::DocumentObjectGroupPython] U_element002  label="U_element : 002"  # scripted group (container) (typed FeaturePython)
  n = 1
  ref = U_element
FEATURE [App::DocumentObjectGroupPython] C_element118  label="C_element : 065"  # scripted group (container) (typed FeaturePython)
  n = 1
  ref = C_element
FEATURE [App::DocumentObjectGroupPython] G4_URANIUM_MONOCARBIDE  # scripted group (container) (typed FeaturePython)
  Dunit = g/cm3
  Dvalue = 13.63
  Group = -> [U_element002,C_element118]
  conduct = 2
  density = 1
  expand = 3
  formula = G4_URANIUM_MONOCARBIDE
  name = G4_URANIUM_MONOCARBIDE
  specific = 4
FEATURE [App::DocumentObjectGroupPython] U_element003  label="U_element : 003"  # scripted group (container) (typed FeaturePython)
  n = 1
  ref = U_element
FEATURE [App::DocumentObjectGroupPython] O_element100  label="O_element : 054"  # scripted group (container) (typed FeaturePython)
  n = 2
  ref = O_element
FEATURE [App::DocumentObjectGroupPython] G4_URANIUM_OXIDE  # scripted group (container) (typed FeaturePython)
  Dunit = g/cm3
  Dvalue = 10.96
  Group = -> [U_element003,O_element100]
  conduct = 2
  density = 1
  expand = 3
  formula = G4_URANIUM_OXIDE
  name = G4_URANIUM_OXIDE
  specific = 4
FEATURE [App::DocumentObjectGroupPython] C_element119  label="C_element : 066"  # scripted group (container) (typed FeaturePython)
  n = 1
  ref = C_element
FEATURE [App::DocumentObjectGroupPython] H_element107  label="H_element : 057"  # scripted group (container) (typed FeaturePython)
  n = 4
  ref = H_element
FEATURE [App::DocumentObjectGroupPython] N_element046  label="N_element : 019"  # scripted group (container) (typed FeaturePython)
  n = 2
  ref = N_element
FEATURE [App::DocumentObjectGroupPython] O_element101  label="O_element : 055"  # scripted group (container) (typed FeaturePython)
  n = 1
  ref = O_element
FEATURE [App::DocumentObjectGroupPython] G4_UREA  # scripted group (container) (typed FeaturePython)
  Dunit = g/cm3
  Dvalue = 1.323
  Group = -> [C_element119,H_element107,N_element046,O_element101]
  conduct = 2
  density = 1
  expand = 3
  formula = G4_UREA
  name = G4_UREA
  specific = 4
FEATURE [App::DocumentObjectGroupPython] C_element120  label="C_element : 067"  # scripted group (container) (typed FeaturePython)
  n = 5
  ref = C_element
FEATURE [App::DocumentObjectGroupPython] H_element108  label="H_element : 058"  # scripted group (container) (typed FeaturePython)
  n = 11
  ref = H_element
FEATURE [App::DocumentObjectGroupPython] N_element047  label="N_element : 020"  # scripted group (container) (typed FeaturePython)
  n = 1
  ref = N_element
FEATURE [App::DocumentObjectGroupPython] O_element102  label="O_element : 056"  # scripted group (container) (typed FeaturePython)
  n = 2
  ref = O_element
FEATURE [App::DocumentObjectGroupPython] G4_VALINE  # scripted group (container) (typed FeaturePython)
  Dunit = g/cm3
  Dvalue = 1.23
  Group = -> [C_element120,H_element108,N_element047,O_element102]
  conduct = 2
  density = 1
  expand = 3
  formula = G4_VALINE
  name = G4_VALINE
  specific = 4
FEATURE [App::DocumentObjectGroupPython] H_element109  label="H_element : 0.009"  # scripted group (container) (typed FeaturePython)
  n = 0.009417
FEATURE [App::DocumentObjectGroupPython] C_element121  label="C_element : 0.281"  # scripted group (container) (typed FeaturePython)
  n = 0.280555
FEATURE [App::DocumentObjectGroupPython] F_element018  label="F_element : 0.710"  # scripted group (container) (typed FeaturePython)
  n = 0.710028
FEATURE [App::DocumentObjectGroupPython] G4_VITON  # scripted group (container) (typed FeaturePython)
  Dunit = g/cm3
  Dvalue = 1.8
  Group = -> [H_element109,C_element121,F_element018]
  conduct = 2
  density = 1
  expand = 3
  formula = G4_VITON
  name = G4_VITON
  specific = 4
FEATURE [App::DocumentObjectGroupPython] H_element110  label="H_element : 059"  # scripted group (container) (typed FeaturePython)
  n = 2
  ref = H_element
FEATURE [App::DocumentObjectGroupPython] O_element103  label="O_element : 057"  # scripted group (container) (typed FeaturePython)
  n = 1
  ref = O_element
FEATURE [App::DocumentObjectGroupPython] G4_WATER  # scripted group (container) (typed FeaturePython)
  Dunit = g/cm3
  Dvalue = 1
  Group = -> [H_element110,O_element103]
  conduct = 2
  density = 1
  expand = 3
  formula = G4_WATER
  name = G4_WATER
  specific = 4
FEATURE [App::DocumentObjectGroupPython] H_element111  label="H_element : 060"  # scripted group (container) (typed FeaturePython)
  n = 2
  ref = H_element
FEATURE [App::DocumentObjectGroupPython] O_element104  label="O_element : 058"  # scripted group (container) (typed FeaturePython)
  n = 1
  ref = O_element
FEATURE [App::DocumentObjectGroupPython] G4_WATER_VAPOR  # scripted group (container) (typed FeaturePython)
  Dunit = g/cm3
  Dvalue = 0.000756182
  Group = -> [H_element111,O_element104]
  conduct = 2
  density = 1
  expand = 3
  formula = G4_WATER_VAPOR
  name = G4_WATER_VAPOR
  specific = 4
FEATURE [App::DocumentObjectGroupPython] C_element122  label="C_element : 068"  # scripted group (container) (typed FeaturePython)
  n = 8
  ref = C_element
FEATURE [App::DocumentObjectGroupPython] H_element112  label="H_element : 061"  # scripted group (container) (typed FeaturePython)
  n = 10
  ref = H_element
FEATURE [App::DocumentObjectGroupPython] G4_XYLENE  # scripted group (container) (typed FeaturePython)
  Dunit = g/cm3
  Dvalue = 0.87
  Group = -> [C_element122,H_element112]
  conduct = 2
  density = 1
  expand = 3
  formula = G4_XYLENE
  name = G4_XYLENE
  specific = 4
FEATURE [App::DocumentObjectGroupPython] C_element123  label="C_element : 069"  # scripted group (container) (typed FeaturePython)
  n = 1
  ref = C_element
FEATURE [App::DocumentObjectGroupPython] G4_GRAPHITE  # scripted group (container) (typed FeaturePython)
  Dunit = g/cm3
  Dvalue = 2.21
  Group = -> [C_element123]
  conduct = 2
  density = 1
  expand = 3
  formula = G4_GRAPHITE
  name = G4_GRAPHITE
  specific = 4
FEATURE [App::DocumentObjectGroupPython] NIST  # scripted group (container) (typed FeaturePython)
  Group = -> [G4_A_150_TISSUE,G4_ACETONE,G4_ACETYLENE,G4_ADENINE,G4_ADIPOSE_TISSUE_ICRP,G4_AIR,G4_ALANINE,G4_ALUMINUM_OXIDE,G4_AMBER,G4_AMMONIA,G4_ANILINE,G4_ANTHRACENE,G4_B_100_BONE,G4_BAKELITE,G4_BARIUM_FLUORIDE,G4_BARIUM_SULFATE,G4_BENZENE,G4_BERYLLIUM_OXIDE,G4_BGO,G4_BLOOD_ICRP,G4_BONE_COMPACT_ICRU,G4_BONE_CORTICAL_ICRP,G4_BORON_CARBIDE,G4_BORON_OXIDE,G4_BRAIN_ICRP,G4_BUTANE,G4_N_BUTYL_ALCOHOL,G4_C_552,+152 more]
FEATURE [App::DocumentObjectGroupPython] H_element113  label="H_element : 062"  # scripted group (container) (typed FeaturePython)
  n = 1
  ref = H_element
FEATURE [App::DocumentObjectGroupPython] G4_H  # scripted group (container) (typed FeaturePython)
  Dunit = g/cm3
  Dvalue = 8.3748e-05
  Group = -> [H_element113]
  conduct = 2
  density = 1
  expand = 3
  formula = H
  name = G4_H
  specific = 4
FEATURE [App::DocumentObjectGroupPython] He_element001  label="He_element : 1"  # scripted group (container) (typed FeaturePython)
  n = 1
  ref = He_element
FEATURE [App::DocumentObjectGroupPython] G4_He  # scripted group (container) (typed FeaturePython)
  Dunit = g/cm3
  Dvalue = 0.000166322
  Group = -> [He_element001]
  conduct = 2
  density = 1
  expand = 3
  formula = He
  name = G4_He
  specific = 4
FEATURE [App::DocumentObjectGroupPython] Li_element008  label="Li_element : 008"  # scripted group (container) (typed FeaturePython)
  n = 1
  ref = Li_element
FEATURE [App::DocumentObjectGroupPython] G4_Li  # scripted group (container) (typed FeaturePython)
  Dunit = g/cm3
  Dvalue = 0.534
  Group = -> [Li_element008]
  conduct = 2
  density = 1
  expand = 3
  formula = Li
  name = G4_Li
  specific = 4
FEATURE [App::DocumentObjectGroupPython] Be_element002  label="Be_element : 002"  # scripted group (container) (typed FeaturePython)
  n = 1
  ref = Be_element
FEATURE [App::DocumentObjectGroupPython] G4_Be  # scripted group (container) (typed FeaturePython)
  Dunit = g/cm3
  Dvalue = 1.848
  Group = -> [Be_element002]
  conduct = 2
  density = 1
  expand = 3
  formula = Be
  name = G4_Be
  specific = 4
FEATURE [App::DocumentObjectGroupPython] B_element007  label="B_element : 007"  # scripted group (container) (typed FeaturePython)
  n = 1
  ref = B_element
FEATURE [App::DocumentObjectGroupPython] G4_B  # scripted group (container) (typed FeaturePython)
  Dunit = g/cm3
  Dvalue = 2.37
  Group = -> [B_element007]
  conduct = 2
  density = 1
  expand = 3
  formula = B
  name = G4_B
  specific = 4
FEATURE [App::DocumentObjectGroupPython] C_element124  label="C_element : 070"  # scripted group (container) (typed FeaturePython)
  n = 1
  ref = C_element
FEATURE [App::DocumentObjectGroupPython] G4_C  # scripted group (container) (typed FeaturePython)
  Dunit = g/cm3
  Dvalue = 2
  Group = -> [C_element124]
  conduct = 2
  density = 1
  expand = 3
  formula = C
  name = G4_C
  specific = 4
FEATURE [App::DocumentObjectGroupPython] N_element048  label="N_element : 021"  # scripted group (container) (typed FeaturePython)
  n = 1
  ref = N_element
FEATURE [App::DocumentObjectGroupPython] G4_N  # scripted group (container) (typed FeaturePython)
  Dunit = g/cm3
  Dvalue = 0.0011652
  Group = -> [N_element048]
  conduct = 2
  density = 1
  expand = 3
  formula = N
  name = G4_N
  specific = 4
FEATURE [App::DocumentObjectGroupPython] O_element105  label="O_element : 059"  # scripted group (container) (typed FeaturePython)
  n = 1
  ref = O_element
FEATURE [App::DocumentObjectGroupPython] G4_O  # scripted group (container) (typed FeaturePython)
  Dunit = g/cm3
  Dvalue = 0.00133151
  Group = -> [O_element105]
  conduct = 2
  density = 1
  expand = 3
  formula = O
  name = G4_O
  specific = 4
FEATURE [App::DocumentObjectGroupPython] F_element019  label="F_element : 008"  # scripted group (container) (typed FeaturePython)
  n = 1
  ref = F_element
FEATURE [App::DocumentObjectGroupPython] G4_F  # scripted group (container) (typed FeaturePython)
  Dunit = g/cm3
  Dvalue = 0.00158029
  Group = -> [F_element019]
  conduct = 2
  density = 1
  expand = 3
  formula = F
  name = G4_F
  specific = 4
FEATURE [App::DocumentObjectGroupPython] Ne_element001  label="Ne_element : 1"  # scripted group (container) (typed FeaturePython)
  n = 1
  ref = Ne_element
FEATURE [App::DocumentObjectGroupPython] G4_Ne  # scripted group (container) (typed FeaturePython)
  Dunit = g/cm3
  Dvalue = 0.000838505
  Group = -> [Ne_element001]
  conduct = 2
  density = 1
  expand = 3
  formula = Ne
  name = G4_Ne
  specific = 4
FEATURE [App::DocumentObjectGroupPython] Na_element020  label="Na_element : 005"  # scripted group (container) (typed FeaturePython)
  n = 1
  ref = Na_element
FEATURE [App::DocumentObjectGroupPython] G4_Na  # scripted group (container) (typed FeaturePython)
  Dunit = g/cm3
  Dvalue = 0.971
  Group = -> [Na_element020]
  conduct = 2
  density = 1
  expand = 3
  formula = Na
  name = G4_Na
  specific = 4
FEATURE [App::DocumentObjectGroupPython] Mg_element011  label="Mg_element : 005"  # scripted group (container) (typed FeaturePython)
  n = 1
  ref = Mg_element
FEATURE [App::DocumentObjectGroupPython] G4_Mg  # scripted group (container) (typed FeaturePython)
  Dunit = g/cm3
  Dvalue = 1.74
  Group = -> [Mg_element011]
  conduct = 2
  density = 1
  expand = 3
  formula = Mg
  name = G4_Mg
  specific = 4
FEATURE [App::DocumentObjectGroupPython] Al_element004  label="Al_element : 1"  # scripted group (container) (typed FeaturePython)
  n = 1
  ref = Al_element
FEATURE [App::DocumentObjectGroupPython] G4_Al  # scripted group (container) (typed FeaturePython)
  Dunit = g/cm3
  Dvalue = 2.699
  Group = -> [Al_element004]
  conduct = 2
  density = 1
  expand = 3
  formula = Al
  name = G4_Al
  specific = 4
FEATURE [App::DocumentObjectGroupPython] Si_element007  label="Si_element : 002"  # scripted group (container) (typed FeaturePython)
  n = 1
  ref = Si_element
FEATURE [App::DocumentObjectGroupPython] G4_Si  # scripted group (container) (typed FeaturePython)
  Dunit = g/cm3
  Dvalue = 2.33
  Group = -> [Si_element007]
  conduct = 2
  density = 1
  expand = 3
  formula = Si
  name = G4_Si
  specific = 4
FEATURE [App::DocumentObjectGroupPython] P_element013  label="P_element : 002"  # scripted group (container) (typed FeaturePython)
  n = 1
  ref = P_element
FEATURE [App::DocumentObjectGroupPython] G4_P  # scripted group (container) (typed FeaturePython)
  Dunit = g/cm3
  Dvalue = 2.2
  Group = -> [P_element013]
  conduct = 2
  density = 1
  expand = 3
  formula = P
  name = G4_P
  specific = 4
FEATURE [App::DocumentObjectGroupPython] S_element023  label="S_element : 007"  # scripted group (container) (typed FeaturePython)
  n = 1
  ref = S_element
FEATURE [App::DocumentObjectGroupPython] G4_S  # scripted group (container) (typed FeaturePython)
  Dunit = g/cm3
  Dvalue = 2
  Group = -> [S_element023]
  conduct = 2
  density = 1
  expand = 3
  formula = S
  name = G4_S
  specific = 4
FEATURE [App::DocumentObjectGroupPython] Cl_element029  label="Cl_element : 015"  # scripted group (container) (typed FeaturePython)
  n = 1
  ref = Cl_element
FEATURE [App::DocumentObjectGroupPython] G4_Cl  # scripted group (container) (typed FeaturePython)
  Dunit = g/cm3
  Dvalue = 0.00299473
  Group = -> [Cl_element029]
  conduct = 2
  density = 1
  expand = 3
  formula = Cl
  name = G4_Cl
  specific = 4
FEATURE [App::DocumentObjectGroupPython] Ar_element002  label="Ar_element : 1"  # scripted group (container) (typed FeaturePython)
  n = 1
  ref = Ar_element
FEATURE [App::DocumentObjectGroupPython] G4_Ar  # scripted group (container) (typed FeaturePython)
  Dunit = g/cm3
  Dvalue = 0.00166201
  Group = -> [Ar_element002]
  conduct = 2
  density = 1
  expand = 3
  formula = Ar
  name = G4_Ar
  specific = 4
FEATURE [App::DocumentObjectGroupPython] K_element013  label="K_element : 003"  # scripted group (container) (typed FeaturePython)
  n = 1
  ref = K_element
FEATURE [App::DocumentObjectGroupPython] G4_K  # scripted group (container) (typed FeaturePython)
  Dunit = g/cm3
  Dvalue = 0.862
  Group = -> [K_element013]
  conduct = 2
  density = 1
  expand = 3
  formula = K
  name = G4_K
  specific = 4
FEATURE [App::DocumentObjectGroupPython] Ca_element014  label="Ca_element : 007"  # scripted group (container) (typed FeaturePython)
  n = 1
  ref = Ca_element
FEATURE [App::DocumentObjectGroupPython] G4_Ca  # scripted group (container) (typed FeaturePython)
  Dunit = g/cm3
  Dvalue = 1.55
  Group = -> [Ca_element014]
  conduct = 2
  density = 1
  expand = 3
  formula = Ca
  name = G4_Ca
  specific = 4
FEATURE [App::DocumentObjectGroupPython] Sc_element001  label="Sc_element : 1"  # scripted group (container) (typed FeaturePython)
  n = 1
  ref = Sc_element
FEATURE [App::DocumentObjectGroupPython] G4_Sc  # scripted group (container) (typed FeaturePython)
  Dunit = g/cm3
  Dvalue = 2.989
  Group = -> [Sc_element001]
  conduct = 2
  density = 1
  expand = 3
  formula = Sc
  name = G4_Sc
  specific = 4
FEATURE [App::DocumentObjectGroupPython] Ti_element004  label="Ti_element : 002"  # scripted group (container) (typed FeaturePython)
  n = 1
  ref = Ti_element
FEATURE [App::DocumentObjectGroupPython] G4_Ti  # scripted group (container) (typed FeaturePython)
  Dunit = g/cm3
  Dvalue = 4.54
  Group = -> [Ti_element004]
  conduct = 2
  density = 1
  expand = 3
  formula = Ti
  name = G4_Ti
  specific = 4
FEATURE [App::DocumentObjectGroupPython] V_element001  label="V_element : 1"  # scripted group (container) (typed FeaturePython)
  n = 1
  ref = V_element
FEATURE [App::DocumentObjectGroupPython] G4_V  # scripted group (container) (typed FeaturePython)
  Dunit = g/cm3
  Dvalue = 6.11
  Group = -> [V_element001]
  conduct = 2
  density = 1
  expand = 3
  formula = V
  name = G4_V
  specific = 4
FEATURE [App::DocumentObjectGroupPython] Cr_element001  label="Cr_element : 1"  # scripted group (container) (typed FeaturePython)
  n = 1
  ref = Cr_element
FEATURE [App::DocumentObjectGroupPython] G4_Cr  # scripted group (container) (typed FeaturePython)
  Dunit = g/cm3
  Dvalue = 7.18
  Group = -> [Cr_element001]
  conduct = 2
  density = 1
  expand = 3
  formula = Cr
  name = G4_Cr
  specific = 4
FEATURE [App::DocumentObjectGroupPython] Mn_element001  label="Mn_element : 1"  # scripted group (container) (typed FeaturePython)
  n = 1
  ref = Mn_element
FEATURE [App::DocumentObjectGroupPython] G4_Mn  # scripted group (container) (typed FeaturePython)
  Dunit = g/cm3
  Dvalue = 7.44
  Group = -> [Mn_element001]
  conduct = 2
  density = 1
  expand = 3
  formula = Mn
  name = G4_Mn
  specific = 4
FEATURE [App::DocumentObjectGroupPython] Fe_element007  label="Fe_element : 004"  # scripted group (container) (typed FeaturePython)
  n = 1
  ref = Fe_element
FEATURE [App::DocumentObjectGroupPython] G4_Fe  # scripted group (container) (typed FeaturePython)
  Dunit = g/cm3
  Dvalue = 7.874
  Group = -> [Fe_element007]
  conduct = 2
  density = 1
  expand = 3
  formula = Fe
  name = G4_Fe
  specific = 4
FEATURE [App::DocumentObjectGroupPython] Co_element001  label="Co_element : 1"  # scripted group (container) (typed FeaturePython)
  n = 1
  ref = Co_element
FEATURE [App::DocumentObjectGroupPython] G4_Co  # scripted group (container) (typed FeaturePython)
  Dunit = g/cm3
  Dvalue = 8.9
  Group = -> [Co_element001]
  conduct = 2
  density = 1
  expand = 3
  formula = Co
  name = G4_Co
  specific = 4
FEATURE [App::DocumentObjectGroupPython] Ni_element001  label="Ni_element : 1"  # scripted group (container) (typed FeaturePython)
  n = 1
  ref = Ni_element
FEATURE [App::DocumentObjectGroupPython] G4_Ni  # scripted group (container) (typed FeaturePython)
  Dunit = g/cm3
  Dvalue = 8.902
  Group = -> [Ni_element001]
  conduct = 2
  density = 1
  expand = 3
  formula = Ni
  name = G4_Ni
  specific = 4
FEATURE [App::DocumentObjectGroupPython] Cu_element001  label="Cu_element : 1"  # scripted group (container) (typed FeaturePython)
  n = 1
  ref = Cu_element
FEATURE [App::DocumentObjectGroupPython] G4_Cu  # scripted group (container) (typed FeaturePython)
  Dunit = g/cm3
  Dvalue = 8.96
  Group = -> [Cu_element001]
  conduct = 2
  density = 1
  expand = 3
  formula = Cu
  name = G4_Cu
  specific = 4
FEATURE [App::DocumentObjectGroupPython] Zn_element001  label="Zn_element : 1"  # scripted group (container) (typed FeaturePython)
  n = 1
  ref = Zn_element
FEATURE [App::DocumentObjectGroupPython] G4_Zn  # scripted group (container) (typed FeaturePython)
  Dunit = g/cm3
  Dvalue = 7.133
  Group = -> [Zn_element001]
  conduct = 2
  density = 1
  expand = 3
  formula = Zn
  name = G4_Zn
  specific = 4
FEATURE [App::DocumentObjectGroupPython] Ga_element002  label="Ga_element : 002"  # scripted group (container) (typed FeaturePython)
  n = 1
  ref = Ga_element
FEATURE [App::DocumentObjectGroupPython] G4_Ga  # scripted group (container) (typed FeaturePython)
  Dunit = g/cm3
  Dvalue = 5.904
  Group = -> [Ga_element002]
  conduct = 2
  density = 1
  expand = 3
  formula = Ga
  name = G4_Ga
  specific = 4
FEATURE [App::DocumentObjectGroupPython] Ge_element002  label="Ge_element : 1"  # scripted group (container) (typed FeaturePython)
  n = 1
  ref = Ge_element
FEATURE [App::DocumentObjectGroupPython] G4_Ge  # scripted group (container) (typed FeaturePython)
  Dunit = g/cm3
  Dvalue = 5.323
  Group = -> [Ge_element002]
  conduct = 2
  density = 1
  expand = 3
  formula = Ge
  name = G4_Ge
  specific = 4
FEATURE [App::DocumentObjectGroupPython] As_element003  label="As_element : 002"  # scripted group (container) (typed FeaturePython)
  n = 1
  ref = As_element
FEATURE [App::DocumentObjectGroupPython] G4_As  # scripted group (container) (typed FeaturePython)
  Dunit = g/cm3
  Dvalue = 5.73
  Group = -> [As_element003]
  conduct = 2
  density = 1
  expand = 3
  formula = As
  name = G4_As
  specific = 4
FEATURE [App::DocumentObjectGroupPython] Se_element001  label="Se_element : 1"  # scripted group (container) (typed FeaturePython)
  n = 1
  ref = Se_element
FEATURE [App::DocumentObjectGroupPython] G4_Se  # scripted group (container) (typed FeaturePython)
  Dunit = g/cm3
  Dvalue = 4.5
  Group = -> [Se_element001]
  conduct = 2
  density = 1
  expand = 3
  formula = Se
  name = G4_Se
  specific = 4
FEATURE [App::DocumentObjectGroupPython] Br_element007  label="Br_element : 004"  # scripted group (container) (typed FeaturePython)
  n = 1
  ref = Br_element
FEATURE [App::DocumentObjectGroupPython] G4_Br  # scripted group (container) (typed FeaturePython)
  Dunit = g/cm3
  Dvalue = 0.0070721
  Group = -> [Br_element007]
  conduct = 2
  density = 1
  expand = 3
  formula = Br
  name = G4_Br
  specific = 4
FEATURE [App::DocumentObjectGroupPython] Kr_element001  label="Kr_element : 1"  # scripted group (container) (typed FeaturePython)
  n = 1
  ref = Kr_element
FEATURE [App::DocumentObjectGroupPython] G4_Kr  # scripted group (container) (typed FeaturePython)
  Dunit = g/cm3
  Dvalue = 0.00347832
  Group = -> [Kr_element001]
  conduct = 2
  density = 1
  expand = 3
  formula = Kr
  name = G4_Kr
  specific = 4
FEATURE [App::DocumentObjectGroupPython] Rb_element001  label="Rb_element : 1"  # scripted group (container) (typed FeaturePython)
  n = 1
  ref = Rb_element
FEATURE [App::DocumentObjectGroupPython] G4_Rb  # scripted group (container) (typed FeaturePython)
  Dunit = g/cm3
  Dvalue = 1.532
  Group = -> [Rb_element001]
  conduct = 2
  density = 1
  expand = 3
  formula = Rb
  name = G4_Rb
  specific = 4
FEATURE [App::DocumentObjectGroupPython] Sr_element001  label="Sr_element : 1"  # scripted group (container) (typed FeaturePython)
  n = 1
  ref = Sr_element
FEATURE [App::DocumentObjectGroupPython] G4_Sr  # scripted group (container) (typed FeaturePython)
  Dunit = g/cm3
  Dvalue = 2.54
  Group = -> [Sr_element001]
  conduct = 2
  density = 1
  expand = 3
  formula = Sr
  name = G4_Sr
  specific = 4
FEATURE [App::DocumentObjectGroupPython] Y_element001  label="Y_element : 1"  # scripted group (container) (typed FeaturePython)
  n = 1
  ref = Y_element
FEATURE [App::DocumentObjectGroupPython] G4_Y  # scripted group (container) (typed FeaturePython)
  Dunit = g/cm3
  Dvalue = 4.469
  Group = -> [Y_element001]
  conduct = 2
  density = 1
  expand = 3
  formula = Y
  name = G4_Y
  specific = 4
FEATURE [App::DocumentObjectGroupPython] Zr_element001  label="Zr_element : 1"  # scripted group (container) (typed FeaturePython)
  n = 1
  ref = Zr_element
FEATURE [App::DocumentObjectGroupPython] G4_Zr  # scripted group (container) (typed FeaturePython)
  Dunit = g/cm3
  Dvalue = 6.506
  Group = -> [Zr_element001]
  conduct = 2
  density = 1
  expand = 3
  formula = Zr
  name = G4_Zr
  specific = 4
FEATURE [App::DocumentObjectGroupPython] Nb_element001  label="Nb_element : 1"  # scripted group (container) (typed FeaturePython)
  n = 1
  ref = Nb_element
FEATURE [App::DocumentObjectGroupPython] G4_Nb  # scripted group (container) (typed FeaturePython)
  Dunit = g/cm3
  Dvalue = 8.57
  Group = -> [Nb_element001]
  conduct = 2
  density = 1
  expand = 3
  formula = Nb
  name = G4_Nb
  specific = 4
FEATURE [App::DocumentObjectGroupPython] Mo_element001  label="Mo_element : 1"  # scripted group (container) (typed FeaturePython)
  n = 1
  ref = Mo_element
FEATURE [App::DocumentObjectGroupPython] G4_Mo  # scripted group (container) (typed FeaturePython)
  Dunit = g/cm3
  Dvalue = 10.22
  Group = -> [Mo_element001]
  conduct = 2
  density = 1
  expand = 3
  formula = Mo
  name = G4_Mo
  specific = 4
FEATURE [App::DocumentObjectGroupPython] Tc_element001  label="Tc_element : 1"  # scripted group (container) (typed FeaturePython)
  n = 1
  ref = Tc_element
FEATURE [App::DocumentObjectGroupPython] G4_Tc  # scripted group (container) (typed FeaturePython)
  Dunit = g/cm3
  Dvalue = 11.5
  Group = -> [Tc_element001]
  conduct = 2
  density = 1
  expand = 3
  formula = Tc
  name = G4_Tc
  specific = 4
FEATURE [App::DocumentObjectGroupPython] Ru_element001  label="Ru_element : 1"  # scripted group (container) (typed FeaturePython)
  n = 1
  ref = Ru_element
FEATURE [App::DocumentObjectGroupPython] G4_Ru  # scripted group (container) (typed FeaturePython)
  Dunit = g/cm3
  Dvalue = 12.41
  Group = -> [Ru_element001]
  conduct = 2
  density = 1
  expand = 3
  formula = Ru
  name = G4_Ru
  specific = 4
FEATURE [App::DocumentObjectGroupPython] Rh_element001  label="Rh_element : 1"  # scripted group (container) (typed FeaturePython)
  n = 1
  ref = Rh_element
FEATURE [App::DocumentObjectGroupPython] G4_Rh  # scripted group (container) (typed FeaturePython)
  Dunit = g/cm3
  Dvalue = 12.41
  Group = -> [Rh_element001]
  conduct = 2
  density = 1
  expand = 3
  formula = Rh
  name = G4_Rh
  specific = 4
FEATURE [App::DocumentObjectGroupPython] Pd_element001  label="Pd_element : 1"  # scripted group (container) (typed FeaturePython)
  n = 1
  ref = Pd_element
FEATURE [App::DocumentObjectGroupPython] G4_Pd  # scripted group (container) (typed FeaturePython)
  Dunit = g/cm3
  Dvalue = 12.02
  Group = -> [Pd_element001]
  conduct = 2
  density = 1
  expand = 3
  formula = Pd
  name = G4_Pd
  specific = 4
FEATURE [App::DocumentObjectGroupPython] Ag_element006  label="Ag_element : 004"  # scripted group (container) (typed FeaturePython)
  n = 1
  ref = Ag_element
FEATURE [App::DocumentObjectGroupPython] G4_Ag  # scripted group (container) (typed FeaturePython)
  Dunit = g/cm3
  Dvalue = 10.5
  Group = -> [Ag_element006]
  conduct = 2
  density = 1
  expand = 3
  formula = Ag
  name = G4_Ag
  specific = 4
FEATURE [App::DocumentObjectGroupPython] Cd_element003  label="Cd_element : 003"  # scripted group (container) (typed FeaturePython)
  n = 1
  ref = Cd_element
FEATURE [App::DocumentObjectGroupPython] G4_Cd  # scripted group (container) (typed FeaturePython)
  Dunit = g/cm3
  Dvalue = 8.65
  Group = -> [Cd_element003]
  conduct = 2
  density = 1
  expand = 3
  formula = Cd
  name = G4_Cd
  specific = 4
FEATURE [App::DocumentObjectGroupPython] In_element001  label="In_element : 1"  # scripted group (container) (typed FeaturePython)
  n = 1
  ref = In_element
FEATURE [App::DocumentObjectGroupPython] G4_In  # scripted group (container) (typed FeaturePython)
  Dunit = g/cm3
  Dvalue = 7.31
  Group = -> [In_element001]
  conduct = 2
  density = 1
  expand = 3
  formula = In
  name = G4_In
  specific = 4
FEATURE [App::DocumentObjectGroupPython] Sn_element001  label="Sn_element : 1"  # scripted group (container) (typed FeaturePython)
  n = 1
  ref = Sn_element
FEATURE [App::DocumentObjectGroupPython] G4_Sn  # scripted group (container) (typed FeaturePython)
  Dunit = g/cm3
  Dvalue = 7.31
  Group = -> [Sn_element001]
  conduct = 2
  density = 1
  expand = 3
  formula = Sn
  name = G4_Sn
  specific = 4
FEATURE [App::DocumentObjectGroupPython] Sb_element001  label="Sb_element : 1"  # scripted group (container) (typed FeaturePython)
  n = 1
  ref = Sb_element
FEATURE [App::DocumentObjectGroupPython] G4_Sb  # scripted group (container) (typed FeaturePython)
  Dunit = g/cm3
  Dvalue = 6.691
  Group = -> [Sb_element001]
  conduct = 2
  density = 1
  expand = 3
  formula = Sb
  name = G4_Sb
  specific = 4
FEATURE [App::DocumentObjectGroupPython] Te_element002  label="Te_element : 002"  # scripted group (container) (typed FeaturePython)
  n = 1
  ref = Te_element
FEATURE [App::DocumentObjectGroupPython] G4_Te  # scripted group (container) (typed FeaturePython)
  Dunit = g/cm3
  Dvalue = 6.24
  Group = -> [Te_element002]
  conduct = 2
  density = 1
  expand = 3
  formula = Te
  name = G4_Te
  specific = 4
FEATURE [App::DocumentObjectGroupPython] I_element010  label="I_element : 006"  # scripted group (container) (typed FeaturePython)
  n = 1
  ref = I_element
FEATURE [App::DocumentObjectGroupPython] G4_I  # scripted group (container) (typed FeaturePython)
  Dunit = g/cm3
  Dvalue = 4.93
  Group = -> [I_element010]
  conduct = 2
  density = 1
  expand = 3
  formula = I
  name = G4_I
  specific = 4
FEATURE [App::DocumentObjectGroupPython] Xe_element001  label="Xe_element : 1"  # scripted group (container) (typed FeaturePython)
  n = 1
  ref = Xe_element
FEATURE [App::DocumentObjectGroupPython] G4_Xe  # scripted group (container) (typed FeaturePython)
  Dunit = g/cm3
  Dvalue = 0.00548536
  Group = -> [Xe_element001]
  conduct = 2
  density = 1
  expand = 3
  formula = Xe
  name = G4_Xe
  specific = 4
FEATURE [App::DocumentObjectGroupPython] Cs_element003  label="Cs_element : 003"  # scripted group (container) (typed FeaturePython)
  n = 1
  ref = Cs_element
FEATURE [App::DocumentObjectGroupPython] G4_Cs  # scripted group (container) (typed FeaturePython)
  Dunit = g/cm3
  Dvalue = 1.873
  Group = -> [Cs_element003]
  conduct = 2
  density = 1
  expand = 3
  formula = Cs
  name = G4_Cs
  specific = 4
FEATURE [App::DocumentObjectGroupPython] Ba_element003  label="Ba_element : 003"  # scripted group (container) (typed FeaturePython)
  n = 1
  ref = Ba_element
FEATURE [App::DocumentObjectGroupPython] G4_Ba  # scripted group (container) (typed FeaturePython)
  Dunit = g/cm3
  Dvalue = 3.5
  Group = -> [Ba_element003]
  conduct = 2
  density = 1
  expand = 3
  formula = Ba
  name = G4_Ba
  specific = 4
FEATURE [App::DocumentObjectGroupPython] La_element003  label="La_element : 003"  # scripted group (container) (typed FeaturePython)
  n = 1
  ref = La_element
FEATURE [App::DocumentObjectGroupPython] G4_La  # scripted group (container) (typed FeaturePython)
  Dunit = g/cm3
  Dvalue = 6.154
  Group = -> [La_element003]
  conduct = 2
  density = 1
  expand = 3
  formula = La
  name = G4_La
  specific = 4
FEATURE [App::DocumentObjectGroupPython] Ce_element002  label="Ce_element : 1"  # scripted group (container) (typed FeaturePython)
  n = 1
  ref = Ce_element
FEATURE [App::DocumentObjectGroupPython] G4_Ce  # scripted group (container) (typed FeaturePython)
  Dunit = g/cm3
  Dvalue = 6.657
  Group = -> [Ce_element002]
  conduct = 2
  density = 1
  expand = 3
  formula = Ce
  name = G4_Ce
  specific = 4
FEATURE [App::DocumentObjectGroupPython] Pr_element001  label="Pr_element : 1"  # scripted group (container) (typed FeaturePython)
  n = 1
  ref = Pr_element
FEATURE [App::DocumentObjectGroupPython] G4_Pr  # scripted group (container) (typed FeaturePython)
  Dunit = g/cm3
  Dvalue = 6.71
  Group = -> [Pr_element001]
  conduct = 2
  density = 1
  expand = 3
  formula = Pr
  name = G4_Pr
  specific = 4
FEATURE [App::DocumentObjectGroupPython] Nd_element001  label="Nd_element : 1"  # scripted group (container) (typed FeaturePython)
  n = 1
  ref = Nd_element
FEATURE [App::DocumentObjectGroupPython] G4_Nd  # scripted group (container) (typed FeaturePython)
  Dunit = g/cm3
  Dvalue = 6.9
  Group = -> [Nd_element001]
  conduct = 2
  density = 1
  expand = 3
  formula = Nd
  name = G4_Nd
  specific = 4
FEATURE [App::DocumentObjectGroupPython] Pm_element001  label="Pm_element : 1"  # scripted group (container) (typed FeaturePython)
  n = 1
  ref = Pm_element
FEATURE [App::DocumentObjectGroupPython] G4_Pm  # scripted group (container) (typed FeaturePython)
  Dunit = g/cm3
  Dvalue = 7.22
  Group = -> [Pm_element001]
  conduct = 2
  density = 1
  expand = 3
  formula = Pm
  name = G4_Pm
  specific = 4
FEATURE [App::DocumentObjectGroupPython] Sm_element001  label="Sm_element : 1"  # scripted group (container) (typed FeaturePython)
  n = 1
  ref = Sm_element
FEATURE [App::DocumentObjectGroupPython] G4_Sm  # scripted group (container) (typed FeaturePython)
  Dunit = g/cm3
  Dvalue = 7.46
  Group = -> [Sm_element001]
  conduct = 2
  density = 1
  expand = 3
  formula = Sm
  name = G4_Sm
  specific = 4
FEATURE [App::DocumentObjectGroupPython] Eu_element001  label="Eu_element : 1"  # scripted group (container) (typed FeaturePython)
  n = 1
  ref = Eu_element
FEATURE [App::DocumentObjectGroupPython] G4_Eu  # scripted group (container) (typed FeaturePython)
  Dunit = g/cm3
  Dvalue = 5.243
  Group = -> [Eu_element001]
  conduct = 2
  density = 1
  expand = 3
  formula = Eu
  name = G4_Eu
  specific = 4
FEATURE [App::DocumentObjectGroupPython] Gd_element002  label="Gd_element : 1"  # scripted group (container) (typed FeaturePython)
  n = 1
  ref = Gd_element
FEATURE [App::DocumentObjectGroupPython] G4_Gd  # scripted group (container) (typed FeaturePython)
  Dunit = g/cm3
  Dvalue = 7.9004
  Group = -> [Gd_element002]
  conduct = 2
  density = 1
  expand = 3
  formula = Gd
  name = G4_Gd
  specific = 4
FEATURE [App::DocumentObjectGroupPython] Tb_element001  label="Tb_element : 1"  # scripted group (container) (typed FeaturePython)
  n = 1
  ref = Tb_element
FEATURE [App::DocumentObjectGroupPython] G4_Tb  # scripted group (container) (typed FeaturePython)
  Dunit = g/cm3
  Dvalue = 8.229
  Group = -> [Tb_element001]
  conduct = 2
  density = 1
  expand = 3
  formula = Tb
  name = G4_Tb
  specific = 4
FEATURE [App::DocumentObjectGroupPython] Dy_element001  label="Dy_element : 1"  # scripted group (container) (typed FeaturePython)
  n = 1
  ref = Dy_element
FEATURE [App::DocumentObjectGroupPython] G4_Dy  # scripted group (container) (typed FeaturePython)
  Dunit = g/cm3
  Dvalue = 8.55
  Group = -> [Dy_element001]
  conduct = 2
  density = 1
  expand = 3
  formula = Dy
  name = G4_Dy
  specific = 4
FEATURE [App::DocumentObjectGroupPython] Ho_element001  label="Ho_element : 1"  # scripted group (container) (typed FeaturePython)
  n = 1
  ref = Ho_element
FEATURE [App::DocumentObjectGroupPython] G4_Ho  # scripted group (container) (typed FeaturePython)
  Dunit = g/cm3
  Dvalue = 8.795
  Group = -> [Ho_element001]
  conduct = 2
  density = 1
  expand = 3
  formula = Ho
  name = G4_Ho
  specific = 4
FEATURE [App::DocumentObjectGroupPython] Er_element001  label="Er_element : 1"  # scripted group (container) (typed FeaturePython)
  n = 1
  ref = Er_element
FEATURE [App::DocumentObjectGroupPython] G4_Er  # scripted group (container) (typed FeaturePython)
  Dunit = g/cm3
  Dvalue = 9.066
  Group = -> [Er_element001]
  conduct = 2
  density = 1
  expand = 3
  formula = Er
  name = G4_Er
  specific = 4
FEATURE [App::DocumentObjectGroupPython] Tm_element001  label="Tm_element : 1"  # scripted group (container) (typed FeaturePython)
  n = 1
  ref = Tm_element
FEATURE [App::DocumentObjectGroupPython] G4_Tm  # scripted group (container) (typed FeaturePython)
  Dunit = g/cm3
  Dvalue = 9.321
  Group = -> [Tm_element001]
  conduct = 2
  density = 1
  expand = 3
  formula = Tm
  name = G4_Tm
  specific = 4
FEATURE [App::DocumentObjectGroupPython] Yb_element001  label="Yb_element : 1"  # scripted group (container) (typed FeaturePython)
  n = 1
  ref = Yb_element
FEATURE [App::DocumentObjectGroupPython] G4_Yb  # scripted group (container) (typed FeaturePython)
  Dunit = g/cm3
  Dvalue = 6.73
  Group = -> [Yb_element001]
  conduct = 2
  density = 1
  expand = 3
  formula = Yb
  name = G4_Yb
  specific = 4
FEATURE [App::DocumentObjectGroupPython] Lu_element001  label="Lu_element : 1"  # scripted group (container) (typed FeaturePython)
  n = 1
  ref = Lu_element
FEATURE [App::DocumentObjectGroupPython] G4_Lu  # scripted group (container) (typed FeaturePython)
  Dunit = g/cm3
  Dvalue = 9.84
  Group = -> [Lu_element001]
  conduct = 2
  density = 1
  expand = 3
  formula = Lu
  name = G4_Lu
  specific = 4
FEATURE [App::DocumentObjectGroupPython] Hf_element001  label="Hf_element : 1"  # scripted group (container) (typed FeaturePython)
  n = 1
  ref = Hf_element
FEATURE [App::DocumentObjectGroupPython] G4_Hf  # scripted group (container) (typed FeaturePython)
  Dunit = g/cm3
  Dvalue = 13.31
  Group = -> [Hf_element001]
  conduct = 2
  density = 1
  expand = 3
  formula = Hf
  name = G4_Hf
  specific = 4
FEATURE [App::DocumentObjectGroupPython] Ta_element001  label="Ta_element : 1"  # scripted group (container) (typed FeaturePython)
  n = 1
  ref = Ta_element
FEATURE [App::DocumentObjectGroupPython] G4_Ta  # scripted group (container) (typed FeaturePython)
  Dunit = g/cm3
  Dvalue = 16.654
  Group = -> [Ta_element001]
  conduct = 2
  density = 1
  expand = 3
  formula = Ta
  name = G4_Ta
  specific = 4
FEATURE [App::DocumentObjectGroupPython] W_element004  label="W_element : 004"  # scripted group (container) (typed FeaturePython)
  n = 1
  ref = W_element
FEATURE [App::DocumentObjectGroupPython] G4_W  # scripted group (container) (typed FeaturePython)
  Dunit = g/cm3
  Dvalue = 19.3
  Group = -> [W_element004]
  conduct = 2
  density = 1
  expand = 3
  formula = W
  name = G4_W
  specific = 4
FEATURE [App::DocumentObjectGroupPython] Re_element001  label="Re_element : 1"  # scripted group (container) (typed FeaturePython)
  n = 1
  ref = Re_element
FEATURE [App::DocumentObjectGroupPython] G4_Re  # scripted group (container) (typed FeaturePython)
  Dunit = g/cm3
  Dvalue = 21.02
  Group = -> [Re_element001]
  conduct = 2
  density = 1
  expand = 3
  formula = Re
  name = G4_Re
  specific = 4
FEATURE [App::DocumentObjectGroupPython] Os_element001  label="Os_element : 1"  # scripted group (container) (typed FeaturePython)
  n = 1
  ref = Os_element
FEATURE [App::DocumentObjectGroupPython] G4_Os  # scripted group (container) (typed FeaturePython)
  Dunit = g/cm3
  Dvalue = 22.57
  Group = -> [Os_element001]
  conduct = 2
  density = 1
  expand = 3
  formula = Os
  name = G4_Os
  specific = 4
FEATURE [App::DocumentObjectGroupPython] Ir_element001  label="Ir_element : 1"  # scripted group (container) (typed FeaturePython)
  n = 1
  ref = Ir_element
FEATURE [App::DocumentObjectGroupPython] G4_Ir  # scripted group (container) (typed FeaturePython)
  Dunit = g/cm3
  Dvalue = 22.42
  Group = -> [Ir_element001]
  conduct = 2
  density = 1
  expand = 3
  formula = Ir
  name = G4_Ir
  specific = 4
FEATURE [App::DocumentObjectGroupPython] Pt_element001  label="Pt_element : 1"  # scripted group (container) (typed FeaturePython)
  n = 1
  ref = Pt_element
FEATURE [App::DocumentObjectGroupPython] G4_Pt  # scripted group (container) (typed FeaturePython)
  Dunit = g/cm3
  Dvalue = 21.45
  Group = -> [Pt_element001]
  conduct = 2
  density = 1
  expand = 3
  formula = Pt
  name = G4_Pt
  specific = 4
FEATURE [App::DocumentObjectGroupPython] Au_element001  label="Au_element : 1"  # scripted group (container) (typed FeaturePython)
  n = 1
  ref = Au_element
FEATURE [App::DocumentObjectGroupPython] G4_Au  # scripted group (container) (typed FeaturePython)
  Dunit = g/cm3
  Dvalue = 19.32
  Group = -> [Au_element001]
  conduct = 2
  density = 1
  expand = 3
  formula = Au
  name = G4_Au
  specific = 4
FEATURE [App::DocumentObjectGroupPython] Hg_element002  label="Hg_element : 002"  # scripted group (container) (typed FeaturePython)
  n = 1
  ref = Hg_element
FEATURE [App::DocumentObjectGroupPython] G4_Hg  # scripted group (container) (typed FeaturePython)
  Dunit = g/cm3
  Dvalue = 13.546
  Group = -> [Hg_element002]
  conduct = 2
  density = 1
  expand = 3
  formula = Hg
  name = G4_Hg
  specific = 4
FEATURE [App::DocumentObjectGroupPython] Tl_element002  label="Tl_element : 002"  # scripted group (container) (typed FeaturePython)
  n = 1
  ref = Tl_element
FEATURE [App::DocumentObjectGroupPython] G4_Tl  # scripted group (container) (typed FeaturePython)
  Dunit = g/cm3
  Dvalue = 11.72
  Group = -> [Tl_element002]
  conduct = 2
  density = 1
  expand = 3
  formula = Tl
  name = G4_Tl
  specific = 4
FEATURE [App::DocumentObjectGroupPython] Pb_element003  label="Pb_element : 1"  # scripted group (container) (typed FeaturePython)
  n = 1
  ref = Pb_element
FEATURE [App::DocumentObjectGroupPython] G4_Pb  # scripted group (container) (typed FeaturePython)
  Dunit = g/cm3
  Dvalue = 11.35
  Group = -> [Pb_element003]
  conduct = 2
  density = 1
  expand = 3
  formula = Pb
  name = G4_Pb
  specific = 4
FEATURE [App::DocumentObjectGroupPython] Bi_element002  label="Bi_element : 1"  # scripted group (container) (typed FeaturePython)
  n = 1
  ref = Bi_element
FEATURE [App::DocumentObjectGroupPython] G4_Bi  # scripted group (container) (typed FeaturePython)
  Dunit = g/cm3
  Dvalue = 9.747
  Group = -> [Bi_element002]
  conduct = 2
  density = 1
  expand = 3
  formula = Bi
  name = G4_Bi
  specific = 4
FEATURE [App::DocumentObjectGroupPython] Po_element001  label="Po_element : 1"  # scripted group (container) (typed FeaturePython)
  n = 1
  ref = Po_element
FEATURE [App::DocumentObjectGroupPython] G4_Po  # scripted group (container) (typed FeaturePython)
  Dunit = g/cm3
  Dvalue = 9.32
  Group = -> [Po_element001]
  conduct = 2
  density = 1
  expand = 3
  formula = Po
  name = G4_Po
  specific = 4
FEATURE [App::DocumentObjectGroupPython] At_element001  label="At_element : 1"  # scripted group (container) (typed FeaturePython)
  n = 1
  ref = At_element
FEATURE [App::DocumentObjectGroupPython] G4_At  # scripted group (container) (typed FeaturePython)
  Dunit = g/cm3
  Dvalue = 9.32
  Group = -> [At_element001]
  conduct = 2
  density = 1
  expand = 3
  formula = At
  name = G4_At
  specific = 4
FEATURE [App::DocumentObjectGroupPython] Rn_element001  label="Rn_element : 1"  # scripted group (container) (typed FeaturePython)
  n = 1
  ref = Rn_element
FEATURE [App::DocumentObjectGroupPython] G4_Rn  # scripted group (container) (typed FeaturePython)
  Dunit = g/cm3
  Dvalue = 0.00900662
  Group = -> [Rn_element001]
  conduct = 2
  density = 1
  expand = 3
  formula = Rn
  name = G4_Rn
  specific = 4
FEATURE [App::DocumentObjectGroupPython] Fr_element001  label="Fr_element : 1"  # scripted group (container) (typed FeaturePython)
  n = 1
  ref = Fr_element
FEATURE [App::DocumentObjectGroupPython] G4_Fr  # scripted group (container) (typed FeaturePython)
  Dunit = g/cm3
  Dvalue = 1
  Group = -> [Fr_element001]
  conduct = 2
  density = 1
  expand = 3
  formula = Fr
  name = G4_Fr
  specific = 4
FEATURE [App::DocumentObjectGroupPython] Ra_element001  label="Ra_element : 1"  # scripted group (container) (typed FeaturePython)
  n = 1
  ref = Ra_element
FEATURE [App::DocumentObjectGroupPython] G4_Ra  # scripted group (container) (typed FeaturePython)
  Dunit = g/cm3
  Dvalue = 5
  Group = -> [Ra_element001]
  conduct = 2
  density = 1
  expand = 3
  formula = Ra
  name = G4_Ra
  specific = 4
FEATURE [App::DocumentObjectGroupPython] Ac_element001  label="Ac_element : 1"  # scripted group (container) (typed FeaturePython)
  n = 1
  ref = Ac_element
FEATURE [App::DocumentObjectGroupPython] G4_Ac  # scripted group (container) (typed FeaturePython)
  Dunit = g/cm3
  Dvalue = 10.07
  Group = -> [Ac_element001]
  conduct = 2
  density = 1
  expand = 3
  formula = Ac
  name = G4_Ac
  specific = 4
FEATURE [App::DocumentObjectGroupPython] Th_element001  label="Th_element : 1"  # scripted group (container) (typed FeaturePython)
  n = 1
  ref = Th_element
FEATURE [App::DocumentObjectGroupPython] G4_Th  # scripted group (container) (typed FeaturePython)
  Dunit = g/cm3
  Dvalue = 11.72
  Group = -> [Th_element001]
  conduct = 2
  density = 1
  expand = 3
  formula = Th
  name = G4_Th
  specific = 4
FEATURE [App::DocumentObjectGroupPython] Pa_element001  label="Pa_element : 1"  # scripted group (container) (typed FeaturePython)
  n = 1
  ref = Pa_element
FEATURE [App::DocumentObjectGroupPython] G4_Pa  # scripted group (container) (typed FeaturePython)
  Dunit = g/cm3
  Dvalue = 15.37
  Group = -> [Pa_element001]
  conduct = 2
  density = 1
  expand = 3
  formula = Pa
  name = G4_Pa
  specific = 4
FEATURE [App::DocumentObjectGroupPython] U_element004  label="U_element : 004"  # scripted group (container) (typed FeaturePython)
  n = 1
  ref = U_element
FEATURE [App::DocumentObjectGroupPython] G4_U  # scripted group (container) (typed FeaturePython)
  Dunit = g/cm3
  Dvalue = 18.95
  Group = -> [U_element004]
  conduct = 2
  density = 1
  expand = 3
  formula = U
  name = G4_U
  specific = 4
FEATURE [App::DocumentObjectGroupPython] Np_element001  label="Np_element : 1"  # scripted group (container) (typed FeaturePython)
  n = 1
  ref = Np_element
FEATURE [App::DocumentObjectGroupPython] G4_Np  # scripted group (container) (typed FeaturePython)
  Dunit = g/cm3
  Dvalue = 20.25
  Group = -> [Np_element001]
  conduct = 2
  density = 1
  expand = 3
  formula = Np
  name = G4_Np
  specific = 4
FEATURE [App::DocumentObjectGroupPython] Pu_element002  label="Pu_element : 002"  # scripted group (container) (typed FeaturePython)
  n = 1
  ref = Pu_element
FEATURE [App::DocumentObjectGroupPython] G4_Pu  # scripted group (container) (typed FeaturePython)
  Dunit = g/cm3
  Dvalue = 19.84
  Group = -> [Pu_element002]
  conduct = 2
  density = 1
  expand = 3
  formula = Pu
  name = G4_Pu
  specific = 4
FEATURE [App::DocumentObjectGroupPython] Am_element001  label="Am_element : 1"  # scripted group (container) (typed FeaturePython)
  n = 1
  ref = Am_element
FEATURE [App::DocumentObjectGroupPython] G4_Am  # scripted group (container) (typed FeaturePython)
  Dunit = g/cm3
  Dvalue = 13.67
  Group = -> [Am_element001]
  conduct = 2
  density = 1
  expand = 3
  formula = Am
  name = G4_Am
  specific = 4
FEATURE [App::DocumentObjectGroupPython] Cm_element001  label="Cm_element : 1"  # scripted group (container) (typed FeaturePython)
  n = 1
  ref = Cm_element
FEATURE [App::DocumentObjectGroupPython] G4_Cm  # scripted group (container) (typed FeaturePython)
  Dunit = g/cm3
  Dvalue = 13.51
  Group = -> [Cm_element001]
  conduct = 2
  density = 1
  expand = 3
  formula = Cm
  name = G4_Cm
  specific = 4
FEATURE [App::DocumentObjectGroupPython] Bk_element001  label="Bk_element : 1"  # scripted group (container) (typed FeaturePython)
  n = 1
  ref = Bk_element
FEATURE [App::DocumentObjectGroupPython] G4_Bk  # scripted group (container) (typed FeaturePython)
  Dunit = g/cm3
  Dvalue = 14
  Group = -> [Bk_element001]
  conduct = 2
  density = 1
  expand = 3
  formula = Bk
  name = G4_Bk
  specific = 4
FEATURE [App::DocumentObjectGroupPython] Cf_element001  label="Cf_element : 1"  # scripted group (container) (typed FeaturePython)
  n = 1
  ref = Cf_element
FEATURE [App::DocumentObjectGroupPython] G4_Cf  # scripted group (container) (typed FeaturePython)
  Dunit = g/cm3
  Dvalue = 10
  Group = -> [Cf_element001]
  conduct = 2
  density = 1
  expand = 3
  formula = Cf
  name = G4_Cf
  specific = 4
FEATURE [App::DocumentObjectGroupPython] Element  # scripted group (container) (typed FeaturePython)
  Group = -> [G4_H,G4_He,G4_Li,G4_Be,G4_B,G4_C,G4_N,G4_O,G4_F,G4_Ne,G4_Na,G4_Mg,G4_Al,G4_Si,G4_P,G4_S,G4_Cl,G4_Ar,G4_K,G4_Ca,G4_Sc,G4_Ti,G4_V,G4_Cr,G4_Mn,G4_Fe,G4_Co,G4_Ni,G4_Cu,G4_Zn,G4_Ga,G4_Ge,G4_As,G4_Se,G4_Br,G4_Kr,G4_Rb,G4_Sr,G4_Y,G4_Zr,G4_Nb,G4_Mo,G4_Tc,G4_Ru,G4_Rh,G4_Pd,G4_Ag,G4_Cd,G4_In,G4_Sn,G4_Sb,G4_Te,G4_I,G4_Xe,G4_Cs,G4_Ba,G4_La,G4_Ce,G4_Pr,G4_Nd,G4_Pm,G4_Sm,G4_Eu,G4_Gd,G4_Tb,G4_Dy,G4_Ho,G4_Er,+30 more]
FEATURE [App::DocumentObjectGroupPython] H_element114  label="H_element : 063"  # scripted group (container) (typed FeaturePython)
  n = 2
  ref = H_element
FEATURE [App::DocumentObjectGroupPython] G4_lH2  # scripted group (container) (typed FeaturePython)
  Dunit = g/cm3
  Dvalue = 0.0708
  Group = -> [H_element114]
  conduct = 2
  density = 1
  expand = 3
  formula = G4_lH2
  name = G4_lH2
  specific = 4
FEATURE [App::DocumentObjectGroupPython] N_element049  label="N_element : 022"  # scripted group (container) (typed FeaturePython)
  n = 2
  ref = N_element
FEATURE [App::DocumentObjectGroupPython] G4_lN2  # scripted group (container) (typed FeaturePython)
  Dunit = g/cm3
  Dvalue = 0.807
  Group = -> [N_element049]
  conduct = 2
  density = 1
  expand = 3
  formula = G4_lN2
  name = G4_lN2
  specific = 4
FEATURE [App::DocumentObjectGroupPython] O_element106  label="O_element : 060"  # scripted group (container) (typed FeaturePython)
  n = 2
  ref = O_element
FEATURE [App::DocumentObjectGroupPython] G4_lO2  # scripted group (container) (typed FeaturePython)
  Dunit = g/cm3
  Dvalue = 1.141
  Group = -> [O_element106]
  conduct = 2
  density = 1
  expand = 3
  formula = G4_lO2
  name = G4_lO2
  specific = 4
FEATURE [App::DocumentObjectGroupPython] Ar  label="Ar : 1"  # scripted group (container) (typed FeaturePython)
  n = 1
  ref = Ar
FEATURE [App::DocumentObjectGroupPython] G4_lAr  # scripted group (container) (typed FeaturePython)
  Dunit = g/cm3
  Dvalue = 1.396
  Group = -> [Ar]
  conduct = 2
  density = 1
  expand = 3
  formula = G4_lAr
  name = G4_lAr
  specific = 4
FEATURE [App::DocumentObjectGroupPython] Br  label="Br : 1"  # scripted group (container) (typed FeaturePython)
  n = 1
  ref = Br
FEATURE [App::DocumentObjectGroupPython] G4_lBr  # scripted group (container) (typed FeaturePython)
  Dunit = g/cm3
  Dvalue = 3.1028
  Group = -> [Br]
  conduct = 2
  density = 1
  expand = 3
  formula = G4_lBr
  name = G4_lBr
  specific = 4
FEATURE [App::DocumentObjectGroupPython] Kr  label="Kr : 1"  # scripted group (container) (typed FeaturePython)
  n = 1
  ref = Kr
FEATURE [App::DocumentObjectGroupPython] G4_lKr  # scripted group (container) (typed FeaturePython)
  Dunit = g/cm3
  Dvalue = 2.418
  Group = -> [Kr]
  conduct = 2
  density = 1
  expand = 3
  formula = G4_lKr
  name = G4_lKr
  specific = 4
FEATURE [App::DocumentObjectGroupPython] Xe  label="Xe : 1"  # scripted group (container) (typed FeaturePython)
  n = 1
  ref = Xe
FEATURE [App::DocumentObjectGroupPython] G4_lXe  # scripted group (container) (typed FeaturePython)
  Dunit = g/cm3
  Dvalue = 2.953
  Group = -> [Xe]
  conduct = 2
  density = 1
  expand = 3
  formula = G4_lXe
  name = G4_lXe
  specific = 4
FEATURE [App::DocumentObjectGroupPython] O_element107  label="O_element : 061"  # scripted group (container) (typed FeaturePython)
  n = 4
  ref = O_element
FEATURE [App::DocumentObjectGroupPython] Pb_element004  label="Pb_element : 002"  # scripted group (container) (typed FeaturePython)
  n = 1
  ref = Pb_element
FEATURE [App::DocumentObjectGroupPython] W_element005  label="W_element : 005"  # scripted group (container) (typed FeaturePython)
  n = 1
  ref = W_element
FEATURE [App::DocumentObjectGroupPython] G4_PbWO4  # scripted group (container) (typed FeaturePython)
  Dunit = g/cm3
  Dvalue = 8.28
  Group = -> [O_element107,Pb_element004,W_element005]
  conduct = 2
  density = 1
  expand = 3
  formula = G4_PbWO4
  name = G4_PbWO4
  specific = 4
FEATURE [App::DocumentObjectGroupPython] alactic  label="alactic : 1"  # scripted group (container) (typed FeaturePython)
  n = 1
  ref = alactic
FEATURE [App::DocumentObjectGroupPython] G4_Galactic  # scripted group (container) (typed FeaturePython)
  Dunit = g/cm3
  Dvalue = 0
  Group = -> [alactic]
  conduct = 2
  density = 1
  expand = 3
  formula = G4_Galactic
  name = G4_Galactic
  specific = 4
FEATURE [App::DocumentObjectGroupPython] RAPHITE_POROUS  label="RAPHITE_POROUS : 1"  # scripted group (container) (typed FeaturePython)
  n = 1
  ref = RAPHITE_POROUS
FEATURE [App::DocumentObjectGroupPython] G4_GRAPHITE_POROUS  # scripted group (container) (typed FeaturePython)
  Dunit = g/cm3
  Dvalue = 1.7
  Group = -> [RAPHITE_POROUS]
  conduct = 2
  density = 1
  expand = 3
  formula = G4_GRAPHITE_POROUS
  name = G4_GRAPHITE_POROUS
  specific = 4
FEATURE [App::DocumentObjectGroupPython] H_element115  label="H_element : 0.150"  # scripted group (container) (typed FeaturePython)
  n = 0.080538
FEATURE [App::DocumentObjectGroupPython] C_element125  label="C_element : 0.600"  # scripted group (container) (typed FeaturePython)
  n = 0.599848
FEATURE [App::DocumentObjectGroupPython] O_element108  label="O_element : 0.320"  # scripted group (container) (typed FeaturePython)
  n = 0.319614
FEATURE [App::DocumentObjectGroupPython] G4_LUCITE  # scripted group (container) (typed FeaturePython)
  Dunit = g/cm3
  Dvalue = 1.19
  Group = -> [H_element115,C_element125,O_element108]
  conduct = 2
  density = 1
  expand = 3
  formula = G4_LUCITE
  name = G4_LUCITE
  specific = 4
FEATURE [App::DocumentObjectGroupPython] Cu_element002  label="Cu_element : 62"  # scripted group (container) (typed FeaturePython)
  n = 62
  ref = Cu_element
FEATURE [App::DocumentObjectGroupPython] Zn_element002  label="Zn_element : 35"  # scripted group (container) (typed FeaturePython)
  n = 35
  ref = Zn_element
FEATURE [App::DocumentObjectGroupPython] Pb_element005  label="Pb_element : 3"  # scripted group (container) (typed FeaturePython)
  n = 3
  ref = Pb_element
FEATURE [App::DocumentObjectGroupPython] G4_BRASS  # scripted group (container) (typed FeaturePython)
  Dunit = g/cm3
  Dvalue = 8.52
  Group = -> [Cu_element002,Zn_element002,Pb_element005]
  conduct = 2
  density = 1
  expand = 3
  formula = G4_BRASS
  name = G4_BRASS
  specific = 4
FEATURE [App::DocumentObjectGroupPython] Cu_element003  label="Cu_element : 89"  # scripted group (container) (typed FeaturePython)
  n = 89
  ref = Cu_element
FEATURE [App::DocumentObjectGroupPython] Zn_element003  label="Zn_element : 9"  # scripted group (container) (typed FeaturePython)
  n = 9
  ref = Zn_element
FEATURE [App::DocumentObjectGroupPython] Pb_element006  label="Pb_element : 2"  # scripted group (container) (typed FeaturePython)
  n = 2
  ref = Pb_element
FEATURE [App::DocumentObjectGroupPython] G4_BRONZE  # scripted group (container) (typed FeaturePython)
  Dunit = g/cm3
  Dvalue = 8.82
  Group = -> [Cu_element003,Zn_element003,Pb_element006]
  conduct = 2
  density = 1
  expand = 3
  formula = G4_BRONZE
  name = G4_BRONZE
  specific = 4
FEATURE [App::DocumentObjectGroupPython] Fe_element008  label="Fe_element : 74"  # scripted group (container) (typed FeaturePython)
  n = 74
  ref = Fe_element
FEATURE [App::DocumentObjectGroupPython] Cr_element002  label="Cr_element : 18"  # scripted group (container) (typed FeaturePython)
  n = 18
  ref = Cr_element
FEATURE [App::DocumentObjectGroupPython] Ni_element002  label="Ni_element : 8"  # scripted group (container) (typed FeaturePython)
  n = 8
  ref = Ni_element
FEATURE [App::DocumentObjectGroupPython] G4_STAINLESS_STEEL  label="G4_STAINLESS-STEEL"  # scripted group (container) (typed FeaturePython)
  Dunit = g/cm3
  Dvalue = 8
  Group = -> [Fe_element008,Cr_element002,Ni_element002]
  conduct = 2
  density = 1
  expand = 3
  formula = G4_STAINLESS-STEEL
  name = G4_STAINLESS-STEEL
  specific = 4
FEATURE [App::DocumentObjectGroupPython] H_element116  label="H_element : 064"  # scripted group (container) (typed FeaturePython)
  n = 18
  ref = H_element
FEATURE [App::DocumentObjectGroupPython] C_element126  label="C_element : 071"  # scripted group (container) (typed FeaturePython)
  n = 12
  ref = C_element
FEATURE [App::DocumentObjectGroupPython] O_element109  label="O_element : 062"  # scripted group (container) (typed FeaturePython)
  n = 7
  ref = O_element
FEATURE [App::DocumentObjectGroupPython] G4_CR39  # scripted group (container) (typed FeaturePython)
  Dunit = g/cm3
  Dvalue = 1.32
  Group = -> [H_element116,C_element126,O_element109]
  conduct = 2
  density = 1
  expand = 3
  formula = G4_CR39
  name = G4_CR39
  specific = 4
FEATURE [App::DocumentObjectGroupPython] H_element117  label="H_element : 38"  # scripted group (container) (typed FeaturePython)
  n = 38
  ref = H_element
FEATURE [App::DocumentObjectGroupPython] C_element127  label="C_element : 072"  # scripted group (container) (typed FeaturePython)
  n = 18
  ref = C_element
FEATURE [App::DocumentObjectGroupPython] O_element110  label="O_element : 063"  # scripted group (container) (typed FeaturePython)
  n = 1
  ref = O_element
FEATURE [App::DocumentObjectGroupPython] G4_OCTADECANOL  # scripted group (container) (typed FeaturePython)
  Dunit = g/cm3
  Dvalue = 0.812
  Group = -> [H_element117,C_element127,O_element110]
  conduct = 2
  density = 1
  expand = 3
  formula = G4_OCTADECANOL
  name = G4_OCTADECANOL
  specific = 4
FEATURE [App::DocumentObjectGroupPython] HEP  # scripted group (container) (typed FeaturePython)
  Group = -> [G4_lH2,G4_lN2,G4_lO2,G4_lAr,G4_lBr,G4_lKr,G4_lXe,G4_PbWO4,G4_Galactic,G4_GRAPHITE_POROUS,G4_LUCITE,G4_BRASS,G4_BRONZE,G4_STAINLESS_STEEL,G4_CR39,G4_OCTADECANOL]
FEATURE [App::DocumentObjectGroupPython] C_element128  label="C_element : 073"  # scripted group (container) (typed FeaturePython)
  n = 14
  ref = C_element
FEATURE [App::DocumentObjectGroupPython] H_element118  label="H_element : 065"  # scripted group (container) (typed FeaturePython)
  n = 10
  ref = H_element
FEATURE [App::DocumentObjectGroupPython] O_element111  label="O_element : 064"  # scripted group (container) (typed FeaturePython)
  n = 2
  ref = O_element
FEATURE [App::DocumentObjectGroupPython] N_element050  label="N_element : 023"  # scripted group (container) (typed FeaturePython)
  n = 2
  ref = N_element
FEATURE [App::DocumentObjectGroupPython] G4_KEVLAR  # scripted group (container) (typed FeaturePython)
  Dunit = g/cm3
  Dvalue = 1.44
  Group = -> [C_element128,H_element118,O_element111,N_element050]
  conduct = 2
  density = 1
  expand = 3
  formula = G4_KEVLAR
  name = G4_KEVLAR
  specific = 4
FEATURE [App::DocumentObjectGroupPython] C_element129  label="C_element : 074"  # scripted group (container) (typed FeaturePython)
  n = 10
  ref = C_element
FEATURE [App::DocumentObjectGroupPython] H_element119  label="H_element : 066"  # scripted group (container) (typed FeaturePython)
  n = 8
  ref = H_element
FEATURE [App::DocumentObjectGroupPython] O_element112  label="O_element : 065"  # scripted group (container) (typed FeaturePython)
  n = 4
  ref = O_element
FEATURE [App::DocumentObjectGroupPython] G4_DACRON  # scripted group (container) (typed FeaturePython)
  Dunit = g/cm3
  Dvalue = 1.4
  Group = -> [C_element129,H_element119,O_element112]
  conduct = 2
  density = 1
  expand = 3
  formula = G4_DACRON
  name = G4_DACRON
  specific = 4
FEATURE [App::DocumentObjectGroupPython] C_element130  label="C_element : 075"  # scripted group (container) (typed FeaturePython)
  n = 4
  ref = C_element
FEATURE [App::DocumentObjectGroupPython] H_element120  label="H_element : 067"  # scripted group (container) (typed FeaturePython)
  n = 5
  ref = H_element
FEATURE [App::DocumentObjectGroupPython] Cl_element030  label="Cl_element : 016"  # scripted group (container) (typed FeaturePython)
  n = 1
  ref = Cl_element
FEATURE [App::DocumentObjectGroupPython] G4_NEOPRENE  # scripted group (container) (typed FeaturePython)
  Dunit = g/cm3
  Dvalue = 1.23
  Group = -> [C_element130,H_element120,Cl_element030]
  conduct = 2
  density = 1
  expand = 3
  formula = G4_NEOPRENE
  name = G4_NEOPRENE
  specific = 4
FEATURE [App::DocumentObjectGroupPython] Space  # scripted group (container) (typed FeaturePython)
  Group = -> [G4_KEVLAR,G4_DACRON,G4_NEOPRENE]
FEATURE [App::DocumentObjectGroupPython] H_element121  label="H_element : 068"  # scripted group (container) (typed FeaturePython)
  n = 5
  ref = H_element
FEATURE [App::DocumentObjectGroupPython] C_element131  label="C_element : 076"  # scripted group (container) (typed FeaturePython)
  n = 4
  ref = C_element
FEATURE [App::DocumentObjectGroupPython] N_element051  label="N_element : 3"  # scripted group (container) (typed FeaturePython)
  n = 3
  ref = N_element
FEATURE [App::DocumentObjectGroupPython] O_element113  label="O_element : 066"  # scripted group (container) (typed FeaturePython)
  n = 1
  ref = O_element
FEATURE [App::DocumentObjectGroupPython] G4_CYTOSINE  # scripted group (container) (typed FeaturePython)
  Dunit = g/cm3
  Dvalue = 1.55
  Group = -> [H_element121,C_element131,N_element051,O_element113]
  conduct = 2
  density = 1
  expand = 3
  formula = G4_CYTOSINE
  name = G4_CYTOSINE
  specific = 4
FEATURE [App::DocumentObjectGroupPython] H_element122  label="H_element : 069"  # scripted group (container) (typed FeaturePython)
  n = 6
  ref = H_element
FEATURE [App::DocumentObjectGroupPython] C_element132  label="C_element : 077"  # scripted group (container) (typed FeaturePython)
  n = 5
  ref = C_element
FEATURE [App::DocumentObjectGroupPython] N_element052  label="N_element : 024"  # scripted group (container) (typed FeaturePython)
  n = 2
  ref = N_element
FEATURE [App::DocumentObjectGroupPython] O_element114  label="O_element : 067"  # scripted group (container) (typed FeaturePython)
  n = 2
  ref = O_element
FEATURE [App::DocumentObjectGroupPython] G4_THYMINE  # scripted group (container) (typed FeaturePython)
  Dunit = g/cm3
  Dvalue = 1.23
  Group = -> [H_element122,C_element132,N_element052,O_element114]
  conduct = 2
  density = 1
  expand = 3
  formula = G4_THYMINE
  name = G4_THYMINE
  specific = 4
FEATURE [App::DocumentObjectGroupPython] H_element123  label="H_element : 070"  # scripted group (container) (typed FeaturePython)
  n = 4
  ref = H_element
FEATURE [App::DocumentObjectGroupPython] C_element133  label="C_element : 078"  # scripted group (container) (typed FeaturePython)
  n = 4
  ref = C_element
FEATURE [App::DocumentObjectGroupPython] N_element053  label="N_element : 025"  # scripted group (container) (typed FeaturePython)
  n = 2
  ref = N_element
FEATURE [App::DocumentObjectGroupPython] O_element115  label="O_element : 068"  # scripted group (container) (typed FeaturePython)
  n = 2
  ref = O_element
FEATURE [App::DocumentObjectGroupPython] G4_URACIL  # scripted group (container) (typed FeaturePython)
  Dunit = g/cm3
  Dvalue = 1.32
  Group = -> [H_element123,C_element133,N_element053,O_element115]
  conduct = 2
  density = 1
  expand = 3
  formula = G4_URACIL
  name = G4_URACIL
  specific = 4
FEATURE [App::DocumentObjectGroupPython] H_element124  label="H_element : 071"  # scripted group (container) (typed FeaturePython)
  n = 4
  ref = H_element
FEATURE [App::DocumentObjectGroupPython] C_element134  label="C_element : 079"  # scripted group (container) (typed FeaturePython)
  n = 5
  ref = C_element
FEATURE [App::DocumentObjectGroupPython] N_element054  label="N_element : 026"  # scripted group (container) (typed FeaturePython)
  n = 5
  ref = N_element
FEATURE [App::DocumentObjectGroupPython] G4_DNA_ADENINE  # scripted group (container) (typed FeaturePython)
  Dunit = g/cm3
  Dvalue = 1
  Group = -> [H_element124,C_element134,N_element054]
  conduct = 2
  density = 1
  expand = 3
  formula = G4_DNA_ADENINE
  name = G4_DNA_ADENINE
  specific = 4
FEATURE [App::DocumentObjectGroupPython] H_element125  label="H_element : 072"  # scripted group (container) (typed FeaturePython)
  n = 4
  ref = H_element
FEATURE [App::DocumentObjectGroupPython] C_element135  label="C_element : 080"  # scripted group (container) (typed FeaturePython)
  n = 5
  ref = C_element
FEATURE [App::DocumentObjectGroupPython] N_element055  label="N_element : 027"  # scripted group (container) (typed FeaturePython)
  n = 5
  ref = N_element
FEATURE [App::DocumentObjectGroupPython] O_element116  label="O_element : 069"  # scripted group (container) (typed FeaturePython)
  n = 1
  ref = O_element
FEATURE [App::DocumentObjectGroupPython] G4_DNA_GUANINE  # scripted group (container) (typed FeaturePython)
  Dunit = g/cm3
  Dvalue = 1
  Group = -> [H_element125,C_element135,N_element055,O_element116]
  conduct = 2
  density = 1
  expand = 3
  formula = G4_DNA_GUANINE
  name = G4_DNA_GUANINE
  specific = 4
FEATURE [App::DocumentObjectGroupPython] H_element126  label="H_element : 073"  # scripted group (container) (typed FeaturePython)
  n = 4
  ref = H_element
FEATURE [App::DocumentObjectGroupPython] C_element136  label="C_element : 081"  # scripted group (container) (typed FeaturePython)
  n = 4
  ref = C_element
FEATURE [App::DocumentObjectGroupPython] N_element056  label="N_element : 028"  # scripted group (container) (typed FeaturePython)
  n = 3
  ref = N_element
FEATURE [App::DocumentObjectGroupPython] O_element117  label="O_element : 070"  # scripted group (container) (typed FeaturePython)
  n = 1
  ref = O_element
FEATURE [App::DocumentObjectGroupPython] G4_DNA_CYTOSINE  # scripted group (container) (typed FeaturePython)
  Dunit = g/cm3
  Dvalue = 1
  Group = -> [H_element126,C_element136,N_element056,O_element117]
  conduct = 2
  density = 1
  expand = 3
  formula = G4_DNA_CYTOSINE
  name = G4_DNA_CYTOSINE
  specific = 4
FEATURE [App::DocumentObjectGroupPython] H_element127  label="H_element : 074"  # scripted group (container) (typed FeaturePython)
  n = 5
  ref = H_element
FEATURE [App::DocumentObjectGroupPython] C_element137  label="C_element : 082"  # scripted group (container) (typed FeaturePython)
  n = 5
  ref = C_element
FEATURE [App::DocumentObjectGroupPython] N_element057  label="N_element : 029"  # scripted group (container) (typed FeaturePython)
  n = 2
  ref = N_element
FEATURE [App::DocumentObjectGroupPython] O_element118  label="O_element : 071"  # scripted group (container) (typed FeaturePython)
  n = 2
  ref = O_element
FEATURE [App::DocumentObjectGroupPython] G4_DNA_THYMINE  # scripted group (container) (typed FeaturePython)
  Dunit = g/cm3
  Dvalue = 1
  Group = -> [H_element127,C_element137,N_element057,O_element118]
  conduct = 2
  density = 1
  expand = 3
  formula = G4_DNA_THYMINE
  name = G4_DNA_THYMINE
  specific = 4
FEATURE [App::DocumentObjectGroupPython] H_element128  label="H_element : 075"  # scripted group (container) (typed FeaturePython)
  n = 3
  ref = H_element
FEATURE [App::DocumentObjectGroupPython] C_element138  label="C_element : 083"  # scripted group (container) (typed FeaturePython)
  n = 4
  ref = C_element
FEATURE [App::DocumentObjectGroupPython] N_element058  label="N_element : 030"  # scripted group (container) (typed FeaturePython)
  n = 2
  ref = N_element
FEATURE [App::DocumentObjectGroupPython] O_element119  label="O_element : 072"  # scripted group (container) (typed FeaturePython)
  n = 2
  ref = O_element
FEATURE [App::DocumentObjectGroupPython] G4_DNA_URACIL  # scripted group (container) (typed FeaturePython)
  Dunit = g/cm3
  Dvalue = 1
  Group = -> [H_element128,C_element138,N_element058,O_element119]
  conduct = 2
  density = 1
  expand = 3
  formula = G4_DNA_URACIL
  name = G4_DNA_URACIL
  specific = 4
FEATURE [App::DocumentObjectGroupPython] H_element129  label="H_element : 076"  # scripted group (container) (typed FeaturePython)
  n = 10
  ref = H_element
FEATURE [App::DocumentObjectGroupPython] C_element139  label="C_element : 084"  # scripted group (container) (typed FeaturePython)
  n = 10
  ref = C_element
FEATURE [App::DocumentObjectGroupPython] N_element059  label="N_element : 031"  # scripted group (container) (typed FeaturePython)
  n = 5
  ref = N_element
FEATURE [App::DocumentObjectGroupPython] O_element120  label="O_element : 073"  # scripted group (container) (typed FeaturePython)
  n = 4
  ref = O_element
FEATURE [App::DocumentObjectGroupPython] G4_DNA_ADENOSINE  # scripted group (container) (typed FeaturePython)
  Dunit = g/cm3
  Dvalue = 1
  Group = -> [H_element129,C_element139,N_element059,O_element120]
  conduct = 2
  density = 1
  expand = 3
  formula = G4_DNA_ADENOSINE
  name = G4_DNA_ADENOSINE
  specific = 4
FEATURE [App::DocumentObjectGroupPython] H_element130  label="H_element : 077"  # scripted group (container) (typed FeaturePython)
  n = 10
  ref = H_element
FEATURE [App::DocumentObjectGroupPython] C_element140  label="C_element : 085"  # scripted group (container) (typed FeaturePython)
  n = 10
  ref = C_element
FEATURE [App::DocumentObjectGroupPython] N_element060  label="N_element : 032"  # scripted group (container) (typed FeaturePython)
  n = 5
  ref = N_element
FEATURE [App::DocumentObjectGroupPython] O_element121  label="O_element : 074"  # scripted group (container) (typed FeaturePython)
  n = 5
  ref = O_element
FEATURE [App::DocumentObjectGroupPython] G4_DNA_GUANOSINE  # scripted group (container) (typed FeaturePython)
  Dunit = g/cm3
  Dvalue = 1
  Group = -> [H_element130,C_element140,N_element060,O_element121]
  conduct = 2
  density = 1
  expand = 3
  formula = G4_DNA_GUANOSINE
  name = G4_DNA_GUANOSINE
  specific = 4
FEATURE [App::DocumentObjectGroupPython] H_element131  label="H_element : 078"  # scripted group (container) (typed FeaturePython)
  n = 10
  ref = H_element
FEATURE [App::DocumentObjectGroupPython] C_element141  label="C_element : 086"  # scripted group (container) (typed FeaturePython)
  n = 9
  ref = C_element
FEATURE [App::DocumentObjectGroupPython] N_element061  label="N_element : 033"  # scripted group (container) (typed FeaturePython)
  n = 3
  ref = N_element
FEATURE [App::DocumentObjectGroupPython] O_element122  label="O_element : 075"  # scripted group (container) (typed FeaturePython)
  n = 5
  ref = O_element
FEATURE [App::DocumentObjectGroupPython] G4_DNA_CYTIDINE  # scripted group (container) (typed FeaturePython)
  Dunit = g/cm3
  Dvalue = 1
  Group = -> [H_element131,C_element141,N_element061,O_element122]
  conduct = 2
  density = 1
  expand = 3
  formula = G4_DNA_CYTIDINE
  name = G4_DNA_CYTIDINE
  specific = 4
FEATURE [App::DocumentObjectGroupPython] H_element132  label="H_element : 079"  # scripted group (container) (typed FeaturePython)
  n = 9
  ref = H_element
FEATURE [App::DocumentObjectGroupPython] C_element142  label="C_element : 087"  # scripted group (container) (typed FeaturePython)
  n = 9
  ref = C_element
FEATURE [App::DocumentObjectGroupPython] N_element062  label="N_element : 034"  # scripted group (container) (typed FeaturePython)
  n = 2
  ref = N_element
FEATURE [App::DocumentObjectGroupPython] O_element123  label="O_element : 076"  # scripted group (container) (typed FeaturePython)
  n = 6
  ref = O_element
FEATURE [App::DocumentObjectGroupPython] G4_DNA_URIDINE  # scripted group (container) (typed FeaturePython)
  Dunit = g/cm3
  Dvalue = 1
  Group = -> [H_element132,C_element142,N_element062,O_element123]
  conduct = 2
  density = 1
  expand = 3
  formula = G4_DNA_URIDINE
  name = G4_DNA_URIDINE
  specific = 4
FEATURE [App::DocumentObjectGroupPython] H_element133  label="H_element : 080"  # scripted group (container) (typed FeaturePython)
  n = 11
  ref = H_element
FEATURE [App::DocumentObjectGroupPython] C_element143  label="C_element : 088"  # scripted group (container) (typed FeaturePython)
  n = 10
  ref = C_element
FEATURE [App::DocumentObjectGroupPython] N_element063  label="N_element : 035"  # scripted group (container) (typed FeaturePython)
  n = 2
  ref = N_element
FEATURE [App::DocumentObjectGroupPython] O_element124  label="O_element : 077"  # scripted group (container) (typed FeaturePython)
  n = 6
  ref = O_element
FEATURE [App::DocumentObjectGroupPython] G4_DNA_METHYLURIDINE  # scripted group (container) (typed FeaturePython)
  Dunit = g/cm3
  Dvalue = 1
  Group = -> [H_element133,C_element143,N_element063,O_element124]
  conduct = 2
  density = 1
  expand = 3
  formula = G4_DNA_METHYLURIDINE
  name = G4_DNA_METHYLURIDINE
  specific = 4
FEATURE [App::DocumentObjectGroupPython] P_element014  label="P_element : 003"  # scripted group (container) (typed FeaturePython)
  n = 1
  ref = P_element
FEATURE [App::DocumentObjectGroupPython] O_element125  label="O_element : 078"  # scripted group (container) (typed FeaturePython)
  n = 3
  ref = O_element
FEATURE [App::DocumentObjectGroupPython] G4_DNA_MONOPHOSPHATE  # scripted group (container) (typed FeaturePython)
  Dunit = g/cm3
  Dvalue = 1
  Group = -> [P_element014,O_element125]
  conduct = 2
  density = 1
  expand = 3
  formula = G4_DNA_MONOPHOSPHATE
  name = G4_DNA_MONOPHOSPHATE
  specific = 4
FEATURE [App::DocumentObjectGroupPython] H_element134  label="H_element : 081"  # scripted group (container) (typed FeaturePython)
  n = 10
  ref = H_element
FEATURE [App::DocumentObjectGroupPython] C_element144  label="C_element : 089"  # scripted group (container) (typed FeaturePython)
  n = 10
  ref = C_element
FEATURE [App::DocumentObjectGroupPython] N_element064  label="N_element : 036"  # scripted group (container) (typed FeaturePython)
  n = 5
  ref = N_element
FEATURE [App::DocumentObjectGroupPython] O_element126  label="O_element : 079"  # scripted group (container) (typed FeaturePython)
  n = 7
  ref = O_element
FEATURE [App::DocumentObjectGroupPython] P_element015  label="P_element : 004"  # scripted group (container) (typed FeaturePython)
  n = 1
  ref = P_element
FEATURE [App::DocumentObjectGroupPython] G4_DNA_A  # scripted group (container) (typed FeaturePython)
  Dunit = g/cm3
  Dvalue = 1
  Group = -> [H_element134,C_element144,N_element064,O_element126,P_element015]
  conduct = 2
  density = 1
  expand = 3
  formula = G4_DNA_A
  name = G4_DNA_A
  specific = 4
FEATURE [App::DocumentObjectGroupPython] H_element135  label="H_element : 082"  # scripted group (container) (typed FeaturePython)
  n = 10
  ref = H_element
FEATURE [App::DocumentObjectGroupPython] C_element145  label="C_element : 090"  # scripted group (container) (typed FeaturePython)
  n = 10
  ref = C_element
FEATURE [App::DocumentObjectGroupPython] N_element065  label="N_element : 037"  # scripted group (container) (typed FeaturePython)
  n = 5
  ref = N_element
FEATURE [App::DocumentObjectGroupPython] O_element127  label="O_element : 8"  # scripted group (container) (typed FeaturePython)
  n = 8
  ref = O_element
FEATURE [App::DocumentObjectGroupPython] P_element016  label="P_element : 005"  # scripted group (container) (typed FeaturePython)
  n = 1
  ref = P_element
FEATURE [App::DocumentObjectGroupPython] G4_DNA_G  # scripted group (container) (typed FeaturePython)
  Dunit = g/cm3
  Dvalue = 1
  Group = -> [H_element135,C_element145,N_element065,O_element127,P_element016]
  conduct = 2
  density = 1
  expand = 3
  formula = G4_DNA_G
  name = G4_DNA_G
  specific = 4
FEATURE [App::DocumentObjectGroupPython] H_element136  label="H_element : 083"  # scripted group (container) (typed FeaturePython)
  n = 10
  ref = H_element
FEATURE [App::DocumentObjectGroupPython] C_element146  label="C_element : 091"  # scripted group (container) (typed FeaturePython)
  n = 9
  ref = C_element
FEATURE [App::DocumentObjectGroupPython] N_element066  label="N_element : 038"  # scripted group (container) (typed FeaturePython)
  n = 3
  ref = N_element
FEATURE [App::DocumentObjectGroupPython] O_element128  label="O_element : 080"  # scripted group (container) (typed FeaturePython)
  n = 8
  ref = O_element
FEATURE [App::DocumentObjectGroupPython] P_element017  label="P_element : 006"  # scripted group (container) (typed FeaturePython)
  n = 1
  ref = P_element
FEATURE [App::DocumentObjectGroupPython] G4_DNA_C  # scripted group (container) (typed FeaturePython)
  Dunit = g/cm3
  Dvalue = 1
  Group = -> [H_element136,C_element146,N_element066,O_element128,P_element017]
  conduct = 2
  density = 1
  expand = 3
  formula = G4_DNA_C
  name = G4_DNA_C
  specific = 4
FEATURE [App::DocumentObjectGroupPython] H_element137  label="H_element : 084"  # scripted group (container) (typed FeaturePython)
  n = 9
  ref = H_element
FEATURE [App::DocumentObjectGroupPython] C_element147  label="C_element : 092"  # scripted group (container) (typed FeaturePython)
  n = 9
  ref = C_element
FEATURE [App::DocumentObjectGroupPython] N_element067  label="N_element : 039"  # scripted group (container) (typed FeaturePython)
  n = 2
  ref = N_element
FEATURE [App::DocumentObjectGroupPython] O_element129  label="O_element : 9"  # scripted group (container) (typed FeaturePython)
  n = 9
  ref = O_element
FEATURE [App::DocumentObjectGroupPython] P_element018  label="P_element : 007"  # scripted group (container) (typed FeaturePython)
  n = 1
  ref = P_element
FEATURE [App::DocumentObjectGroupPython] G4_DNA_U  # scripted group (container) (typed FeaturePython)
  Dunit = g/cm3
  Dvalue = 1
  Group = -> [H_element137,C_element147,N_element067,O_element129,P_element018]
  conduct = 2
  density = 1
  expand = 3
  formula = G4_DNA_U
  name = G4_DNA_U
  specific = 4
FEATURE [App::DocumentObjectGroupPython] H_element138  label="H_element : 085"  # scripted group (container) (typed FeaturePython)
  n = 11
  ref = H_element
FEATURE [App::DocumentObjectGroupPython] C_element148  label="C_element : 093"  # scripted group (container) (typed FeaturePython)
  n = 10
  ref = C_element
FEATURE [App::DocumentObjectGroupPython] N_element068  label="N_element : 040"  # scripted group (container) (typed FeaturePython)
  n = 2
  ref = N_element
FEATURE [App::DocumentObjectGroupPython] O_element130  label="O_element : 081"  # scripted group (container) (typed FeaturePython)
  n = 9
  ref = O_element
FEATURE [App::DocumentObjectGroupPython] P_element019  label="P_element : 008"  # scripted group (container) (typed FeaturePython)
  n = 1
  ref = P_element
FEATURE [App::DocumentObjectGroupPython] G4_DNA_MU  # scripted group (container) (typed FeaturePython)
  Dunit = g/cm3
  Dvalue = 1
  Group = -> [H_element138,C_element148,N_element068,O_element130,P_element019]
  conduct = 2
  density = 1
  expand = 3
  formula = G4_DNA_MU
  name = G4_DNA_MU
  specific = 4
FEATURE [App::DocumentObjectGroupPython] BioChemical  # scripted group (container) (typed FeaturePython)
  Group = -> [G4_CYTOSINE,G4_THYMINE,G4_URACIL,G4_DNA_ADENINE,G4_DNA_GUANINE,G4_DNA_CYTOSINE,G4_DNA_THYMINE,G4_DNA_URACIL,G4_DNA_ADENOSINE,G4_DNA_GUANOSINE,G4_DNA_CYTIDINE,G4_DNA_URIDINE,G4_DNA_METHYLURIDINE,G4_DNA_MONOPHOSPHATE,G4_DNA_A,G4_DNA_G,G4_DNA_C,G4_DNA_U,G4_DNA_MU]
FEATURE [App::DocumentObjectGroupPython] G4Materials  # scripted group (container) (typed FeaturePython)
  Group = -> [NIST,Element,HEP,Space,BioChemical]
  version = 1
FEATURE [App::DocumentObjectGroupPython] Geant4  # scripted group (container) (typed FeaturePython)
  Group = -> [G4Isotopes,G4Elements,G4Materials]
FEATURE [App::DocumentObjectGroupPython] Materials  # scripted group (container) (typed FeaturePython)
  Group = -> [Geant4]
FEATURE [Part::FeaturePython] GDMLBox_WorldBox  # WARN: FeaturePython — macro-defined, semantics opaque (R4)
  lunit = 2
  material = 7
  x = 65
  y = 64.21
  z = 117
FEATURE [Part::Helix] Helix
  Angle = 0
  AttacherType = Attacher::AttachEngine3D
  Height = 40
  LocalCoord = 0
  Pitch = 15
  Radius = 20
  SegmentLength = 0
  Style = 1
FEATURE [Part::FeaturePython] GDMLBox_Box  # WARN: FeaturePython — macro-defined, semantics opaque (R4)
  lunit = 2
  material = 0
  x = 10
  y = 10
  z = 10
FEATURE [Part::Cone] Cone001
  Angle = 360
  AttacherType = Attacher::AttachEngine3D
  Height = 4
  Radius1 = 0
  Radius2 = 2
FEATURE [App::Part] Part001  label="LV_Cone"
  Group = -> [Cone001]
  Origin = -> Origin003
  Placement = pos=(0,0,0.5) rot=(0,0,1;0rad)
FEATURE [Part::FeaturePython] GDMLSphere  # WARN: FeaturePython — macro-defined, semantics opaque (R4)
  aunit = 1
  deltaphi = 360
  deltatheta = 180
  lunit = 2
  material = 0
  rmax = 2
  rmin = 0
  startphi = 0
  starttheta = 0
FEATURE [App::Part] LV_Sphere
  Group = -> [GDMLSphere]
  Origin = -> Origin004
  Placement = pos=(0,0,-2) rot=(0,0,1;0rad)
  SkinSurface = 0
FEATURE [App::Part] LV_Box  label="Container"
  Group = -> [GDMLBox_Box,Part001,LV_Sphere]
  Origin = -> Origin002
FEATURE [Part::FeaturePython] PathArray  # WARN: FeaturePython — macro-defined, semantics opaque (R4)
  Align = false
  AlignMode = 0
  Base = -> LV_Box
  Count = 10
  EndOffset = 0
  ExtraTranslation = (0,0,0)
  ForceVertical = false
  PathObject = -> Helix
  StartOffset = 0
  TangentVector = (1,0,0)
  VerticalVector = (0,0,1)
FEATURE [App::Part] Part
  Group = -> [PathArray]
  Origin = -> Origin001
FEATURE [App::Part] worldVOL
  Group = -> [GDMLBox_WorldBox,Part]
  Origin = -> Origin
